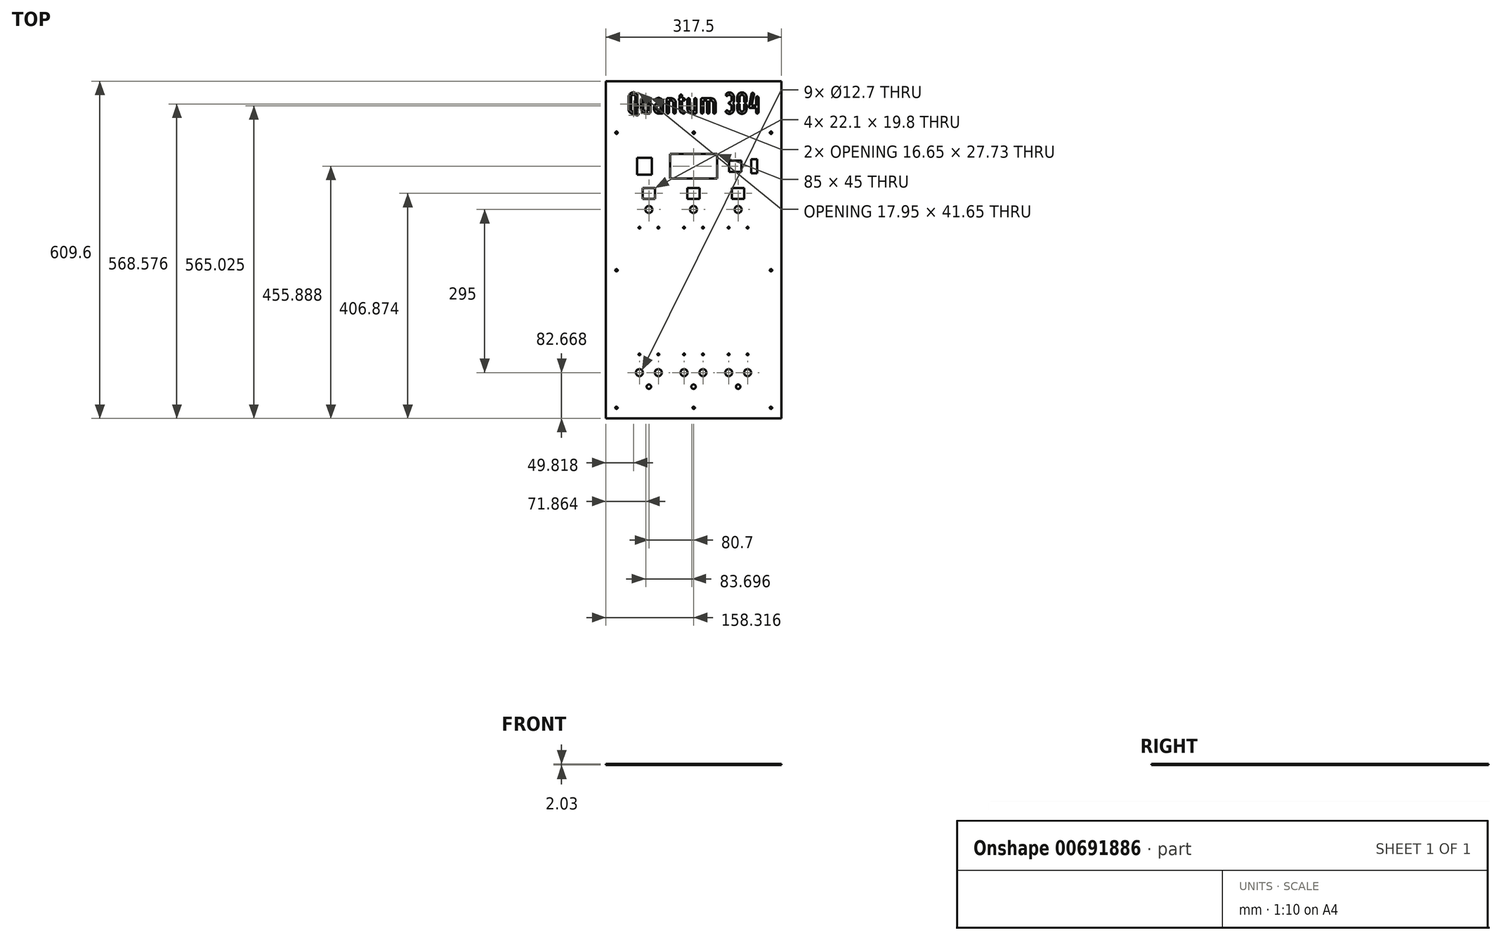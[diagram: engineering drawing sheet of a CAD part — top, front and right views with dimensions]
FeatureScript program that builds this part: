
annotation { "Feature Type Name" : "Feature", "Feature Type Description" : "" }
export const myFeature = defineFeature(function(context is Context, id is Id, definition is map)
    precondition{}
    {
        {
            var Q0;
            Q0=qCreatedBy(makeId("Top.planeOp"),FACE);
            var sketch = newSketch(context, id + "F0", { "sketchPlane" : qUnion([Q0])});
            skLineSegment(sketch, "E0.bottom", {"start": v(1.2, 127.96) * mm, "end": v(69.2, 127.96) * mm, "construction": true});
            skLineSegment(sketch, "E0.top", {"start": v(1.2, -116.24) * mm, "end": v(69.2, -116.24) * mm, "construction": true});
            skLineSegment(sketch, "E0.left", {"start": v(1.2, 127.96) * mm, "end": v(1.2, -116.24) * mm, "construction": true});
            skLineSegment(sketch, "E0.right", {"start": v(69.2, 127.96) * mm, "end": v(69.2, -116.24) * mm, "construction": true});
            skLineSegment(sketch, "E1.0", {"start": v(1.2, -104.24) * mm, "end": v(69.2, -104.24) * mm, "construction": true});
            skLineSegment(sketch, "E2.0", {"start": v(1.2, 115.96) * mm, "end": v(69.2, 115.96) * mm, "construction": true});
            skLineSegment(sketch, "E3", {"start": v(1.2, 5.86) * mm, "end": v(69.2, 5.86) * mm, "construction": true});
            skLineSegment(sketch, "E4.0", {"start": v(35.2, 127.96) * mm, "end": v(35.2, -116.24) * mm, "construction": true});
            skCircle(sketch, "E5", {"center": v(52.3, 120.46) * mm, "radius": 1.63 * mm});
            skCircle(sketch, "E6.MirrorC", {"center": v(18.1, 120.46) * mm, "radius": 1.63 * mm});
            skCircle(sketch, "E7.MirrorC", {"center": v(18.1, -108.74) * mm, "radius": 1.63 * mm});
            skCircle(sketch, "E8.MirrorC", {"center": v(52.3, -108.74) * mm, "radius": 1.63 * mm});
            skLineSegment(sketch, "E9.MirrorCS", {"start": v(81.9, 127.96) * mm, "end": v(81.9, -116.24) * mm, "construction": true});
            skLineSegment(sketch, "E10.MirrorCS", {"start": v(149.9, 127.96) * mm, "end": v(81.9, 127.96) * mm, "construction": true});
            skLineSegment(sketch, "E11.MirrorCS", {"start": v(149.9, 127.96) * mm, "end": v(149.9, -116.24) * mm, "construction": true});
            skLineSegment(sketch, "E12.MirrorCS", {"start": v(149.9, -116.24) * mm, "end": v(81.9, -116.24) * mm});
            skLineSegment(sketch, "E13.MirrorCS", {"start": v(149.9, -104.24) * mm, "end": v(81.9, -104.24) * mm, "construction": true});
            skLineSegment(sketch, "E14.MirrorCS", {"start": v(115.9, 127.96) * mm, "end": v(115.9, -116.24) * mm, "construction": true});
            skLineSegment(sketch, "E15.MirrorCS", {"start": v(149.9, 5.86) * mm, "end": v(81.9, 5.86) * mm, "construction": true});
            skLineSegment(sketch, "E16.MirrorCS", {"start": v(149.9, 115.96) * mm, "end": v(81.9, 115.96) * mm, "construction": true});
            skCircle(sketch, "E17.MirrorC", {"center": v(133, 120.46) * mm, "radius": 1.63 * mm});
            skCircle(sketch, "E18.MirrorC", {"center": v(98.8, 120.46) * mm, "radius": 1.63 * mm});
            skCircle(sketch, "E19.MirrorC", {"center": v(98.8, -108.74) * mm, "radius": 1.63 * mm});
            skCircle(sketch, "E20.MirrorC", {"center": v(133, -108.74) * mm, "radius": 1.63 * mm});
            skLineSegment(sketch, "E21.MirrorCS", {"start": v(162.6, 127.96) * mm, "end": v(162.6, -116.24) * mm, "construction": true});
            skLineSegment(sketch, "E22.MirrorCS", {"start": v(162.6, 127.96) * mm, "end": v(230.6, 127.96) * mm, "construction": true});
            skLineSegment(sketch, "E23.MirrorCS", {"start": v(230.6, 127.96) * mm, "end": v(230.6, -116.24) * mm, "construction": true});
            skLineSegment(sketch, "E24.MirrorCS", {"start": v(162.6, -116.24) * mm, "end": v(230.6, -116.24) * mm, "construction": true});
            skLineSegment(sketch, "E25.MirrorCS", {"start": v(162.6, -104.24) * mm, "end": v(230.6, -104.24) * mm, "construction": true});
            skLineSegment(sketch, "E26.MirrorCS", {"start": v(196.6, 127.96) * mm, "end": v(196.6, -116.24) * mm, "construction": true});
            skLineSegment(sketch, "E27.MirrorCS", {"start": v(162.6, 5.86) * mm, "end": v(230.6, 5.86) * mm, "construction": true});
            skLineSegment(sketch, "E28.MirrorCS", {"start": v(162.6, 115.96) * mm, "end": v(230.6, 115.96) * mm, "construction": true});
            skCircle(sketch, "E29.MirrorC", {"center": v(179.5, 120.46) * mm, "radius": 1.63 * mm});
            skCircle(sketch, "E30.MirrorC", {"center": v(213.7, 120.46) * mm, "radius": 1.63 * mm});
            skCircle(sketch, "E31.MirrorC", {"center": v(179.5, -108.74) * mm, "radius": 1.63 * mm});
            skCircle(sketch, "E32.MirrorC", {"center": v(213.7, -108.74) * mm, "radius": 1.63 * mm});
            skCircle(sketch, "E33", {"center": v(18.1, -141.64) * mm, "radius": 6.35 * mm});
            skCircle(sketch, "E34", {"center": v(52.3, -141.64) * mm, "radius": 6.35 * mm});
            skCircle(sketch, "E35.MirrorC", {"center": v(98.8, -141.64) * mm, "radius": 6.35 * mm});
            skCircle(sketch, "E36.MirrorC", {"center": v(133, -141.64) * mm, "radius": 6.35 * mm});
            skCircle(sketch, "E37.MirrorC", {"center": v(179.5, -141.64) * mm, "radius": 6.35 * mm});
            skCircle(sketch, "E38.MirrorC", {"center": v(213.7, -141.64) * mm, "radius": 6.35 * mm});
            skCircle(sketch, "E39", {"center": v(115.9, 153.36) * mm, "radius": 6.35 * mm});
            skCircle(sketch, "E40.MirrorC", {"center": v(196.6, 153.36) * mm, "radius": 6.35 * mm});
            skCircle(sketch, "E41.MirrorC", {"center": v(35.2, 153.36) * mm, "radius": 6.35 * mm});
            skCircle(sketch, "E42", {"center": v(115.9, 153.36) * mm, "radius": 8.26 * mm, "construction": true});
            skCircle(sketch, "E43.MirrorC", {"center": v(196.6, 153.36) * mm, "radius": 8.26 * mm, "construction": true});
            skCircle(sketch, "E44.MirrorC", {"center": v(35.2, 153.36) * mm, "radius": 8.26 * mm, "construction": true});
            skCircle(sketch, "E45", {"center": v(98.8, -141.64) * mm, "radius": 8.26 * mm, "construction": true});
            skCircle(sketch, "E46.MirrorC", {"center": v(133, -141.64) * mm, "radius": 8.26 * mm, "construction": true});
            skCircle(sketch, "E47.MirrorC", {"center": v(52.3, -141.64) * mm, "radius": 8.26 * mm, "construction": true});
            skCircle(sketch, "E48.MirrorC", {"center": v(18.1, -141.64) * mm, "radius": 8.26 * mm, "construction": true});
            skCircle(sketch, "E49.MirrorC", {"center": v(179.5, -141.64) * mm, "radius": 8.26 * mm, "construction": true});
            skCircle(sketch, "E50.MirrorC", {"center": v(213.7, -141.64) * mm, "radius": 8.26 * mm, "construction": true});
            skCircle(sketch, "E51", {"center": v(35.2, -167.04) * mm, "radius": 3.97 * mm});
            skCircle(sketch, "E52", {"center": v(35.2, -167.04) * mm, "radius": 12.5 * mm, "construction": true});
            skCircle(sketch, "E53.MirrorC", {"center": v(115.9, -167.04) * mm, "radius": 12.5 * mm, "construction": true});
            skCircle(sketch, "E54.MirrorC", {"center": v(115.9, -167.04) * mm, "radius": 3.97 * mm});
            skCircle(sketch, "E55.MirrorC", {"center": v(196.6, -167.04) * mm, "radius": 12.5 * mm, "construction": true});
            skCircle(sketch, "E56.MirrorC", {"center": v(196.6, -167.04) * mm, "radius": 3.97 * mm});
            skLineSegment(sketch, "E57", {"start": v(-42.41, -224.31) * mm, "end": v(275.09, -224.31) * mm});
            skLineSegment(sketch, "E58.0", {"start": v(-4.71, -186.21) * mm, "end": v(237.39, -186.21) * mm, "construction": true});
            skLineSegment(sketch, "E59.0", {"start": v(237.39, 311.23) * mm, "end": v(237.39, -224.31) * mm, "construction": true});
            skLineSegment(sketch, "E60.0", {"start": v(-4.71, 311.23) * mm, "end": v(-4.71, -224.31) * mm, "construction": true});
            skLineSegment(sketch, "E61.bottom", {"start": v(73.4, 254.08) * mm, "end": v(158.4, 254.08) * mm});
            skLineSegment(sketch, "E61.top", {"start": v(73.4, 209.08) * mm, "end": v(158.4, 209.08) * mm});
            skLineSegment(sketch, "E61.left", {"start": v(73.4, 254.08) * mm, "end": v(73.4, 209.08) * mm});
            skLineSegment(sketch, "E61.right", {"start": v(158.4, 254.08) * mm, "end": v(158.4, 209.08) * mm});
            skLineSegment(sketch, "E62.bottom", {"start": v(104.86, 192.46) * mm, "end": v(126.96, 192.46) * mm});
            skLineSegment(sketch, "E62.top", {"start": v(104.86, 172.66) * mm, "end": v(126.96, 172.66) * mm});
            skLineSegment(sketch, "E62.left", {"start": v(104.86, 192.46) * mm, "end": v(104.86, 172.66) * mm});
            skLineSegment(sketch, "E62.right", {"start": v(126.96, 192.46) * mm, "end": v(126.96, 172.66) * mm});
            skLineSegment(sketch, "E63.MirrorCS", {"start": v(185.56, 192.46) * mm, "end": v(185.56, 172.66) * mm});
            skLineSegment(sketch, "E64.MirrorCS", {"start": v(207.66, 192.46) * mm, "end": v(185.56, 192.46) * mm});
            skLineSegment(sketch, "E65.MirrorCS", {"start": v(207.66, 192.46) * mm, "end": v(207.66, 172.66) * mm});
            skLineSegment(sketch, "E66.MirrorCS", {"start": v(207.66, 172.66) * mm, "end": v(185.56, 172.66) * mm});
            skLineSegment(sketch, "E67.MirrorCS", {"start": v(46.26, 192.46) * mm, "end": v(46.26, 172.66) * mm});
            skLineSegment(sketch, "E68.MirrorCS", {"start": v(46.26, 192.46) * mm, "end": v(24.16, 192.46) * mm});
            skLineSegment(sketch, "E69.MirrorCS", {"start": v(24.16, 192.46) * mm, "end": v(24.16, 172.66) * mm});
            skLineSegment(sketch, "E70.MirrorCS", {"start": v(46.26, 172.66) * mm, "end": v(24.16, 172.66) * mm});
            skLineSegment(sketch, "E71.bottom", {"start": v(14.08, 246.75) * mm, "end": v(40.58, 246.75) * mm});
            skLineSegment(sketch, "E71.top", {"start": v(14.08, 216.4) * mm, "end": v(40.58, 216.4) * mm});
            skLineSegment(sketch, "E71.left", {"start": v(14.08, 246.75) * mm, "end": v(14.08, 216.4) * mm});
            skLineSegment(sketch, "E71.right", {"start": v(40.58, 246.75) * mm, "end": v(40.58, 216.4) * mm});
            skLineSegment(sketch, "E72.0", {"start": v(73.84, 231.58) * mm, "end": v(158.84, 231.58) * mm, "construction": true});
            skLineSegment(sketch, "E73", {"start": v(73.84, 231.58) * mm, "end": v(-4.71, 231.58) * mm, "construction": true});
            skLineSegment(sketch, "E74", {"start": v(158.84, 231.58) * mm, "end": v(237.39, 231.58) * mm, "construction": true});
            skLineSegment(sketch, "E75", {"start": v(237.39, 273.13) * mm, "end": v(-4.71, 273.13) * mm, "construction": true});
            skLineSegment(sketch, "E76.0", {"start": v(237.39, 311.23) * mm, "end": v(-4.71, 311.23) * mm, "construction": true});
            skLineSegment(sketch, "E77", {"start": v(-1.54, 357.62) * mm, "end": v(-1.43, 358.44) * mm});
            skLineSegment(sketch, "E78", {"start": v(-1.43, 358.44) * mm, "end": v(-1.23, 359.2) * mm});
            skLineSegment(sketch, "E79", {"start": v(-1.23, 359.2) * mm, "end": v(-0.97, 359.98) * mm});
            skLineSegment(sketch, "E80", {"start": v(-0.97, 359.98) * mm, "end": v(-0.6, 360.69) * mm});
            skLineSegment(sketch, "E81", {"start": v(-0.6, 360.69) * mm, "end": v(-0.2, 361.37) * mm});
            skLineSegment(sketch, "E82", {"start": v(-0.2, 361.37) * mm, "end": v(0.3, 362.02) * mm});
            skLineSegment(sketch, "E83", {"start": v(0.3, 362.02) * mm, "end": v(0.87, 362.65) * mm});
            skLineSegment(sketch, "E84", {"start": v(0.87, 362.65) * mm, "end": v(1.5, 363.22) * mm});
            skLineSegment(sketch, "E85", {"start": v(1.5, 363.22) * mm, "end": v(2.15, 363.73) * mm});
            skLineSegment(sketch, "E86", {"start": v(2.15, 363.73) * mm, "end": v(2.83, 364.12) * mm});
            skLineSegment(sketch, "E87", {"start": v(2.83, 364.12) * mm, "end": v(3.54, 364.5) * mm});
            skLineSegment(sketch, "E88", {"start": v(3.54, 364.5) * mm, "end": v(4.31, 364.75) * mm});
            skLineSegment(sketch, "E89", {"start": v(4.31, 364.75) * mm, "end": v(5.08, 364.95) * mm});
            skLineSegment(sketch, "E90", {"start": v(5.08, 364.95) * mm, "end": v(5.9, 365.06) * mm});
            skLineSegment(sketch, "E91", {"start": v(5.9, 365.06) * mm, "end": v(6.75, 365.1) * mm});
            skLineSegment(sketch, "E92", {"start": v(6.75, 365.1) * mm, "end": v(7.58, 365.06) * mm});
            skLineSegment(sketch, "E93", {"start": v(7.58, 365.06) * mm, "end": v(8.4, 364.95) * mm});
            skLineSegment(sketch, "E94", {"start": v(8.4, 364.95) * mm, "end": v(9.17, 364.75) * mm});
            skLineSegment(sketch, "E95", {"start": v(9.17, 364.75) * mm, "end": v(9.94, 364.5) * mm});
            skLineSegment(sketch, "E96", {"start": v(9.94, 364.5) * mm, "end": v(10.65, 364.12) * mm});
            skLineSegment(sketch, "E97", {"start": v(10.65, 364.12) * mm, "end": v(11.33, 363.73) * mm});
            skLineSegment(sketch, "E98", {"start": v(11.33, 363.73) * mm, "end": v(11.98, 363.22) * mm});
            skLineSegment(sketch, "E99", {"start": v(11.98, 363.22) * mm, "end": v(12.6, 362.65) * mm});
            skLineSegment(sketch, "E100", {"start": v(12.6, 362.65) * mm, "end": v(13.18, 362.02) * mm});
            skLineSegment(sketch, "E101", {"start": v(13.18, 362.02) * mm, "end": v(13.69, 361.37) * mm});
            skLineSegment(sketch, "E102", {"start": v(13.69, 361.37) * mm, "end": v(14.08, 360.69) * mm});
            skLineSegment(sketch, "E103", {"start": v(14.08, 360.69) * mm, "end": v(14.45, 359.98) * mm});
            skLineSegment(sketch, "E104", {"start": v(14.45, 359.98) * mm, "end": v(14.7, 359.2) * mm});
            skLineSegment(sketch, "E105", {"start": v(14.7, 359.2) * mm, "end": v(14.9, 358.44) * mm});
            skLineSegment(sketch, "E106", {"start": v(14.9, 358.44) * mm, "end": v(15.02, 357.62) * mm});
            skLineSegment(sketch, "E107", {"start": v(15.02, 357.62) * mm, "end": v(15.05, 356.8) * mm});
            skLineSegment(sketch, "E108", {"start": v(15.05, 356.8) * mm, "end": v(15.05, 334.63) * mm});
            skLineSegment(sketch, "E109", {"start": v(15.05, 334.63) * mm, "end": v(15.05, 334.38) * mm});
            skLineSegment(sketch, "E110", {"start": v(15.05, 334.38) * mm, "end": v(15.05, 334.12) * mm});
            skLineSegment(sketch, "E111", {"start": v(15.05, 334.12) * mm, "end": v(15.02, 333.87) * mm});
            skLineSegment(sketch, "E112", {"start": v(15.02, 333.87) * mm, "end": v(15, 333.61) * mm});
            skLineSegment(sketch, "E113", {"start": v(15, 333.61) * mm, "end": v(14.97, 333.38) * mm});
            skLineSegment(sketch, "E114", {"start": v(14.97, 333.38) * mm, "end": v(14.94, 333.13) * mm});
            skLineSegment(sketch, "E115", {"start": v(14.94, 333.13) * mm, "end": v(14.9, 332.9) * mm});
            skLineSegment(sketch, "E116", {"start": v(14.9, 332.9) * mm, "end": v(14.85, 332.65) * mm});
            skLineSegment(sketch, "E117", {"start": v(14.85, 332.65) * mm, "end": v(14.82, 332.5) * mm});
            skLineSegment(sketch, "E118", {"start": v(14.82, 332.5) * mm, "end": v(14.77, 332.33) * mm});
            skLineSegment(sketch, "E119", {"start": v(14.77, 332.33) * mm, "end": v(14.7, 332.2) * mm});
            skLineSegment(sketch, "E120", {"start": v(14.7, 332.2) * mm, "end": v(14.65, 332.05) * mm});
            skLineSegment(sketch, "E121", {"start": v(14.65, 332.05) * mm, "end": v(14.57, 331.94) * mm});
            skLineSegment(sketch, "E122", {"start": v(14.57, 331.94) * mm, "end": v(14.48, 331.8) * mm});
            skLineSegment(sketch, "E123", {"start": v(14.48, 331.8) * mm, "end": v(14.37, 331.68) * mm});
            skLineSegment(sketch, "E124", {"start": v(14.37, 331.68) * mm, "end": v(14.26, 331.54) * mm});
            skLineSegment(sketch, "E125", {"start": v(14.26, 331.54) * mm, "end": v(14.08, 331.4) * mm});
            skLineSegment(sketch, "E126", {"start": v(14.08, 331.4) * mm, "end": v(13.89, 331.25) * mm});
            skLineSegment(sketch, "E127", {"start": v(13.89, 331.25) * mm, "end": v(13.72, 331.14) * mm});
            skLineSegment(sketch, "E128", {"start": v(13.72, 331.14) * mm, "end": v(13.52, 331.06) * mm});
            skLineSegment(sketch, "E129", {"start": v(13.52, 331.06) * mm, "end": v(13.32, 330.97) * mm});
            skLineSegment(sketch, "E130", {"start": v(13.32, 330.97) * mm, "end": v(13.12, 330.91) * mm});
            skLineSegment(sketch, "E131", {"start": v(13.12, 330.91) * mm, "end": v(12.9, 330.88) * mm});
            skLineSegment(sketch, "E132", {"start": v(12.9, 330.88) * mm, "end": v(12.66, 330.88) * mm});
            skLineSegment(sketch, "E133", {"start": v(12.66, 330.88) * mm, "end": v(12.44, 330.88) * mm});
            skLineSegment(sketch, "E134", {"start": v(12.44, 330.88) * mm, "end": v(12.24, 330.91) * mm});
            skLineSegment(sketch, "E135", {"start": v(12.24, 330.91) * mm, "end": v(12.01, 330.97) * mm});
            skLineSegment(sketch, "E136", {"start": v(12.01, 330.97) * mm, "end": v(11.81, 331.06) * mm});
            skLineSegment(sketch, "E137", {"start": v(11.81, 331.06) * mm, "end": v(11.64, 331.14) * mm});
            skLineSegment(sketch, "E138", {"start": v(11.64, 331.14) * mm, "end": v(11.44, 331.25) * mm});
            skLineSegment(sketch, "E139", {"start": v(11.44, 331.25) * mm, "end": v(11.27, 331.37) * mm});
            skLineSegment(sketch, "E140", {"start": v(11.27, 331.37) * mm, "end": v(11.1, 331.54) * mm});
            skLineSegment(sketch, "E141", {"start": v(11.1, 331.54) * mm, "end": v(10.96, 331.7) * mm});
            skLineSegment(sketch, "E142", {"start": v(10.96, 331.7) * mm, "end": v(10.82, 331.88) * mm});
            skLineSegment(sketch, "E143", {"start": v(10.82, 331.88) * mm, "end": v(10.7, 332.05) * mm});
            skLineSegment(sketch, "E144", {"start": v(10.7, 332.05) * mm, "end": v(10.62, 332.25) * mm});
            skLineSegment(sketch, "E145", {"start": v(10.62, 332.25) * mm, "end": v(10.53, 332.45) * mm});
            skLineSegment(sketch, "E146", {"start": v(10.53, 332.45) * mm, "end": v(10.5, 332.65) * mm});
            skLineSegment(sketch, "E147", {"start": v(10.5, 332.65) * mm, "end": v(10.48, 332.87) * mm});
            skLineSegment(sketch, "E148", {"start": v(10.48, 332.87) * mm, "end": v(10.45, 333.1) * mm});
            skLineSegment(sketch, "E149", {"start": v(10.45, 333.1) * mm, "end": v(10.45, 333.16) * mm});
            skLineSegment(sketch, "E150", {"start": v(10.45, 333.16) * mm, "end": v(10.45, 333.21) * mm});
            skLineSegment(sketch, "E151", {"start": v(10.45, 333.21) * mm, "end": v(10.45, 333.27) * mm});
            skLineSegment(sketch, "E152", {"start": v(10.45, 333.27) * mm, "end": v(10.45, 333.33) * mm});
            skLineSegment(sketch, "E153", {"start": v(10.45, 333.33) * mm, "end": v(10.48, 333.38) * mm});
            skLineSegment(sketch, "E154", {"start": v(10.48, 333.38) * mm, "end": v(10.48, 333.47) * mm});
            skLineSegment(sketch, "E155", {"start": v(10.48, 333.47) * mm, "end": v(10.48, 333.53) * mm});
            skLineSegment(sketch, "E156", {"start": v(10.48, 333.53) * mm, "end": v(10.48, 333.58) * mm});
            skLineSegment(sketch, "E157", {"start": v(10.48, 333.58) * mm, "end": v(10.5, 333.73) * mm});
            skLineSegment(sketch, "E158", {"start": v(10.5, 333.73) * mm, "end": v(10.53, 333.84) * mm});
            skLineSegment(sketch, "E159", {"start": v(10.53, 333.84) * mm, "end": v(10.56, 333.98) * mm});
            skLineSegment(sketch, "E160", {"start": v(10.56, 333.98) * mm, "end": v(10.6, 334.1) * mm});
            skLineSegment(sketch, "E161", {"start": v(10.6, 334.1) * mm, "end": v(10.6, 334.24) * mm});
            skLineSegment(sketch, "E162", {"start": v(10.6, 334.24) * mm, "end": v(10.62, 334.35) * mm});
            skLineSegment(sketch, "E163", {"start": v(10.62, 334.35) * mm, "end": v(10.62, 334.5) * mm});
            skLineSegment(sketch, "E164", {"start": v(10.62, 334.5) * mm, "end": v(10.62, 334.63) * mm});
            skLineSegment(sketch, "E165", {"start": v(10.62, 334.63) * mm, "end": v(10.62, 356.8) * mm});
            skLineSegment(sketch, "E166", {"start": v(10.62, 356.8) * mm, "end": v(10.6, 357.16) * mm});
            skLineSegment(sketch, "E167", {"start": v(10.6, 357.16) * mm, "end": v(10.56, 357.56) * mm});
            skLineSegment(sketch, "E168", {"start": v(10.56, 357.56) * mm, "end": v(10.45, 357.93) * mm});
            skLineSegment(sketch, "E169", {"start": v(10.45, 357.93) * mm, "end": v(10.33, 358.27) * mm});
            skLineSegment(sketch, "E170", {"start": v(10.33, 358.27) * mm, "end": v(10.16, 358.61) * mm});
            skLineSegment(sketch, "E171", {"start": v(10.16, 358.61) * mm, "end": v(10, 358.93) * mm});
            skLineSegment(sketch, "E172", {"start": v(10, 358.93) * mm, "end": v(9.74, 359.24) * mm});
            skLineSegment(sketch, "E173", {"start": v(9.74, 359.24) * mm, "end": v(9.48, 359.52) * mm});
            skLineSegment(sketch, "E174", {"start": v(9.48, 359.52) * mm, "end": v(9.2, 359.78) * mm});
            skLineSegment(sketch, "E175", {"start": v(9.2, 359.78) * mm, "end": v(8.89, 360.03) * mm});
            skLineSegment(sketch, "E176", {"start": v(8.89, 360.03) * mm, "end": v(8.57, 360.2) * mm});
            skLineSegment(sketch, "E177", {"start": v(8.57, 360.2) * mm, "end": v(8.23, 360.37) * mm});
            skLineSegment(sketch, "E178", {"start": v(8.23, 360.37) * mm, "end": v(7.9, 360.49) * mm});
            skLineSegment(sketch, "E179", {"start": v(7.9, 360.49) * mm, "end": v(7.52, 360.6) * mm});
            skLineSegment(sketch, "E180", {"start": v(7.52, 360.6) * mm, "end": v(7.12, 360.63) * mm});
            skLineSegment(sketch, "E181", {"start": v(7.12, 360.63) * mm, "end": v(6.75, 360.66) * mm});
            skLineSegment(sketch, "E182", {"start": v(6.75, 360.66) * mm, "end": v(6.36, 360.63) * mm});
            skLineSegment(sketch, "E183", {"start": v(6.36, 360.63) * mm, "end": v(5.96, 360.6) * mm});
            skLineSegment(sketch, "E184", {"start": v(5.96, 360.6) * mm, "end": v(5.6, 360.49) * mm});
            skLineSegment(sketch, "E185", {"start": v(5.6, 360.49) * mm, "end": v(5.25, 360.37) * mm});
            skLineSegment(sketch, "E186", {"start": v(5.25, 360.37) * mm, "end": v(4.9, 360.2) * mm});
            skLineSegment(sketch, "E187", {"start": v(4.9, 360.2) * mm, "end": v(4.6, 360.03) * mm});
            skLineSegment(sketch, "E188", {"start": v(4.6, 360.03) * mm, "end": v(4.28, 359.78) * mm});
            skLineSegment(sketch, "E189", {"start": v(4.28, 359.78) * mm, "end": v(4, 359.52) * mm});
            skLineSegment(sketch, "E190", {"start": v(4, 359.52) * mm, "end": v(3.74, 359.24) * mm});
            skLineSegment(sketch, "E191", {"start": v(3.74, 359.24) * mm, "end": v(3.49, 358.93) * mm});
            skLineSegment(sketch, "E192", {"start": v(3.49, 358.93) * mm, "end": v(3.32, 358.61) * mm});
            skLineSegment(sketch, "E193", {"start": v(3.32, 358.61) * mm, "end": v(3.15, 358.27) * mm});
            skLineSegment(sketch, "E194", {"start": v(3.15, 358.27) * mm, "end": v(3.03, 357.93) * mm});
            skLineSegment(sketch, "E195", {"start": v(3.03, 357.93) * mm, "end": v(2.92, 357.56) * mm});
            skLineSegment(sketch, "E196", {"start": v(2.92, 357.56) * mm, "end": v(2.9, 357.16) * mm});
            skLineSegment(sketch, "E197", {"start": v(2.9, 357.16) * mm, "end": v(2.86, 356.8) * mm});
            skLineSegment(sketch, "E198", {"start": v(2.86, 356.8) * mm, "end": v(2.86, 334.63) * mm});
            skLineSegment(sketch, "E199", {"start": v(2.86, 334.63) * mm, "end": v(2.9, 334.24) * mm});
            skLineSegment(sketch, "E200", {"start": v(2.9, 334.24) * mm, "end": v(2.92, 333.87) * mm});
            skLineSegment(sketch, "E201", {"start": v(2.92, 333.87) * mm, "end": v(3, 333.53) * mm});
            skLineSegment(sketch, "E202", {"start": v(3, 333.53) * mm, "end": v(3.12, 333.19) * mm});
            skLineSegment(sketch, "E203", {"start": v(3.12, 333.19) * mm, "end": v(3.29, 332.87) * mm});
            skLineSegment(sketch, "E204", {"start": v(3.29, 332.87) * mm, "end": v(3.46, 332.59) * mm});
            skLineSegment(sketch, "E205", {"start": v(3.46, 332.59) * mm, "end": v(3.69, 332.3) * mm});
            skLineSegment(sketch, "E206", {"start": v(3.69, 332.3) * mm, "end": v(3.94, 332.05) * mm});
            skLineSegment(sketch, "E207", {"start": v(3.94, 332.05) * mm, "end": v(4.2, 331.82) * mm});
            skLineSegment(sketch, "E208", {"start": v(4.2, 331.82) * mm, "end": v(4.48, 331.6) * mm});
            skLineSegment(sketch, "E209", {"start": v(4.48, 331.6) * mm, "end": v(4.77, 331.4) * mm});
            skLineSegment(sketch, "E210", {"start": v(4.77, 331.4) * mm, "end": v(5.08, 331.23) * mm});
            skLineSegment(sketch, "E211", {"start": v(5.08, 331.23) * mm, "end": v(5.36, 331.08) * mm});
            skLineSegment(sketch, "E212", {"start": v(5.36, 331.08) * mm, "end": v(5.7, 330.94) * mm});
            skLineSegment(sketch, "E213", {"start": v(5.7, 330.94) * mm, "end": v(6.02, 330.83) * mm});
            skLineSegment(sketch, "E214", {"start": v(6.02, 330.83) * mm, "end": v(6.36, 330.71) * mm});
            skLineSegment(sketch, "E215", {"start": v(6.36, 330.71) * mm, "end": v(14.85, 327.76) * mm});
            skLineSegment(sketch, "E216", {"start": v(14.85, 327.76) * mm, "end": v(15.08, 327.67) * mm});
            skLineSegment(sketch, "E217", {"start": v(15.08, 327.67) * mm, "end": v(15.28, 327.56) * mm});
            skLineSegment(sketch, "E218", {"start": v(15.28, 327.56) * mm, "end": v(15.45, 327.45) * mm});
            skLineSegment(sketch, "E219", {"start": v(15.45, 327.45) * mm, "end": v(15.62, 327.3) * mm});
            skLineSegment(sketch, "E220", {"start": v(15.62, 327.3) * mm, "end": v(15.79, 327.16) * mm});
            skLineSegment(sketch, "E221", {"start": v(15.79, 327.16) * mm, "end": v(15.93, 327) * mm});
            skLineSegment(sketch, "E222", {"start": v(15.93, 327) * mm, "end": v(16.04, 326.82) * mm});
            skLineSegment(sketch, "E223", {"start": v(16.04, 326.82) * mm, "end": v(16.16, 326.62) * mm});
            skLineSegment(sketch, "E224", {"start": v(16.16, 326.62) * mm, "end": v(16.22, 326.48) * mm});
            skLineSegment(sketch, "E225", {"start": v(16.22, 326.48) * mm, "end": v(16.24, 326.37) * mm});
            skLineSegment(sketch, "E226", {"start": v(16.24, 326.37) * mm, "end": v(16.3, 326.25) * mm});
            skLineSegment(sketch, "E227", {"start": v(16.3, 326.25) * mm, "end": v(16.33, 326.11) * mm});
            skLineSegment(sketch, "E228", {"start": v(16.33, 326.11) * mm, "end": v(16.36, 326) * mm});
            skLineSegment(sketch, "E229", {"start": v(16.36, 326) * mm, "end": v(16.36, 325.88) * mm});
            skLineSegment(sketch, "E230", {"start": v(16.36, 325.88) * mm, "end": v(16.39, 325.77) * mm});
            skLineSegment(sketch, "E231", {"start": v(16.39, 325.77) * mm, "end": v(16.39, 325.66) * mm});
            skLineSegment(sketch, "E232", {"start": v(16.39, 325.66) * mm, "end": v(16.39, 325.57) * mm});
            skLineSegment(sketch, "E233", {"start": v(16.39, 325.57) * mm, "end": v(16.39, 325.49) * mm});
            skLineSegment(sketch, "E234", {"start": v(16.39, 325.49) * mm, "end": v(16.36, 325.4) * mm});
            skLineSegment(sketch, "E235", {"start": v(16.36, 325.4) * mm, "end": v(16.36, 325.32) * mm});
            skLineSegment(sketch, "E236", {"start": v(16.36, 325.32) * mm, "end": v(16.33, 325.23) * mm});
            skLineSegment(sketch, "E237", {"start": v(16.33, 325.23) * mm, "end": v(16.33, 325.15) * mm});
            skLineSegment(sketch, "E238", {"start": v(16.33, 325.15) * mm, "end": v(16.3, 325.03) * mm});
            skLineSegment(sketch, "E239", {"start": v(16.3, 325.03) * mm, "end": v(16.27, 324.95) * mm});
            skLineSegment(sketch, "E240", {"start": v(16.27, 324.95) * mm, "end": v(16.19, 324.75) * mm});
            skLineSegment(sketch, "E241", {"start": v(16.19, 324.75) * mm, "end": v(16.07, 324.55) * mm});
            skLineSegment(sketch, "E242", {"start": v(16.07, 324.55) * mm, "end": v(15.96, 324.35) * mm});
            skLineSegment(sketch, "E243", {"start": v(15.96, 324.35) * mm, "end": v(15.85, 324.18) * mm});
            skLineSegment(sketch, "E244", {"start": v(15.85, 324.18) * mm, "end": v(15.68, 324.04) * mm});
            skLineSegment(sketch, "E245", {"start": v(15.68, 324.04) * mm, "end": v(15.5, 323.9) * mm});
            skLineSegment(sketch, "E246", {"start": v(15.5, 323.9) * mm, "end": v(15.33, 323.75) * mm});
            skLineSegment(sketch, "E247", {"start": v(15.33, 323.75) * mm, "end": v(15.14, 323.64) * mm});
            skLineSegment(sketch, "E248", {"start": v(15.14, 323.64) * mm, "end": v(15.02, 323.61) * mm});
            skLineSegment(sketch, "E249", {"start": v(15.02, 323.61) * mm, "end": v(14.88, 323.55) * mm});
            skLineSegment(sketch, "E250", {"start": v(14.88, 323.55) * mm, "end": v(14.77, 323.53) * mm});
            skLineSegment(sketch, "E251", {"start": v(14.77, 323.53) * mm, "end": v(14.65, 323.5) * mm});
            skLineSegment(sketch, "E252", {"start": v(14.65, 323.5) * mm, "end": v(14.51, 323.47) * mm});
            skLineSegment(sketch, "E253", {"start": v(14.51, 323.47) * mm, "end": v(14.4, 323.44) * mm});
            skLineSegment(sketch, "E254", {"start": v(14.4, 323.44) * mm, "end": v(14.28, 323.44) * mm});
            skLineSegment(sketch, "E255", {"start": v(14.28, 323.44) * mm, "end": v(14.17, 323.44) * mm});
            skLineSegment(sketch, "E256", {"start": v(14.17, 323.44) * mm, "end": v(14.08, 323.44) * mm});
            skLineSegment(sketch, "E257", {"start": v(14.08, 323.44) * mm, "end": v(13.97, 323.44) * mm});
            skLineSegment(sketch, "E258", {"start": v(13.97, 323.44) * mm, "end": v(13.89, 323.44) * mm});
            skLineSegment(sketch, "E259", {"start": v(13.89, 323.44) * mm, "end": v(13.8, 323.47) * mm});
            skLineSegment(sketch, "E260", {"start": v(13.8, 323.47) * mm, "end": v(13.72, 323.47) * mm});
            skLineSegment(sketch, "E261", {"start": v(13.72, 323.47) * mm, "end": v(13.63, 323.5) * mm});
            skLineSegment(sketch, "E262", {"start": v(13.63, 323.5) * mm, "end": v(13.54, 323.53) * mm});
            skLineSegment(sketch, "E263", {"start": v(13.54, 323.53) * mm, "end": v(13.43, 323.55) * mm});
            skLineSegment(sketch, "E264", {"start": v(13.43, 323.55) * mm, "end": v(4.54, 326.6) * mm});
            skLineSegment(sketch, "E265", {"start": v(4.54, 326.6) * mm, "end": v(3.97, 326.8) * mm});
            skLineSegment(sketch, "E266", {"start": v(3.97, 326.8) * mm, "end": v(3.46, 327.02) * mm});
            skLineSegment(sketch, "E267", {"start": v(3.46, 327.02) * mm, "end": v(2.95, 327.28) * mm});
            skLineSegment(sketch, "E268", {"start": v(2.95, 327.28) * mm, "end": v(2.5, 327.53) * mm});
            skLineSegment(sketch, "E269", {"start": v(2.5, 327.53) * mm, "end": v(2.04, 327.82) * mm});
            skLineSegment(sketch, "E270", {"start": v(2.04, 327.82) * mm, "end": v(1.61, 328.1) * mm});
            skLineSegment(sketch, "E271", {"start": v(1.61, 328.1) * mm, "end": v(1.24, 328.41) * mm});
            skLineSegment(sketch, "E272", {"start": v(1.24, 328.41) * mm, "end": v(0.87, 328.75) * mm});
            skLineSegment(sketch, "E273", {"start": v(0.87, 328.75) * mm, "end": v(0.3, 329.38) * mm});
            skLineSegment(sketch, "E274", {"start": v(0.3, 329.38) * mm, "end": v(-0.2, 330.03) * mm});
            skLineSegment(sketch, "E275", {"start": v(-0.2, 330.03) * mm, "end": v(-0.6, 330.71) * mm});
            skLineSegment(sketch, "E276", {"start": v(-0.6, 330.71) * mm, "end": v(-0.97, 331.42) * mm});
            skLineSegment(sketch, "E277", {"start": v(-0.97, 331.42) * mm, "end": v(-1.23, 332.2) * mm});
            skLineSegment(sketch, "E278", {"start": v(-1.23, 332.2) * mm, "end": v(-1.43, 332.96) * mm});
            skLineSegment(sketch, "E279", {"start": v(-1.43, 332.96) * mm, "end": v(-1.54, 333.78) * mm});
            skLineSegment(sketch, "E280", {"start": v(-1.54, 333.78) * mm, "end": v(-1.57, 334.63) * mm});
            skLineSegment(sketch, "E281", {"start": v(-1.57, 334.63) * mm, "end": v(-1.57, 356.8) * mm});
            skLineSegment(sketch, "E282", {"start": v(-1.57, 356.8) * mm, "end": v(-1.54, 357.62) * mm});
            skLineSegment(sketch, "E283", {"start": v(21.19, 334.32) * mm, "end": v(21.13, 335.17) * mm});
            skLineSegment(sketch, "E284", {"start": v(21.13, 335.17) * mm, "end": v(21.13, 352.36) * mm});
            skLineSegment(sketch, "E285", {"start": v(21.13, 352.36) * mm, "end": v(21.16, 352.56) * mm});
            skLineSegment(sketch, "E286", {"start": v(21.16, 352.56) * mm, "end": v(21.19, 352.79) * mm});
            skLineSegment(sketch, "E287", {"start": v(21.19, 352.79) * mm, "end": v(21.24, 352.99) * mm});
            skLineSegment(sketch, "E288", {"start": v(21.24, 352.99) * mm, "end": v(21.3, 353.19) * mm});
            skLineSegment(sketch, "E289", {"start": v(21.3, 353.19) * mm, "end": v(21.39, 353.39) * mm});
            skLineSegment(sketch, "E290", {"start": v(21.39, 353.39) * mm, "end": v(21.5, 353.58) * mm});
            skLineSegment(sketch, "E291", {"start": v(21.5, 353.58) * mm, "end": v(21.64, 353.75) * mm});
            skLineSegment(sketch, "E292", {"start": v(21.64, 353.75) * mm, "end": v(21.78, 353.93) * mm});
            skLineSegment(sketch, "E293", {"start": v(21.78, 353.93) * mm, "end": v(21.95, 354.07) * mm});
            skLineSegment(sketch, "E294", {"start": v(21.95, 354.07) * mm, "end": v(22.12, 354.2) * mm});
            skLineSegment(sketch, "E295", {"start": v(22.12, 354.2) * mm, "end": v(22.32, 354.32) * mm});
            skLineSegment(sketch, "E296", {"start": v(22.32, 354.32) * mm, "end": v(22.52, 354.4) * mm});
            skLineSegment(sketch, "E297", {"start": v(22.52, 354.4) * mm, "end": v(22.72, 354.46) * mm});
            skLineSegment(sketch, "E298", {"start": v(22.72, 354.46) * mm, "end": v(22.92, 354.52) * mm});
            skLineSegment(sketch, "E299", {"start": v(22.92, 354.52) * mm, "end": v(23.15, 354.55) * mm});
            skLineSegment(sketch, "E300", {"start": v(23.15, 354.55) * mm, "end": v(23.35, 354.58) * mm});
            skLineSegment(sketch, "E301", {"start": v(23.35, 354.58) * mm, "end": v(23.57, 354.55) * mm});
            skLineSegment(sketch, "E302", {"start": v(23.57, 354.55) * mm, "end": v(23.8, 354.52) * mm});
            skLineSegment(sketch, "E303", {"start": v(23.8, 354.52) * mm, "end": v(24, 354.46) * mm});
            skLineSegment(sketch, "E304", {"start": v(24, 354.46) * mm, "end": v(24.2, 354.4) * mm});
            skLineSegment(sketch, "E305", {"start": v(24.2, 354.4) * mm, "end": v(24.4, 354.32) * mm});
            skLineSegment(sketch, "E306", {"start": v(24.4, 354.32) * mm, "end": v(24.6, 354.2) * mm});
            skLineSegment(sketch, "E307", {"start": v(24.6, 354.2) * mm, "end": v(24.77, 354.07) * mm});
            skLineSegment(sketch, "E308", {"start": v(24.77, 354.07) * mm, "end": v(24.94, 353.93) * mm});
            skLineSegment(sketch, "E309", {"start": v(24.94, 353.93) * mm, "end": v(25.08, 353.75) * mm});
            skLineSegment(sketch, "E310", {"start": v(25.08, 353.75) * mm, "end": v(25.22, 353.58) * mm});
            skLineSegment(sketch, "E311", {"start": v(25.22, 353.58) * mm, "end": v(25.33, 353.39) * mm});
            skLineSegment(sketch, "E312", {"start": v(25.33, 353.39) * mm, "end": v(25.42, 353.19) * mm});
            skLineSegment(sketch, "E313", {"start": v(25.42, 353.19) * mm, "end": v(25.48, 352.99) * mm});
            skLineSegment(sketch, "E314", {"start": v(25.48, 352.99) * mm, "end": v(25.53, 352.79) * mm});
            skLineSegment(sketch, "E315", {"start": v(25.53, 352.79) * mm, "end": v(25.56, 352.56) * mm});
            skLineSegment(sketch, "E316", {"start": v(25.56, 352.56) * mm, "end": v(25.56, 352.36) * mm});
            skLineSegment(sketch, "E317", {"start": v(25.56, 352.36) * mm, "end": v(25.56, 335.17) * mm});
            skLineSegment(sketch, "E318", {"start": v(25.56, 335.17) * mm, "end": v(25.6, 334.78) * mm});
            skLineSegment(sketch, "E319", {"start": v(25.6, 334.78) * mm, "end": v(25.65, 334.4) * mm});
            skLineSegment(sketch, "E320", {"start": v(25.65, 334.4) * mm, "end": v(25.73, 334.04) * mm});
            skLineSegment(sketch, "E321", {"start": v(25.73, 334.04) * mm, "end": v(25.85, 333.7) * mm});
            skLineSegment(sketch, "E322", {"start": v(25.85, 333.7) * mm, "end": v(26.02, 333.36) * mm});
            skLineSegment(sketch, "E323", {"start": v(26.02, 333.36) * mm, "end": v(26.22, 333.04) * mm});
            skLineSegment(sketch, "E324", {"start": v(26.22, 333.04) * mm, "end": v(26.44, 332.73) * mm});
            skLineSegment(sketch, "E325", {"start": v(26.44, 332.73) * mm, "end": v(26.7, 332.42) * mm});
            skLineSegment(sketch, "E326", {"start": v(26.7, 332.42) * mm, "end": v(27.01, 332.16) * mm});
            skLineSegment(sketch, "E327", {"start": v(27.01, 332.16) * mm, "end": v(27.32, 331.94) * mm});
            skLineSegment(sketch, "E328", {"start": v(27.32, 331.94) * mm, "end": v(27.64, 331.74) * mm});
            skLineSegment(sketch, "E329", {"start": v(27.64, 331.74) * mm, "end": v(27.98, 331.57) * mm});
            skLineSegment(sketch, "E330", {"start": v(27.98, 331.57) * mm, "end": v(28.32, 331.45) * mm});
            skLineSegment(sketch, "E331", {"start": v(28.32, 331.45) * mm, "end": v(28.69, 331.37) * mm});
            skLineSegment(sketch, "E332", {"start": v(28.69, 331.37) * mm, "end": v(29.06, 331.31) * mm});
            skLineSegment(sketch, "E333", {"start": v(29.06, 331.31) * mm, "end": v(29.45, 331.28) * mm});
            skLineSegment(sketch, "E334", {"start": v(29.45, 331.28) * mm, "end": v(33.35, 331.28) * mm});
            skLineSegment(sketch, "E335", {"start": v(33.35, 331.28) * mm, "end": v(33.35, 352.36) * mm});
            skLineSegment(sketch, "E336", {"start": v(33.35, 352.36) * mm, "end": v(33.35, 352.56) * mm});
            skLineSegment(sketch, "E337", {"start": v(33.35, 352.56) * mm, "end": v(33.37, 352.79) * mm});
            skLineSegment(sketch, "E338", {"start": v(33.37, 352.79) * mm, "end": v(33.43, 352.99) * mm});
            skLineSegment(sketch, "E339", {"start": v(33.43, 352.99) * mm, "end": v(33.49, 353.19) * mm});
            skLineSegment(sketch, "E340", {"start": v(33.49, 353.19) * mm, "end": v(33.57, 353.39) * mm});
            skLineSegment(sketch, "E341", {"start": v(33.57, 353.39) * mm, "end": v(33.69, 353.58) * mm});
            skLineSegment(sketch, "E342", {"start": v(33.69, 353.58) * mm, "end": v(33.83, 353.75) * mm});
            skLineSegment(sketch, "E343", {"start": v(33.83, 353.75) * mm, "end": v(33.97, 353.93) * mm});
            skLineSegment(sketch, "E344", {"start": v(33.97, 353.93) * mm, "end": v(34.14, 354.07) * mm});
            skLineSegment(sketch, "E345", {"start": v(34.14, 354.07) * mm, "end": v(34.31, 354.2) * mm});
            skLineSegment(sketch, "E346", {"start": v(34.31, 354.2) * mm, "end": v(34.51, 354.32) * mm});
            skLineSegment(sketch, "E347", {"start": v(34.51, 354.32) * mm, "end": v(34.71, 354.4) * mm});
            skLineSegment(sketch, "E348", {"start": v(34.71, 354.4) * mm, "end": v(34.9, 354.46) * mm});
            skLineSegment(sketch, "E349", {"start": v(34.9, 354.46) * mm, "end": v(35.1, 354.52) * mm});
            skLineSegment(sketch, "E350", {"start": v(35.1, 354.52) * mm, "end": v(35.34, 354.55) * mm});
            skLineSegment(sketch, "E351", {"start": v(35.34, 354.55) * mm, "end": v(35.56, 354.58) * mm});
            skLineSegment(sketch, "E352", {"start": v(35.56, 354.58) * mm, "end": v(35.76, 354.55) * mm});
            skLineSegment(sketch, "E353", {"start": v(35.76, 354.55) * mm, "end": v(35.99, 354.52) * mm});
            skLineSegment(sketch, "E354", {"start": v(35.99, 354.52) * mm, "end": v(36.19, 354.46) * mm});
            skLineSegment(sketch, "E355", {"start": v(36.19, 354.46) * mm, "end": v(36.39, 354.4) * mm});
            skLineSegment(sketch, "E356", {"start": v(36.39, 354.4) * mm, "end": v(36.59, 354.32) * mm});
            skLineSegment(sketch, "E357", {"start": v(36.59, 354.32) * mm, "end": v(36.78, 354.2) * mm});
            skLineSegment(sketch, "E358", {"start": v(36.78, 354.2) * mm, "end": v(36.95, 354.07) * mm});
            skLineSegment(sketch, "E359", {"start": v(36.95, 354.07) * mm, "end": v(37.13, 353.93) * mm});
            skLineSegment(sketch, "E360", {"start": v(37.13, 353.93) * mm, "end": v(37.27, 353.75) * mm});
            skLineSegment(sketch, "E361", {"start": v(37.27, 353.75) * mm, "end": v(37.4, 353.58) * mm});
            skLineSegment(sketch, "E362", {"start": v(37.4, 353.58) * mm, "end": v(37.52, 353.39) * mm});
            skLineSegment(sketch, "E363", {"start": v(37.52, 353.39) * mm, "end": v(37.6, 353.19) * mm});
            skLineSegment(sketch, "E364", {"start": v(37.6, 353.19) * mm, "end": v(37.66, 352.99) * mm});
            skLineSegment(sketch, "E365", {"start": v(37.66, 352.99) * mm, "end": v(37.72, 352.79) * mm});
            skLineSegment(sketch, "E366", {"start": v(37.72, 352.79) * mm, "end": v(37.75, 352.56) * mm});
            skLineSegment(sketch, "E367", {"start": v(37.75, 352.56) * mm, "end": v(37.78, 352.36) * mm});
            skLineSegment(sketch, "E368", {"start": v(37.78, 352.36) * mm, "end": v(37.78, 329.07) * mm});
            skLineSegment(sketch, "E369", {"start": v(37.78, 329.07) * mm, "end": v(37.75, 328.87) * mm});
            skLineSegment(sketch, "E370", {"start": v(37.75, 328.87) * mm, "end": v(37.72, 328.64) * mm});
            skLineSegment(sketch, "E371", {"start": v(37.72, 328.64) * mm, "end": v(37.66, 328.44) * mm});
            skLineSegment(sketch, "E372", {"start": v(37.66, 328.44) * mm, "end": v(37.6, 328.24) * mm});
            skLineSegment(sketch, "E373", {"start": v(37.6, 328.24) * mm, "end": v(37.52, 328.04) * mm});
            skLineSegment(sketch, "E374", {"start": v(37.52, 328.04) * mm, "end": v(37.4, 327.84) * mm});
            skLineSegment(sketch, "E375", {"start": v(37.4, 327.84) * mm, "end": v(37.27, 327.67) * mm});
            skLineSegment(sketch, "E376", {"start": v(37.27, 327.67) * mm, "end": v(37.13, 327.5) * mm});
            skLineSegment(sketch, "E377", {"start": v(37.13, 327.5) * mm, "end": v(36.95, 327.36) * mm});
            skLineSegment(sketch, "E378", {"start": v(36.95, 327.36) * mm, "end": v(36.78, 327.22) * mm});
            skLineSegment(sketch, "E379", {"start": v(36.78, 327.22) * mm, "end": v(36.59, 327.1) * mm});
            skLineSegment(sketch, "E380", {"start": v(36.59, 327.1) * mm, "end": v(36.39, 327.02) * mm});
            skLineSegment(sketch, "E381", {"start": v(36.39, 327.02) * mm, "end": v(36.19, 326.96) * mm});
            skLineSegment(sketch, "E382", {"start": v(36.19, 326.96) * mm, "end": v(35.99, 326.9) * mm});
            skLineSegment(sketch, "E383", {"start": v(35.99, 326.9) * mm, "end": v(35.76, 326.88) * mm});
            skLineSegment(sketch, "E384", {"start": v(35.76, 326.88) * mm, "end": v(35.56, 326.85) * mm});
            skLineSegment(sketch, "E385", {"start": v(35.56, 326.85) * mm, "end": v(29.45, 326.85) * mm});
            skLineSegment(sketch, "E386", {"start": v(29.45, 326.85) * mm, "end": v(28.6, 326.9) * mm});
            skLineSegment(sketch, "E387", {"start": v(28.6, 326.9) * mm, "end": v(27.8, 327.02) * mm});
            skLineSegment(sketch, "E388", {"start": v(27.8, 327.02) * mm, "end": v(27.01, 327.22) * mm});
            skLineSegment(sketch, "E389", {"start": v(27.01, 327.22) * mm, "end": v(26.27, 327.48) * mm});
            skLineSegment(sketch, "E390", {"start": v(26.27, 327.48) * mm, "end": v(25.56, 327.82) * mm});
            skLineSegment(sketch, "E391", {"start": v(25.56, 327.82) * mm, "end": v(24.85, 328.24) * mm});
            skLineSegment(sketch, "E392", {"start": v(24.85, 328.24) * mm, "end": v(24.2, 328.73) * mm});
            skLineSegment(sketch, "E393", {"start": v(24.2, 328.73) * mm, "end": v(23.57, 329.3) * mm});
            skLineSegment(sketch, "E394", {"start": v(23.57, 329.3) * mm, "end": v(23, 329.92) * mm});
            skLineSegment(sketch, "E395", {"start": v(23, 329.92) * mm, "end": v(22.52, 330.57) * mm});
            skLineSegment(sketch, "E396", {"start": v(22.52, 330.57) * mm, "end": v(22.1, 331.28) * mm});
            skLineSegment(sketch, "E397", {"start": v(22.1, 331.28) * mm, "end": v(21.76, 332) * mm});
            skLineSegment(sketch, "E398", {"start": v(21.76, 332) * mm, "end": v(21.5, 332.73) * mm});
            skLineSegment(sketch, "E399", {"start": v(21.5, 332.73) * mm, "end": v(21.3, 333.53) * mm});
            skLineSegment(sketch, "E400", {"start": v(21.3, 333.53) * mm, "end": v(21.19, 334.32) * mm});
            skLineSegment(sketch, "E401", {"start": v(44.45, 338.27) * mm, "end": v(44.57, 339.07) * mm});
            skLineSegment(sketch, "E402", {"start": v(44.57, 339.07) * mm, "end": v(44.77, 339.86) * mm});
            skLineSegment(sketch, "E403", {"start": v(44.77, 339.86) * mm, "end": v(45.02, 340.6) * mm});
            skLineSegment(sketch, "E404", {"start": v(45.02, 340.6) * mm, "end": v(45.4, 341.31) * mm});
            skLineSegment(sketch, "E405", {"start": v(45.4, 341.31) * mm, "end": v(45.8, 342.02) * mm});
            skLineSegment(sketch, "E406", {"start": v(45.8, 342.02) * mm, "end": v(46.3, 342.67) * mm});
            skLineSegment(sketch, "E407", {"start": v(46.3, 342.67) * mm, "end": v(46.87, 343.3) * mm});
            skLineSegment(sketch, "E408", {"start": v(46.87, 343.3) * mm, "end": v(47.4, 343.81) * mm});
            skLineSegment(sketch, "E409", {"start": v(47.4, 343.81) * mm, "end": v(48, 344.24) * mm});
            skLineSegment(sketch, "E410", {"start": v(48, 344.24) * mm, "end": v(48.6, 344.64) * mm});
            skLineSegment(sketch, "E411", {"start": v(48.6, 344.64) * mm, "end": v(49.23, 344.98) * mm});
            skLineSegment(sketch, "E412", {"start": v(49.23, 344.98) * mm, "end": v(49.88, 345.23) * mm});
            skLineSegment(sketch, "E413", {"start": v(49.88, 345.23) * mm, "end": v(50.56, 345.46) * mm});
            skLineSegment(sketch, "E414", {"start": v(50.56, 345.46) * mm, "end": v(51.27, 345.6) * mm});
            skLineSegment(sketch, "E415", {"start": v(51.27, 345.6) * mm, "end": v(51.98, 345.71) * mm});
            skLineSegment(sketch, "E416", {"start": v(51.98, 345.71) * mm, "end": v(52.27, 345.69) * mm});
            skLineSegment(sketch, "E417", {"start": v(52.27, 345.69) * mm, "end": v(52.52, 345.66) * mm});
            skLineSegment(sketch, "E418", {"start": v(52.52, 345.66) * mm, "end": v(52.75, 345.6) * mm});
            skLineSegment(sketch, "E419", {"start": v(52.75, 345.6) * mm, "end": v(52.98, 345.54) * mm});
            skLineSegment(sketch, "E420", {"start": v(52.98, 345.54) * mm, "end": v(53.2, 345.43) * mm});
            skLineSegment(sketch, "E421", {"start": v(53.2, 345.43) * mm, "end": v(53.4, 345.32) * mm});
            skLineSegment(sketch, "E422", {"start": v(53.4, 345.32) * mm, "end": v(53.57, 345.2) * mm});
            skLineSegment(sketch, "E423", {"start": v(53.57, 345.2) * mm, "end": v(53.74, 345.03) * mm});
            skLineSegment(sketch, "E424", {"start": v(53.74, 345.03) * mm, "end": v(53.89, 344.86) * mm});
            skLineSegment(sketch, "E425", {"start": v(53.89, 344.86) * mm, "end": v(54.03, 344.7) * mm});
            skLineSegment(sketch, "E426", {"start": v(54.03, 344.7) * mm, "end": v(54.14, 344.5) * mm});
            skLineSegment(sketch, "E427", {"start": v(54.14, 344.5) * mm, "end": v(54.23, 344.32) * mm});
            skLineSegment(sketch, "E428", {"start": v(54.23, 344.32) * mm, "end": v(54.31, 344.12) * mm});
            skLineSegment(sketch, "E429", {"start": v(54.31, 344.12) * mm, "end": v(54.37, 343.92) * mm});
            skLineSegment(sketch, "E430", {"start": v(54.37, 343.92) * mm, "end": v(54.4, 343.7) * mm});
            skLineSegment(sketch, "E431", {"start": v(54.4, 343.7) * mm, "end": v(54.4, 343.5) * mm});
            skLineSegment(sketch, "E432", {"start": v(54.4, 343.5) * mm, "end": v(54.4, 343.27) * mm});
            skLineSegment(sketch, "E433", {"start": v(54.4, 343.27) * mm, "end": v(54.37, 343.04) * mm});
            skLineSegment(sketch, "E434", {"start": v(54.37, 343.04) * mm, "end": v(54.31, 342.85) * mm});
            skLineSegment(sketch, "E435", {"start": v(54.31, 342.85) * mm, "end": v(54.23, 342.65) * mm});
            skLineSegment(sketch, "E436", {"start": v(54.23, 342.65) * mm, "end": v(54.14, 342.45) * mm});
            skLineSegment(sketch, "E437", {"start": v(54.14, 342.45) * mm, "end": v(54.03, 342.28) * mm});
            skLineSegment(sketch, "E438", {"start": v(54.03, 342.28) * mm, "end": v(53.92, 342.1) * mm});
            skLineSegment(sketch, "E439", {"start": v(53.92, 342.1) * mm, "end": v(53.77, 341.94) * mm});
            skLineSegment(sketch, "E440", {"start": v(53.77, 341.94) * mm, "end": v(53.6, 341.8) * mm});
            skLineSegment(sketch, "E441", {"start": v(53.6, 341.8) * mm, "end": v(53.46, 341.68) * mm});
            skLineSegment(sketch, "E442", {"start": v(53.46, 341.68) * mm, "end": v(53.3, 341.57) * mm});
            skLineSegment(sketch, "E443", {"start": v(53.3, 341.57) * mm, "end": v(53.12, 341.48) * mm});
            skLineSegment(sketch, "E444", {"start": v(53.12, 341.48) * mm, "end": v(52.95, 341.4) * mm});
            skLineSegment(sketch, "E445", {"start": v(52.95, 341.4) * mm, "end": v(52.78, 341.34) * mm});
            skLineSegment(sketch, "E446", {"start": v(52.78, 341.34) * mm, "end": v(52.6, 341.31) * mm});
            skLineSegment(sketch, "E447", {"start": v(52.6, 341.31) * mm, "end": v(52.4, 341.28) * mm});
            skLineSegment(sketch, "E448", {"start": v(52.4, 341.28) * mm, "end": v(52.07, 341.23) * mm});
            skLineSegment(sketch, "E449", {"start": v(52.07, 341.23) * mm, "end": v(51.73, 341.17) * mm});
            skLineSegment(sketch, "E450", {"start": v(51.73, 341.17) * mm, "end": v(51.42, 341.08) * mm});
            skLineSegment(sketch, "E451", {"start": v(51.42, 341.08) * mm, "end": v(51.1, 340.94) * mm});
            skLineSegment(sketch, "E452", {"start": v(51.1, 340.94) * mm, "end": v(50.82, 340.8) * mm});
            skLineSegment(sketch, "E453", {"start": v(50.82, 340.8) * mm, "end": v(50.53, 340.6) * mm});
            skLineSegment(sketch, "E454", {"start": v(50.53, 340.6) * mm, "end": v(50.25, 340.4) * mm});
            skLineSegment(sketch, "E455", {"start": v(50.25, 340.4) * mm, "end": v(50, 340.15) * mm});
            skLineSegment(sketch, "E456", {"start": v(50, 340.15) * mm, "end": v(49.74, 339.86) * mm});
            skLineSegment(sketch, "E457", {"start": v(49.74, 339.86) * mm, "end": v(49.48, 339.55) * mm});
            skLineSegment(sketch, "E458", {"start": v(49.48, 339.55) * mm, "end": v(49.31, 339.24) * mm});
            skLineSegment(sketch, "E459", {"start": v(49.31, 339.24) * mm, "end": v(49.14, 338.9) * mm});
            skLineSegment(sketch, "E460", {"start": v(49.14, 338.9) * mm, "end": v(49.03, 338.56) * mm});
            skLineSegment(sketch, "E461", {"start": v(49.03, 338.56) * mm, "end": v(48.92, 338.19) * mm});
            skLineSegment(sketch, "E462", {"start": v(48.92, 338.19) * mm, "end": v(48.89, 337.82) * mm});
            skLineSegment(sketch, "E463", {"start": v(48.89, 337.82) * mm, "end": v(48.86, 337.42) * mm});
            skLineSegment(sketch, "E464", {"start": v(48.86, 337.42) * mm, "end": v(48.86, 335.17) * mm});
            skLineSegment(sketch, "E465", {"start": v(48.86, 335.17) * mm, "end": v(48.89, 334.78) * mm});
            skLineSegment(sketch, "E466", {"start": v(48.89, 334.78) * mm, "end": v(48.92, 334.4) * mm});
            skLineSegment(sketch, "E467", {"start": v(48.92, 334.4) * mm, "end": v(49.03, 334.04) * mm});
            skLineSegment(sketch, "E468", {"start": v(49.03, 334.04) * mm, "end": v(49.14, 333.7) * mm});
            skLineSegment(sketch, "E469", {"start": v(49.14, 333.7) * mm, "end": v(49.31, 333.36) * mm});
            skLineSegment(sketch, "E470", {"start": v(49.31, 333.36) * mm, "end": v(49.48, 333.04) * mm});
            skLineSegment(sketch, "E471", {"start": v(49.48, 333.04) * mm, "end": v(49.74, 332.73) * mm});
            skLineSegment(sketch, "E472", {"start": v(49.74, 332.73) * mm, "end": v(50, 332.42) * mm});
            skLineSegment(sketch, "E473", {"start": v(50, 332.42) * mm, "end": v(50.28, 332.16) * mm});
            skLineSegment(sketch, "E474", {"start": v(50.28, 332.16) * mm, "end": v(50.6, 331.94) * mm});
            skLineSegment(sketch, "E475", {"start": v(50.6, 331.94) * mm, "end": v(50.9, 331.74) * mm});
            skLineSegment(sketch, "E476", {"start": v(50.9, 331.74) * mm, "end": v(51.24, 331.57) * mm});
            skLineSegment(sketch, "E477", {"start": v(51.24, 331.57) * mm, "end": v(51.59, 331.45) * mm});
            skLineSegment(sketch, "E478", {"start": v(51.59, 331.45) * mm, "end": v(51.96, 331.37) * mm});
            skLineSegment(sketch, "E479", {"start": v(51.96, 331.37) * mm, "end": v(52.35, 331.31) * mm});
            skLineSegment(sketch, "E480", {"start": v(52.35, 331.31) * mm, "end": v(52.75, 331.28) * mm});
            skLineSegment(sketch, "E481", {"start": v(52.75, 331.28) * mm, "end": v(56.61, 331.28) * mm});
            skLineSegment(sketch, "E482", {"start": v(56.61, 331.28) * mm, "end": v(56.61, 346.8) * mm});
            skLineSegment(sketch, "E483", {"start": v(56.61, 346.8) * mm, "end": v(56.59, 347.16) * mm});
            skLineSegment(sketch, "E484", {"start": v(56.59, 347.16) * mm, "end": v(56.53, 347.56) * mm});
            skLineSegment(sketch, "E485", {"start": v(56.53, 347.56) * mm, "end": v(56.44, 347.93) * mm});
            skLineSegment(sketch, "E486", {"start": v(56.44, 347.93) * mm, "end": v(56.3, 348.27) * mm});
            skLineSegment(sketch, "E487", {"start": v(56.3, 348.27) * mm, "end": v(56.16, 348.61) * mm});
            skLineSegment(sketch, "E488", {"start": v(56.16, 348.61) * mm, "end": v(55.96, 348.93) * mm});
            skLineSegment(sketch, "E489", {"start": v(55.96, 348.93) * mm, "end": v(55.73, 349.24) * mm});
            skLineSegment(sketch, "E490", {"start": v(55.73, 349.24) * mm, "end": v(55.48, 349.52) * mm});
            skLineSegment(sketch, "E491", {"start": v(55.48, 349.52) * mm, "end": v(55.17, 349.78) * mm});
            skLineSegment(sketch, "E492", {"start": v(55.17, 349.78) * mm, "end": v(54.88, 350.03) * mm});
            skLineSegment(sketch, "E493", {"start": v(54.88, 350.03) * mm, "end": v(54.54, 350.2) * mm});
            skLineSegment(sketch, "E494", {"start": v(54.54, 350.2) * mm, "end": v(54.23, 350.37) * mm});
            skLineSegment(sketch, "E495", {"start": v(54.23, 350.37) * mm, "end": v(53.86, 350.49) * mm});
            skLineSegment(sketch, "E496", {"start": v(53.86, 350.49) * mm, "end": v(53.49, 350.6) * mm});
            skLineSegment(sketch, "E497", {"start": v(53.49, 350.6) * mm, "end": v(53.12, 350.63) * mm});
            skLineSegment(sketch, "E498", {"start": v(53.12, 350.63) * mm, "end": v(52.72, 350.66) * mm});
            skLineSegment(sketch, "E499", {"start": v(52.72, 350.66) * mm, "end": v(52.32, 350.63) * mm});
            skLineSegment(sketch, "E500", {"start": v(52.32, 350.63) * mm, "end": v(51.93, 350.57) * mm});
            skLineSegment(sketch, "E501", {"start": v(51.93, 350.57) * mm, "end": v(51.56, 350.49) * mm});
            skLineSegment(sketch, "E502", {"start": v(51.56, 350.49) * mm, "end": v(51.22, 350.37) * mm});
            skLineSegment(sketch, "E503", {"start": v(51.22, 350.37) * mm, "end": v(50.88, 350.2) * mm});
            skLineSegment(sketch, "E504", {"start": v(50.88, 350.2) * mm, "end": v(50.53, 350) * mm});
            skLineSegment(sketch, "E505", {"start": v(50.53, 350) * mm, "end": v(50.22, 349.78) * mm});
            skLineSegment(sketch, "E506", {"start": v(50.22, 349.78) * mm, "end": v(49.9, 349.5) * mm});
            skLineSegment(sketch, "E507", {"start": v(49.77, 349.35) * mm, "end": v(49.6, 349.2) * mm});
            skLineSegment(sketch, "E508", {"start": v(49.6, 349.2) * mm, "end": v(49.4, 349.1) * mm});
            skLineSegment(sketch, "E509", {"start": v(49.4, 349.1) * mm, "end": v(49.23, 349.01) * mm});
            skLineSegment(sketch, "E510", {"start": v(49.23, 349.01) * mm, "end": v(49.03, 348.93) * mm});
            skLineSegment(sketch, "E511", {"start": v(49.03, 348.93) * mm, "end": v(48.8, 348.87) * mm});
            skLineSegment(sketch, "E512", {"start": v(48.8, 348.87) * mm, "end": v(48.6, 348.84) * mm});
            skLineSegment(sketch, "E513", {"start": v(48.6, 348.84) * mm, "end": v(48.35, 348.84) * mm});
            skLineSegment(sketch, "E514", {"start": v(48.35, 348.84) * mm, "end": v(48.15, 348.84) * mm});
            skLineSegment(sketch, "E515", {"start": v(48.15, 348.84) * mm, "end": v(47.92, 348.87) * mm});
            skLineSegment(sketch, "E516", {"start": v(47.92, 348.87) * mm, "end": v(47.72, 348.93) * mm});
            skLineSegment(sketch, "E517", {"start": v(47.72, 348.93) * mm, "end": v(47.52, 348.98) * mm});
            skLineSegment(sketch, "E518", {"start": v(47.52, 348.98) * mm, "end": v(47.32, 349.1) * mm});
            skLineSegment(sketch, "E519", {"start": v(47.32, 349.1) * mm, "end": v(47.13, 349.2) * mm});
            skLineSegment(sketch, "E520", {"start": v(47.13, 349.2) * mm, "end": v(46.95, 349.32) * mm});
            skLineSegment(sketch, "E521", {"start": v(46.95, 349.32) * mm, "end": v(46.78, 349.5) * mm});
            skLineSegment(sketch, "E522", {"start": v(46.78, 349.5) * mm, "end": v(46.64, 349.64) * mm});
            skLineSegment(sketch, "E523", {"start": v(46.64, 349.64) * mm, "end": v(46.5, 349.83) * mm});
            skLineSegment(sketch, "E524", {"start": v(46.5, 349.83) * mm, "end": v(46.39, 350) * mm});
            skLineSegment(sketch, "E525", {"start": v(46.39, 350) * mm, "end": v(46.3, 350.2) * mm});
            skLineSegment(sketch, "E526", {"start": v(46.3, 350.2) * mm, "end": v(46.24, 350.4) * mm});
            skLineSegment(sketch, "E527", {"start": v(46.24, 350.4) * mm, "end": v(46.19, 350.6) * mm});
            skLineSegment(sketch, "E528", {"start": v(46.19, 350.6) * mm, "end": v(46.16, 350.83) * mm});
            skLineSegment(sketch, "E529", {"start": v(46.16, 350.83) * mm, "end": v(46.13, 351.06) * mm});
            skLineSegment(sketch, "E530", {"start": v(46.13, 351.06) * mm, "end": v(46.16, 351.25) * mm});
            skLineSegment(sketch, "E531", {"start": v(46.16, 351.25) * mm, "end": v(46.19, 351.48) * mm});
            skLineSegment(sketch, "E532", {"start": v(46.19, 351.48) * mm, "end": v(46.24, 351.68) * mm});
            skLineSegment(sketch, "E533", {"start": v(46.24, 351.68) * mm, "end": v(46.3, 351.88) * mm});
            skLineSegment(sketch, "E534", {"start": v(46.3, 351.88) * mm, "end": v(46.39, 352.08) * mm});
            skLineSegment(sketch, "E535", {"start": v(46.39, 352.08) * mm, "end": v(46.5, 352.25) * mm});
            skLineSegment(sketch, "E536", {"start": v(46.5, 352.25) * mm, "end": v(46.64, 352.42) * mm});
            skLineSegment(sketch, "E537", {"start": v(46.64, 352.42) * mm, "end": v(46.78, 352.59) * mm});
            skLineSegment(sketch, "E538", {"start": v(46.78, 352.59) * mm, "end": v(47.4, 353.19) * mm});
            skLineSegment(sketch, "E539", {"start": v(47.4, 353.19) * mm, "end": v(48.1, 353.7) * mm});
            skLineSegment(sketch, "E540", {"start": v(48.1, 353.7) * mm, "end": v(48.77, 354.12) * mm});
            skLineSegment(sketch, "E541", {"start": v(48.77, 354.12) * mm, "end": v(49.51, 354.5) * mm});
            skLineSegment(sketch, "E542", {"start": v(49.51, 354.5) * mm, "end": v(50.28, 354.78) * mm});
            skLineSegment(sketch, "E543", {"start": v(50.28, 354.78) * mm, "end": v(51.05, 354.95) * mm});
            skLineSegment(sketch, "E544", {"start": v(51.05, 354.95) * mm, "end": v(51.87, 355.09) * mm});
            skLineSegment(sketch, "E545", {"start": v(51.87, 355.09) * mm, "end": v(52.72, 355.12) * mm});
            skLineSegment(sketch, "E546", {"start": v(52.72, 355.12) * mm, "end": v(53.55, 355.09) * mm});
            skLineSegment(sketch, "E547", {"start": v(53.55, 355.09) * mm, "end": v(54.37, 354.98) * mm});
            skLineSegment(sketch, "E548", {"start": v(54.37, 354.98) * mm, "end": v(55.14, 354.78) * mm});
            skLineSegment(sketch, "E549", {"start": v(55.14, 354.78) * mm, "end": v(55.9, 354.52) * mm});
            skLineSegment(sketch, "E550", {"start": v(55.9, 354.52) * mm, "end": v(56.61, 354.15) * mm});
            skLineSegment(sketch, "E551", {"start": v(56.61, 354.15) * mm, "end": v(57.3, 353.75) * mm});
            skLineSegment(sketch, "E552", {"start": v(57.3, 353.75) * mm, "end": v(57.95, 353.24) * mm});
            skLineSegment(sketch, "E553", {"start": v(57.95, 353.24) * mm, "end": v(58.57, 352.68) * mm});
            skLineSegment(sketch, "E554", {"start": v(58.57, 352.68) * mm, "end": v(59.14, 352.05) * mm});
            skLineSegment(sketch, "E555", {"start": v(59.14, 352.05) * mm, "end": v(59.65, 351.4) * mm});
            skLineSegment(sketch, "E556", {"start": v(59.65, 351.4) * mm, "end": v(60.08, 350.71) * mm});
            skLineSegment(sketch, "E557", {"start": v(60.08, 350.71) * mm, "end": v(60.42, 349.98) * mm});
            skLineSegment(sketch, "E558", {"start": v(60.42, 349.98) * mm, "end": v(60.68, 349.24) * mm});
            skLineSegment(sketch, "E559", {"start": v(60.68, 349.24) * mm, "end": v(60.88, 348.44) * mm});
            skLineSegment(sketch, "E560", {"start": v(60.88, 348.44) * mm, "end": v(60.99, 347.62) * mm});
            skLineSegment(sketch, "E561", {"start": v(60.99, 347.62) * mm, "end": v(61.05, 346.8) * mm});
            skLineSegment(sketch, "E562", {"start": v(61.05, 346.8) * mm, "end": v(61.05, 329.07) * mm});
            skLineSegment(sketch, "E563", {"start": v(61.05, 329.07) * mm, "end": v(61.05, 328.87) * mm});
            skLineSegment(sketch, "E564", {"start": v(61.05, 328.87) * mm, "end": v(61.02, 328.64) * mm});
            skLineSegment(sketch, "E565", {"start": v(61.02, 328.64) * mm, "end": v(60.96, 328.44) * mm});
            skLineSegment(sketch, "E566", {"start": v(60.96, 328.44) * mm, "end": v(60.88, 328.24) * mm});
            skLineSegment(sketch, "E567", {"start": v(60.88, 328.24) * mm, "end": v(60.8, 328.04) * mm});
            skLineSegment(sketch, "E568", {"start": v(60.8, 328.04) * mm, "end": v(60.68, 327.84) * mm});
            skLineSegment(sketch, "E569", {"start": v(60.68, 327.84) * mm, "end": v(60.53, 327.67) * mm});
            skLineSegment(sketch, "E570", {"start": v(60.53, 327.67) * mm, "end": v(60.4, 327.5) * mm});
            skLineSegment(sketch, "E571", {"start": v(60.4, 327.5) * mm, "end": v(60.22, 327.36) * mm});
            skLineSegment(sketch, "E572", {"start": v(60.22, 327.36) * mm, "end": v(60.05, 327.22) * mm});
            skLineSegment(sketch, "E573", {"start": v(60.05, 327.22) * mm, "end": v(59.88, 327.1) * mm});
            skLineSegment(sketch, "E574", {"start": v(59.88, 327.1) * mm, "end": v(59.68, 327.02) * mm});
            skLineSegment(sketch, "E575", {"start": v(59.68, 327.02) * mm, "end": v(59.48, 326.96) * mm});
            skLineSegment(sketch, "E576", {"start": v(59.48, 326.96) * mm, "end": v(59.28, 326.9) * mm});
            skLineSegment(sketch, "E577", {"start": v(59.28, 326.9) * mm, "end": v(59.06, 326.88) * mm});
            skLineSegment(sketch, "E578", {"start": v(59.06, 326.88) * mm, "end": v(58.83, 326.85) * mm});
            skLineSegment(sketch, "E579", {"start": v(58.83, 326.85) * mm, "end": v(52.75, 326.85) * mm});
            skLineSegment(sketch, "E580", {"start": v(52.75, 326.85) * mm, "end": v(51.9, 326.9) * mm});
            skLineSegment(sketch, "E581", {"start": v(51.9, 326.9) * mm, "end": v(51.07, 327.02) * mm});
            skLineSegment(sketch, "E582", {"start": v(51.07, 327.02) * mm, "end": v(50.3, 327.22) * mm});
            skLineSegment(sketch, "E583", {"start": v(50.3, 327.22) * mm, "end": v(49.54, 327.48) * mm});
            skLineSegment(sketch, "E584", {"start": v(49.54, 327.48) * mm, "end": v(48.83, 327.82) * mm});
            skLineSegment(sketch, "E585", {"start": v(48.83, 327.82) * mm, "end": v(48.15, 328.24) * mm});
            skLineSegment(sketch, "E586", {"start": v(48.15, 328.24) * mm, "end": v(47.5, 328.73) * mm});
            skLineSegment(sketch, "E587", {"start": v(47.5, 328.73) * mm, "end": v(46.87, 329.3) * mm});
            skLineSegment(sketch, "E588", {"start": v(46.87, 329.3) * mm, "end": v(46.3, 329.92) * mm});
            skLineSegment(sketch, "E589", {"start": v(46.3, 329.92) * mm, "end": v(45.8, 330.57) * mm});
            skLineSegment(sketch, "E590", {"start": v(45.8, 330.57) * mm, "end": v(45.4, 331.28) * mm});
            skLineSegment(sketch, "E591", {"start": v(45.4, 331.28) * mm, "end": v(45.02, 332) * mm});
            skLineSegment(sketch, "E592", {"start": v(45.02, 332) * mm, "end": v(44.77, 332.73) * mm});
            skLineSegment(sketch, "E593", {"start": v(44.77, 332.73) * mm, "end": v(44.57, 333.53) * mm});
            skLineSegment(sketch, "E594", {"start": v(44.57, 333.53) * mm, "end": v(44.45, 334.32) * mm});
            skLineSegment(sketch, "E595", {"start": v(44.45, 334.32) * mm, "end": v(44.43, 335.17) * mm});
            skLineSegment(sketch, "E596", {"start": v(44.43, 335.17) * mm, "end": v(44.43, 337.42) * mm});
            skLineSegment(sketch, "E597", {"start": v(44.43, 337.42) * mm, "end": v(44.45, 338.27) * mm});
            skLineSegment(sketch, "E598", {"start": v(67.18, 328.64) * mm, "end": v(67.15, 328.87) * mm});
            skLineSegment(sketch, "E599", {"start": v(67.15, 328.87) * mm, "end": v(67.15, 329.07) * mm});
            skLineSegment(sketch, "E600", {"start": v(67.15, 329.07) * mm, "end": v(67.15, 352.36) * mm});
            skLineSegment(sketch, "E601", {"start": v(67.15, 352.36) * mm, "end": v(67.15, 352.56) * mm});
            skLineSegment(sketch, "E602", {"start": v(67.15, 352.56) * mm, "end": v(67.18, 352.79) * mm});
            skLineSegment(sketch, "E603", {"start": v(67.18, 352.79) * mm, "end": v(67.24, 352.99) * mm});
            skLineSegment(sketch, "E604", {"start": v(67.24, 352.99) * mm, "end": v(67.32, 353.19) * mm});
            skLineSegment(sketch, "E605", {"start": v(67.32, 353.19) * mm, "end": v(67.41, 353.39) * mm});
            skLineSegment(sketch, "E606", {"start": v(67.41, 353.39) * mm, "end": v(67.52, 353.58) * mm});
            skLineSegment(sketch, "E607", {"start": v(67.52, 353.58) * mm, "end": v(67.67, 353.75) * mm});
            skLineSegment(sketch, "E608", {"start": v(67.67, 353.75) * mm, "end": v(67.8, 353.93) * mm});
            skLineSegment(sketch, "E609", {"start": v(67.8, 353.93) * mm, "end": v(67.98, 354.07) * mm});
            skLineSegment(sketch, "E610", {"start": v(67.98, 354.07) * mm, "end": v(68.15, 354.2) * mm});
            skLineSegment(sketch, "E611", {"start": v(68.15, 354.2) * mm, "end": v(68.32, 354.32) * mm});
            skLineSegment(sketch, "E612", {"start": v(68.32, 354.32) * mm, "end": v(68.52, 354.4) * mm});
            skLineSegment(sketch, "E613", {"start": v(68.52, 354.4) * mm, "end": v(68.72, 354.46) * mm});
            skLineSegment(sketch, "E614", {"start": v(68.72, 354.46) * mm, "end": v(68.92, 354.52) * mm});
            skLineSegment(sketch, "E615", {"start": v(68.92, 354.52) * mm, "end": v(69.14, 354.55) * mm});
            skLineSegment(sketch, "E616", {"start": v(69.14, 354.55) * mm, "end": v(69.37, 354.58) * mm});
            skLineSegment(sketch, "E617", {"start": v(69.37, 354.58) * mm, "end": v(75.45, 354.58) * mm});
            skLineSegment(sketch, "E618", {"start": v(75.45, 354.58) * mm, "end": v(76.3, 354.52) * mm});
            skLineSegment(sketch, "E619", {"start": v(76.3, 354.52) * mm, "end": v(77.13, 354.4) * mm});
            skLineSegment(sketch, "E620", {"start": v(77.13, 354.4) * mm, "end": v(77.9, 354.2) * mm});
            skLineSegment(sketch, "E621", {"start": v(77.9, 354.2) * mm, "end": v(78.66, 353.95) * mm});
            skLineSegment(sketch, "E622", {"start": v(78.66, 353.95) * mm, "end": v(79.37, 353.61) * mm});
            skLineSegment(sketch, "E623", {"start": v(79.37, 353.61) * mm, "end": v(80.05, 353.19) * mm});
            skLineSegment(sketch, "E624", {"start": v(80.05, 353.19) * mm, "end": v(80.7, 352.7) * mm});
            skLineSegment(sketch, "E625", {"start": v(80.7, 352.7) * mm, "end": v(81.33, 352.14) * mm});
            skLineSegment(sketch, "E626", {"start": v(81.33, 352.14) * mm, "end": v(81.9, 351.51) * mm});
            skLineSegment(sketch, "E627", {"start": v(81.9, 351.51) * mm, "end": v(82.41, 350.86) * mm});
            skLineSegment(sketch, "E628", {"start": v(82.41, 350.86) * mm, "end": v(82.8, 350.15) * mm});
            skLineSegment(sketch, "E629", {"start": v(82.8, 350.15) * mm, "end": v(83.18, 349.44) * mm});
            skLineSegment(sketch, "E630", {"start": v(83.18, 349.44) * mm, "end": v(83.43, 348.7) * mm});
            skLineSegment(sketch, "E631", {"start": v(83.43, 348.7) * mm, "end": v(83.63, 347.9) * mm});
            skLineSegment(sketch, "E632", {"start": v(83.63, 347.9) * mm, "end": v(83.75, 347.1) * mm});
            skLineSegment(sketch, "E633", {"start": v(83.75, 347.1) * mm, "end": v(83.77, 346.25) * mm});
            skLineSegment(sketch, "E634", {"start": v(83.77, 346.25) * mm, "end": v(83.77, 329.07) * mm});
            skLineSegment(sketch, "E635", {"start": v(83.77, 329.07) * mm, "end": v(83.77, 328.87) * mm});
            skLineSegment(sketch, "E636", {"start": v(83.77, 328.87) * mm, "end": v(83.75, 328.64) * mm});
            skLineSegment(sketch, "E637", {"start": v(83.75, 328.64) * mm, "end": v(83.69, 328.44) * mm});
            skLineSegment(sketch, "E638", {"start": v(83.69, 328.44) * mm, "end": v(83.6, 328.24) * mm});
            skLineSegment(sketch, "E639", {"start": v(83.6, 328.24) * mm, "end": v(83.52, 328.04) * mm});
            skLineSegment(sketch, "E640", {"start": v(83.52, 328.04) * mm, "end": v(83.4, 327.84) * mm});
            skLineSegment(sketch, "E641", {"start": v(83.4, 327.84) * mm, "end": v(83.26, 327.67) * mm});
            skLineSegment(sketch, "E642", {"start": v(83.26, 327.67) * mm, "end": v(83.12, 327.5) * mm});
            skLineSegment(sketch, "E643", {"start": v(83.12, 327.5) * mm, "end": v(82.95, 327.36) * mm});
            skLineSegment(sketch, "E644", {"start": v(82.95, 327.36) * mm, "end": v(82.78, 327.22) * mm});
            skLineSegment(sketch, "E645", {"start": v(82.78, 327.22) * mm, "end": v(82.6, 327.1) * mm});
            skLineSegment(sketch, "E646", {"start": v(82.6, 327.1) * mm, "end": v(82.41, 327.02) * mm});
            skLineSegment(sketch, "E647", {"start": v(82.41, 327.02) * mm, "end": v(82.21, 326.96) * mm});
            skLineSegment(sketch, "E648", {"start": v(82.21, 326.96) * mm, "end": v(82.01, 326.9) * mm});
            skLineSegment(sketch, "E649", {"start": v(82.01, 326.9) * mm, "end": v(81.79, 326.88) * mm});
            skLineSegment(sketch, "E650", {"start": v(81.79, 326.88) * mm, "end": v(81.56, 326.85) * mm});
            skLineSegment(sketch, "E651", {"start": v(81.56, 326.85) * mm, "end": v(81.33, 326.88) * mm});
            skLineSegment(sketch, "E652", {"start": v(81.33, 326.88) * mm, "end": v(81.1, 326.9) * mm});
            skLineSegment(sketch, "E653", {"start": v(81.1, 326.9) * mm, "end": v(80.9, 326.96) * mm});
            skLineSegment(sketch, "E654", {"start": v(80.9, 326.96) * mm, "end": v(80.7, 327.02) * mm});
            skLineSegment(sketch, "E655", {"start": v(80.7, 327.02) * mm, "end": v(80.5, 327.1) * mm});
            skLineSegment(sketch, "E656", {"start": v(80.5, 327.1) * mm, "end": v(80.34, 327.22) * mm});
            skLineSegment(sketch, "E657", {"start": v(80.34, 327.22) * mm, "end": v(80.17, 327.36) * mm});
            skLineSegment(sketch, "E658", {"start": v(80.17, 327.36) * mm, "end": v(80, 327.5) * mm});
            skLineSegment(sketch, "E659", {"start": v(80, 327.5) * mm, "end": v(79.85, 327.67) * mm});
            skLineSegment(sketch, "E660", {"start": v(79.85, 327.67) * mm, "end": v(79.71, 327.84) * mm});
            skLineSegment(sketch, "E661", {"start": v(79.71, 327.84) * mm, "end": v(79.6, 328.04) * mm});
            skLineSegment(sketch, "E662", {"start": v(79.6, 328.04) * mm, "end": v(79.51, 328.24) * mm});
            skLineSegment(sketch, "E663", {"start": v(79.51, 328.24) * mm, "end": v(79.43, 328.44) * mm});
            skLineSegment(sketch, "E664", {"start": v(79.43, 328.44) * mm, "end": v(79.37, 328.64) * mm});
            skLineSegment(sketch, "E665", {"start": v(79.37, 328.64) * mm, "end": v(79.34, 328.87) * mm});
            skLineSegment(sketch, "E666", {"start": v(79.34, 328.87) * mm, "end": v(79.34, 329.07) * mm});
            skLineSegment(sketch, "E667", {"start": v(79.34, 329.07) * mm, "end": v(79.34, 346.25) * mm});
            skLineSegment(sketch, "E668", {"start": v(79.34, 346.25) * mm, "end": v(79.31, 346.65) * mm});
            skLineSegment(sketch, "E669", {"start": v(79.31, 346.65) * mm, "end": v(79.29, 347.02) * mm});
            skLineSegment(sketch, "E670", {"start": v(79.29, 347.02) * mm, "end": v(79.17, 347.4) * mm});
            skLineSegment(sketch, "E671", {"start": v(79.17, 347.4) * mm, "end": v(79.06, 347.73) * mm});
            skLineSegment(sketch, "E672", {"start": v(79.06, 347.73) * mm, "end": v(78.89, 348.07) * mm});
            skLineSegment(sketch, "E673", {"start": v(78.89, 348.07) * mm, "end": v(78.72, 348.39) * mm});
            skLineSegment(sketch, "E674", {"start": v(78.72, 348.39) * mm, "end": v(78.46, 348.7) * mm});
            skLineSegment(sketch, "E675", {"start": v(78.46, 348.7) * mm, "end": v(78.2, 349.01) * mm});
            skLineSegment(sketch, "E676", {"start": v(78.2, 349.01) * mm, "end": v(77.92, 349.27) * mm});
            skLineSegment(sketch, "E677", {"start": v(77.92, 349.27) * mm, "end": v(77.6, 349.5) * mm});
            skLineSegment(sketch, "E678", {"start": v(77.6, 349.5) * mm, "end": v(77.3, 349.7) * mm});
            skLineSegment(sketch, "E679", {"start": v(77.3, 349.7) * mm, "end": v(76.96, 349.86) * mm});
            skLineSegment(sketch, "E680", {"start": v(76.96, 349.86) * mm, "end": v(76.61, 349.98) * mm});
            skLineSegment(sketch, "E681", {"start": v(76.61, 349.98) * mm, "end": v(76.25, 350.06) * mm});
            skLineSegment(sketch, "E682", {"start": v(76.25, 350.06) * mm, "end": v(75.85, 350.12) * mm});
            skLineSegment(sketch, "E683", {"start": v(75.85, 350.12) * mm, "end": v(75.45, 350.15) * mm});
            skLineSegment(sketch, "E684", {"start": v(75.45, 350.15) * mm, "end": v(71.59, 350.15) * mm});
            skLineSegment(sketch, "E685", {"start": v(71.59, 350.15) * mm, "end": v(71.59, 329.07) * mm});
            skLineSegment(sketch, "E686", {"start": v(71.59, 329.07) * mm, "end": v(71.59, 328.87) * mm});
            skLineSegment(sketch, "E687", {"start": v(71.59, 328.87) * mm, "end": v(71.56, 328.64) * mm});
            skLineSegment(sketch, "E688", {"start": v(71.56, 328.64) * mm, "end": v(71.5, 328.44) * mm});
            skLineSegment(sketch, "E689", {"start": v(71.5, 328.44) * mm, "end": v(71.42, 328.24) * mm});
            skLineSegment(sketch, "E690", {"start": v(71.42, 328.24) * mm, "end": v(71.33, 328.04) * mm});
            skLineSegment(sketch, "E691", {"start": v(71.33, 328.04) * mm, "end": v(71.22, 327.84) * mm});
            skLineSegment(sketch, "E692", {"start": v(71.22, 327.84) * mm, "end": v(71.07, 327.67) * mm});
            skLineSegment(sketch, "E693", {"start": v(71.07, 327.67) * mm, "end": v(70.93, 327.5) * mm});
            skLineSegment(sketch, "E694", {"start": v(70.93, 327.5) * mm, "end": v(70.76, 327.36) * mm});
            skLineSegment(sketch, "E695", {"start": v(70.76, 327.36) * mm, "end": v(70.6, 327.22) * mm});
            skLineSegment(sketch, "E696", {"start": v(70.6, 327.22) * mm, "end": v(70.42, 327.1) * mm});
            skLineSegment(sketch, "E697", {"start": v(70.42, 327.1) * mm, "end": v(70.22, 327.02) * mm});
            skLineSegment(sketch, "E698", {"start": v(70.22, 327.02) * mm, "end": v(70.02, 326.96) * mm});
            skLineSegment(sketch, "E699", {"start": v(70.02, 326.96) * mm, "end": v(69.82, 326.9) * mm});
            skLineSegment(sketch, "E700", {"start": v(69.82, 326.9) * mm, "end": v(69.6, 326.88) * mm});
            skLineSegment(sketch, "E701", {"start": v(69.6, 326.88) * mm, "end": v(69.37, 326.85) * mm});
            skLineSegment(sketch, "E702", {"start": v(69.37, 326.85) * mm, "end": v(69.14, 326.88) * mm});
            skLineSegment(sketch, "E703", {"start": v(69.14, 326.88) * mm, "end": v(68.92, 326.9) * mm});
            skLineSegment(sketch, "E704", {"start": v(68.92, 326.9) * mm, "end": v(68.72, 326.96) * mm});
            skLineSegment(sketch, "E705", {"start": v(68.72, 326.96) * mm, "end": v(68.52, 327.02) * mm});
            skLineSegment(sketch, "E706", {"start": v(68.52, 327.02) * mm, "end": v(68.32, 327.1) * mm});
            skLineSegment(sketch, "E707", {"start": v(68.32, 327.1) * mm, "end": v(68.15, 327.22) * mm});
            skLineSegment(sketch, "E708", {"start": v(68.15, 327.22) * mm, "end": v(67.98, 327.36) * mm});
            skLineSegment(sketch, "E709", {"start": v(67.98, 327.36) * mm, "end": v(67.8, 327.5) * mm});
            skLineSegment(sketch, "E710", {"start": v(67.8, 327.5) * mm, "end": v(67.67, 327.67) * mm});
            skLineSegment(sketch, "E711", {"start": v(67.67, 327.67) * mm, "end": v(67.52, 327.84) * mm});
            skLineSegment(sketch, "E712", {"start": v(67.52, 327.84) * mm, "end": v(67.41, 328.04) * mm});
            skLineSegment(sketch, "E713", {"start": v(67.41, 328.04) * mm, "end": v(67.32, 328.24) * mm});
            skLineSegment(sketch, "E714", {"start": v(67.32, 328.24) * mm, "end": v(67.24, 328.44) * mm});
            skLineSegment(sketch, "E715", {"start": v(67.24, 328.44) * mm, "end": v(67.18, 328.64) * mm});
            skLineSegment(sketch, "E716", {"start": v(89.34, 351.9) * mm, "end": v(89.31, 352.14) * mm});
            skLineSegment(sketch, "E717", {"start": v(89.31, 352.14) * mm, "end": v(89.31, 352.36) * mm});
            skLineSegment(sketch, "E718", {"start": v(89.31, 352.36) * mm, "end": v(89.31, 352.56) * mm});
            skLineSegment(sketch, "E719", {"start": v(89.31, 352.56) * mm, "end": v(89.34, 352.79) * mm});
            skLineSegment(sketch, "E720", {"start": v(89.34, 352.79) * mm, "end": v(89.4, 352.99) * mm});
            skLineSegment(sketch, "E721", {"start": v(89.4, 352.99) * mm, "end": v(89.46, 353.19) * mm});
            skLineSegment(sketch, "E722", {"start": v(89.46, 353.19) * mm, "end": v(89.57, 353.39) * mm});
            skLineSegment(sketch, "E723", {"start": v(89.57, 353.39) * mm, "end": v(89.68, 353.58) * mm});
            skLineSegment(sketch, "E724", {"start": v(89.68, 353.58) * mm, "end": v(89.8, 353.75) * mm});
            skLineSegment(sketch, "E725", {"start": v(89.8, 353.75) * mm, "end": v(89.97, 353.93) * mm});
            skLineSegment(sketch, "E726", {"start": v(89.97, 353.93) * mm, "end": v(90.08, 354.04) * mm});
            skLineSegment(sketch, "E727", {"start": v(90.08, 354.04) * mm, "end": v(90.2, 354.12) * mm});
            skLineSegment(sketch, "E728", {"start": v(90.2, 354.12) * mm, "end": v(90.3, 354.2) * mm});
            skLineSegment(sketch, "E729", {"start": v(90.3, 354.2) * mm, "end": v(90.45, 354.3) * mm});
            skLineSegment(sketch, "E730", {"start": v(90.45, 354.3) * mm, "end": v(90.56, 354.35) * mm});
            skLineSegment(sketch, "E731", {"start": v(90.56, 354.35) * mm, "end": v(90.7, 354.4) * mm});
            skLineSegment(sketch, "E732", {"start": v(90.7, 354.4) * mm, "end": v(90.85, 354.46) * mm});
            skLineSegment(sketch, "E733", {"start": v(90.85, 354.46) * mm, "end": v(91, 354.52) * mm});
            skLineSegment(sketch, "E734", {"start": v(91, 354.52) * mm, "end": v(91, 358.98) * mm});
            skLineSegment(sketch, "E735", {"start": v(91, 358.98) * mm, "end": v(91, 359.18) * mm});
            skLineSegment(sketch, "E736", {"start": v(91, 359.18) * mm, "end": v(91.02, 359.4) * mm});
            skLineSegment(sketch, "E737", {"start": v(91.02, 359.4) * mm, "end": v(91.08, 359.6) * mm});
            skLineSegment(sketch, "E738", {"start": v(91.08, 359.6) * mm, "end": v(91.16, 359.8) * mm});
            skLineSegment(sketch, "E739", {"start": v(91.16, 359.8) * mm, "end": v(91.25, 360) * mm});
            skLineSegment(sketch, "E740", {"start": v(91.25, 360) * mm, "end": v(91.36, 360.2) * mm});
            skLineSegment(sketch, "E741", {"start": v(91.36, 360.2) * mm, "end": v(91.5, 360.37) * mm});
            skLineSegment(sketch, "E742", {"start": v(91.5, 360.37) * mm, "end": v(91.64, 360.54) * mm});
            skLineSegment(sketch, "E743", {"start": v(91.64, 360.54) * mm, "end": v(91.81, 360.69) * mm});
            skLineSegment(sketch, "E744", {"start": v(91.81, 360.69) * mm, "end": v(92.01, 360.83) * mm});
            skLineSegment(sketch, "E745", {"start": v(92.01, 360.83) * mm, "end": v(92.18, 360.94) * mm});
            skLineSegment(sketch, "E746", {"start": v(92.18, 360.94) * mm, "end": v(92.38, 361.03) * mm});
            skLineSegment(sketch, "E747", {"start": v(92.38, 361.03) * mm, "end": v(92.58, 361.08) * mm});
            skLineSegment(sketch, "E748", {"start": v(92.58, 361.08) * mm, "end": v(92.78, 361.14) * mm});
            skLineSegment(sketch, "E749", {"start": v(92.78, 361.14) * mm, "end": v(92.98, 361.17) * mm});
            skLineSegment(sketch, "E750", {"start": v(92.98, 361.17) * mm, "end": v(93.2, 361.2) * mm});
            skLineSegment(sketch, "E751", {"start": v(93.2, 361.2) * mm, "end": v(93.43, 361.17) * mm});
            skLineSegment(sketch, "E752", {"start": v(93.43, 361.17) * mm, "end": v(93.66, 361.14) * mm});
            skLineSegment(sketch, "E753", {"start": v(93.66, 361.14) * mm, "end": v(93.86, 361.08) * mm});
            skLineSegment(sketch, "E754", {"start": v(93.86, 361.08) * mm, "end": v(94.06, 361.03) * mm});
            skLineSegment(sketch, "E755", {"start": v(94.06, 361.03) * mm, "end": v(94.26, 360.94) * mm});
            skLineSegment(sketch, "E756", {"start": v(94.26, 360.94) * mm, "end": v(94.43, 360.83) * mm});
            skLineSegment(sketch, "E757", {"start": v(94.43, 360.83) * mm, "end": v(94.6, 360.69) * mm});
            skLineSegment(sketch, "E758", {"start": v(94.6, 360.69) * mm, "end": v(94.77, 360.54) * mm});
            skLineSegment(sketch, "E759", {"start": v(94.77, 360.54) * mm, "end": v(94.91, 360.37) * mm});
            skLineSegment(sketch, "E760", {"start": v(94.91, 360.37) * mm, "end": v(95.05, 360.2) * mm});
            skLineSegment(sketch, "E761", {"start": v(95.05, 360.2) * mm, "end": v(95.17, 360) * mm});
            skLineSegment(sketch, "E762", {"start": v(95.17, 360) * mm, "end": v(95.25, 359.8) * mm});
            skLineSegment(sketch, "E763", {"start": v(95.25, 359.8) * mm, "end": v(95.34, 359.6) * mm});
            skLineSegment(sketch, "E764", {"start": v(95.34, 359.6) * mm, "end": v(95.4, 359.4) * mm});
            skLineSegment(sketch, "E765", {"start": v(95.4, 359.4) * mm, "end": v(95.42, 359.18) * mm});
            skLineSegment(sketch, "E766", {"start": v(95.42, 359.18) * mm, "end": v(95.42, 358.98) * mm});
            skLineSegment(sketch, "E767", {"start": v(95.42, 358.98) * mm, "end": v(95.42, 354.58) * mm});
            skLineSegment(sketch, "E768", {"start": v(95.42, 354.58) * mm, "end": v(98.2, 354.58) * mm});
            skLineSegment(sketch, "E769", {"start": v(98.2, 354.58) * mm, "end": v(98.4, 354.55) * mm});
            skLineSegment(sketch, "E770", {"start": v(98.4, 354.55) * mm, "end": v(98.63, 354.52) * mm});
            skLineSegment(sketch, "E771", {"start": v(98.63, 354.52) * mm, "end": v(98.83, 354.46) * mm});
            skLineSegment(sketch, "E772", {"start": v(98.83, 354.46) * mm, "end": v(99.03, 354.4) * mm});
            skLineSegment(sketch, "E773", {"start": v(99.03, 354.4) * mm, "end": v(99.23, 354.32) * mm});
            skLineSegment(sketch, "E774", {"start": v(99.23, 354.32) * mm, "end": v(99.43, 354.2) * mm});
            skLineSegment(sketch, "E775", {"start": v(99.43, 354.2) * mm, "end": v(99.6, 354.07) * mm});
            skLineSegment(sketch, "E776", {"start": v(99.6, 354.07) * mm, "end": v(99.77, 353.93) * mm});
            skLineSegment(sketch, "E777", {"start": v(99.77, 353.93) * mm, "end": v(99.91, 353.75) * mm});
            skLineSegment(sketch, "E778", {"start": v(99.91, 353.75) * mm, "end": v(100.05, 353.58) * mm});
            skLineSegment(sketch, "E779", {"start": v(100.05, 353.58) * mm, "end": v(100.17, 353.39) * mm});
            skLineSegment(sketch, "E780", {"start": v(100.17, 353.39) * mm, "end": v(100.25, 353.19) * mm});
            skLineSegment(sketch, "E781", {"start": v(100.25, 353.19) * mm, "end": v(100.3, 352.99) * mm});
            skLineSegment(sketch, "E782", {"start": v(100.3, 352.99) * mm, "end": v(100.37, 352.79) * mm});
            skLineSegment(sketch, "E783", {"start": v(100.37, 352.79) * mm, "end": v(100.4, 352.56) * mm});
            skLineSegment(sketch, "E784", {"start": v(100.4, 352.56) * mm, "end": v(100.42, 352.36) * mm});
            skLineSegment(sketch, "E785", {"start": v(100.42, 352.36) * mm, "end": v(100.4, 352.14) * mm});
            skLineSegment(sketch, "E786", {"start": v(100.4, 352.14) * mm, "end": v(100.37, 351.9) * mm});
            skLineSegment(sketch, "E787", {"start": v(100.37, 351.9) * mm, "end": v(100.3, 351.7) * mm});
            skLineSegment(sketch, "E788", {"start": v(100.3, 351.7) * mm, "end": v(100.25, 351.51) * mm});
            skLineSegment(sketch, "E789", {"start": v(100.25, 351.51) * mm, "end": v(100.17, 351.31) * mm});
            skLineSegment(sketch, "E790", {"start": v(100.17, 351.31) * mm, "end": v(100.05, 351.11) * mm});
            skLineSegment(sketch, "E791", {"start": v(100.05, 351.11) * mm, "end": v(99.91, 350.94) * mm});
            skLineSegment(sketch, "E792", {"start": v(99.91, 350.94) * mm, "end": v(99.77, 350.77) * mm});
            skLineSegment(sketch, "E793", {"start": v(99.77, 350.77) * mm, "end": v(99.6, 350.63) * mm});
            skLineSegment(sketch, "E794", {"start": v(99.6, 350.63) * mm, "end": v(99.43, 350.49) * mm});
            skLineSegment(sketch, "E795", {"start": v(99.43, 350.49) * mm, "end": v(99.23, 350.37) * mm});
            skLineSegment(sketch, "E796", {"start": v(99.23, 350.37) * mm, "end": v(99.03, 350.29) * mm});
            skLineSegment(sketch, "E797", {"start": v(99.03, 350.29) * mm, "end": v(98.83, 350.23) * mm});
            skLineSegment(sketch, "E798", {"start": v(98.83, 350.23) * mm, "end": v(98.63, 350.18) * mm});
            skLineSegment(sketch, "E799", {"start": v(98.63, 350.18) * mm, "end": v(98.4, 350.15) * mm});
            skLineSegment(sketch, "E800", {"start": v(98.4, 350.15) * mm, "end": v(98.2, 350.15) * mm});
            skLineSegment(sketch, "E801", {"start": v(98.2, 350.15) * mm, "end": v(95.42, 350.15) * mm});
            skLineSegment(sketch, "E802", {"start": v(95.42, 350.15) * mm, "end": v(95.42, 334.07) * mm});
            skLineSegment(sketch, "E803", {"start": v(95.42, 334.07) * mm, "end": v(95.42, 333.78) * mm});
            skLineSegment(sketch, "E804", {"start": v(95.42, 333.78) * mm, "end": v(95.48, 333.5) * mm});
            skLineSegment(sketch, "E805", {"start": v(95.48, 333.5) * mm, "end": v(95.54, 333.24) * mm});
            skLineSegment(sketch, "E806", {"start": v(95.54, 333.24) * mm, "end": v(95.62, 332.99) * mm});
            skLineSegment(sketch, "E807", {"start": v(95.62, 332.99) * mm, "end": v(95.73, 332.76) * mm});
            skLineSegment(sketch, "E808", {"start": v(95.73, 332.76) * mm, "end": v(95.88, 332.53) * mm});
            skLineSegment(sketch, "E809", {"start": v(95.88, 332.53) * mm, "end": v(96.05, 332.3) * mm});
            skLineSegment(sketch, "E810", {"start": v(96.05, 332.3) * mm, "end": v(96.22, 332.1) * mm});
            skLineSegment(sketch, "E811", {"start": v(96.22, 332.1) * mm, "end": v(96.44, 331.9) * mm});
            skLineSegment(sketch, "E812", {"start": v(96.44, 331.9) * mm, "end": v(96.64, 331.74) * mm});
            skLineSegment(sketch, "E813", {"start": v(96.64, 331.74) * mm, "end": v(96.87, 331.62) * mm});
            skLineSegment(sketch, "E814", {"start": v(96.87, 331.62) * mm, "end": v(97.13, 331.5) * mm});
            skLineSegment(sketch, "E815", {"start": v(97.13, 331.5) * mm, "end": v(97.38, 331.4) * mm});
            skLineSegment(sketch, "E816", {"start": v(97.38, 331.4) * mm, "end": v(97.64, 331.34) * mm});
            skLineSegment(sketch, "E817", {"start": v(97.64, 331.34) * mm, "end": v(97.9, 331.31) * mm});
            skLineSegment(sketch, "E818", {"start": v(97.9, 331.31) * mm, "end": v(98.2, 331.28) * mm});
            skLineSegment(sketch, "E819", {"start": v(98.2, 331.28) * mm, "end": v(98.43, 331.28) * mm});
            skLineSegment(sketch, "E820", {"start": v(98.43, 331.28) * mm, "end": v(98.63, 331.25) * mm});
            skLineSegment(sketch, "E821", {"start": v(98.63, 331.25) * mm, "end": v(98.86, 331.2) * mm});
            skLineSegment(sketch, "E822", {"start": v(98.86, 331.2) * mm, "end": v(99.06, 331.14) * mm});
            skLineSegment(sketch, "E823", {"start": v(99.06, 331.14) * mm, "end": v(99.26, 331.03) * mm});
            skLineSegment(sketch, "E824", {"start": v(99.26, 331.03) * mm, "end": v(99.43, 330.91) * mm});
            skLineSegment(sketch, "E825", {"start": v(99.43, 330.91) * mm, "end": v(99.63, 330.8) * mm});
            skLineSegment(sketch, "E826", {"start": v(99.63, 330.8) * mm, "end": v(99.8, 330.63) * mm});
            skLineSegment(sketch, "E827", {"start": v(99.8, 330.63) * mm, "end": v(99.94, 330.46) * mm});
            skLineSegment(sketch, "E828", {"start": v(99.94, 330.46) * mm, "end": v(100.08, 330.29) * mm});
            skLineSegment(sketch, "E829", {"start": v(100.08, 330.29) * mm, "end": v(100.2, 330.09) * mm});
            skLineSegment(sketch, "E830", {"start": v(100.2, 330.09) * mm, "end": v(100.28, 329.92) * mm});
            skLineSegment(sketch, "E831", {"start": v(100.28, 329.92) * mm, "end": v(100.34, 329.72) * mm});
            skLineSegment(sketch, "E832", {"start": v(100.34, 329.72) * mm, "end": v(100.4, 329.52) * mm});
            skLineSegment(sketch, "E833", {"start": v(100.4, 329.52) * mm, "end": v(100.42, 329.3) * mm});
            skLineSegment(sketch, "E834", {"start": v(100.42, 329.3) * mm, "end": v(100.42, 329.07) * mm});
            skLineSegment(sketch, "E835", {"start": v(100.42, 329.07) * mm, "end": v(100.42, 328.87) * mm});
            skLineSegment(sketch, "E836", {"start": v(100.42, 328.87) * mm, "end": v(100.4, 328.64) * mm});
            skLineSegment(sketch, "E837", {"start": v(100.4, 328.64) * mm, "end": v(100.34, 328.44) * mm});
            skLineSegment(sketch, "E838", {"start": v(100.34, 328.44) * mm, "end": v(100.28, 328.24) * mm});
            skLineSegment(sketch, "E839", {"start": v(100.28, 328.24) * mm, "end": v(100.2, 328.04) * mm});
            skLineSegment(sketch, "E840", {"start": v(100.2, 328.04) * mm, "end": v(100.08, 327.84) * mm});
            skLineSegment(sketch, "E841", {"start": v(100.08, 327.84) * mm, "end": v(99.94, 327.67) * mm});
            skLineSegment(sketch, "E842", {"start": v(99.94, 327.67) * mm, "end": v(99.8, 327.5) * mm});
            skLineSegment(sketch, "E843", {"start": v(99.8, 327.5) * mm, "end": v(99.63, 327.36) * mm});
            skLineSegment(sketch, "E844", {"start": v(99.63, 327.36) * mm, "end": v(99.43, 327.22) * mm});
            skLineSegment(sketch, "E845", {"start": v(99.43, 327.22) * mm, "end": v(99.26, 327.1) * mm});
            skLineSegment(sketch, "E846", {"start": v(99.26, 327.1) * mm, "end": v(99.06, 327.02) * mm});
            skLineSegment(sketch, "E847", {"start": v(99.06, 327.02) * mm, "end": v(98.86, 326.96) * mm});
            skLineSegment(sketch, "E848", {"start": v(98.86, 326.96) * mm, "end": v(98.63, 326.9) * mm});
            skLineSegment(sketch, "E849", {"start": v(98.63, 326.9) * mm, "end": v(98.43, 326.88) * mm});
            skLineSegment(sketch, "E850", {"start": v(98.43, 326.88) * mm, "end": v(98.2, 326.85) * mm});
            skLineSegment(sketch, "E851", {"start": v(98.2, 326.85) * mm, "end": v(97.47, 326.9) * mm});
            skLineSegment(sketch, "E852", {"start": v(97.47, 326.9) * mm, "end": v(96.76, 327) * mm});
            skLineSegment(sketch, "E853", {"start": v(96.76, 327) * mm, "end": v(96.08, 327.16) * mm});
            skLineSegment(sketch, "E854", {"start": v(96.08, 327.16) * mm, "end": v(95.45, 327.4) * mm});
            skLineSegment(sketch, "E855", {"start": v(95.45, 327.4) * mm, "end": v(94.83, 327.7) * mm});
            skLineSegment(sketch, "E856", {"start": v(94.83, 327.7) * mm, "end": v(94.23, 328.04) * mm});
            skLineSegment(sketch, "E857", {"start": v(94.23, 328.04) * mm, "end": v(93.66, 328.5) * mm});
            skLineSegment(sketch, "E858", {"start": v(93.66, 328.5) * mm, "end": v(93.12, 328.98) * mm});
            skLineSegment(sketch, "E859", {"start": v(93.12, 328.98) * mm, "end": v(92.6, 329.52) * mm});
            skLineSegment(sketch, "E860", {"start": v(92.6, 329.52) * mm, "end": v(92.18, 330.09) * mm});
            skLineSegment(sketch, "E861", {"start": v(92.18, 330.09) * mm, "end": v(91.81, 330.69) * mm});
            skLineSegment(sketch, "E862", {"start": v(91.81, 330.69) * mm, "end": v(91.53, 331.31) * mm});
            skLineSegment(sketch, "E863", {"start": v(91.53, 331.31) * mm, "end": v(91.27, 331.96) * mm});
            skLineSegment(sketch, "E864", {"start": v(91.27, 331.96) * mm, "end": v(91.13, 332.65) * mm});
            skLineSegment(sketch, "E865", {"start": v(91.13, 332.65) * mm, "end": v(91.02, 333.33) * mm});
            skLineSegment(sketch, "E866", {"start": v(91.02, 333.33) * mm, "end": v(91, 334.07) * mm});
            skLineSegment(sketch, "E867", {"start": v(91, 334.07) * mm, "end": v(91, 350.18) * mm});
            skLineSegment(sketch, "E868", {"start": v(91, 350.18) * mm, "end": v(90.85, 350.23) * mm});
            skLineSegment(sketch, "E869", {"start": v(90.85, 350.23) * mm, "end": v(90.7, 350.29) * mm});
            skLineSegment(sketch, "E870", {"start": v(90.7, 350.29) * mm, "end": v(90.56, 350.35) * mm});
            skLineSegment(sketch, "E871", {"start": v(90.56, 350.35) * mm, "end": v(90.45, 350.4) * mm});
            skLineSegment(sketch, "E872", {"start": v(90.45, 350.4) * mm, "end": v(90.3, 350.49) * mm});
            skLineSegment(sketch, "E873", {"start": v(90.3, 350.49) * mm, "end": v(90.2, 350.57) * mm});
            skLineSegment(sketch, "E874", {"start": v(90.2, 350.57) * mm, "end": v(90.08, 350.69) * mm});
            skLineSegment(sketch, "E875", {"start": v(90.08, 350.69) * mm, "end": v(89.97, 350.8) * mm});
            skLineSegment(sketch, "E876", {"start": v(89.97, 350.8) * mm, "end": v(89.8, 350.97) * mm});
            skLineSegment(sketch, "E877", {"start": v(89.8, 350.97) * mm, "end": v(89.68, 351.14) * mm});
            skLineSegment(sketch, "E878", {"start": v(89.68, 351.14) * mm, "end": v(89.57, 351.34) * mm});
            skLineSegment(sketch, "E879", {"start": v(89.57, 351.34) * mm, "end": v(89.46, 351.51) * mm});
            skLineSegment(sketch, "E880", {"start": v(89.46, 351.51) * mm, "end": v(89.4, 351.7) * mm});
            skLineSegment(sketch, "E881", {"start": v(89.4, 351.7) * mm, "end": v(89.34, 351.9) * mm});
            skLineSegment(sketch, "E882", {"start": v(104.88, 334.32) * mm, "end": v(104.83, 335.17) * mm});
            skLineSegment(sketch, "E883", {"start": v(104.83, 335.17) * mm, "end": v(104.83, 352.36) * mm});
            skLineSegment(sketch, "E884", {"start": v(104.83, 352.36) * mm, "end": v(104.85, 352.56) * mm});
            skLineSegment(sketch, "E885", {"start": v(104.85, 352.56) * mm, "end": v(104.88, 352.79) * mm});
            skLineSegment(sketch, "E886", {"start": v(104.88, 352.79) * mm, "end": v(104.94, 352.99) * mm});
            skLineSegment(sketch, "E887", {"start": v(104.94, 352.99) * mm, "end": v(105, 353.19) * mm});
            skLineSegment(sketch, "E888", {"start": v(105, 353.19) * mm, "end": v(105.08, 353.39) * mm});
            skLineSegment(sketch, "E889", {"start": v(105.08, 353.39) * mm, "end": v(105.2, 353.58) * mm});
            skLineSegment(sketch, "E890", {"start": v(105.2, 353.58) * mm, "end": v(105.34, 353.75) * mm});
            skLineSegment(sketch, "E891", {"start": v(105.34, 353.75) * mm, "end": v(105.48, 353.93) * mm});
            skLineSegment(sketch, "E892", {"start": v(105.48, 353.93) * mm, "end": v(105.65, 354.07) * mm});
            skLineSegment(sketch, "E893", {"start": v(105.65, 354.07) * mm, "end": v(105.82, 354.2) * mm});
            skLineSegment(sketch, "E894", {"start": v(105.82, 354.2) * mm, "end": v(106.02, 354.32) * mm});
            skLineSegment(sketch, "E895", {"start": v(106.02, 354.32) * mm, "end": v(106.22, 354.4) * mm});
            skLineSegment(sketch, "E896", {"start": v(106.22, 354.4) * mm, "end": v(106.42, 354.46) * mm});
            skLineSegment(sketch, "E897", {"start": v(106.42, 354.46) * mm, "end": v(106.62, 354.52) * mm});
            skLineSegment(sketch, "E898", {"start": v(106.62, 354.52) * mm, "end": v(106.84, 354.55) * mm});
            skLineSegment(sketch, "E899", {"start": v(106.84, 354.55) * mm, "end": v(107.04, 354.58) * mm});
            skLineSegment(sketch, "E900", {"start": v(107.04, 354.58) * mm, "end": v(107.27, 354.55) * mm});
            skLineSegment(sketch, "E901", {"start": v(107.27, 354.55) * mm, "end": v(107.5, 354.52) * mm});
            skLineSegment(sketch, "E902", {"start": v(107.5, 354.52) * mm, "end": v(107.7, 354.46) * mm});
            skLineSegment(sketch, "E903", {"start": v(107.7, 354.46) * mm, "end": v(107.9, 354.4) * mm});
            skLineSegment(sketch, "E904", {"start": v(107.9, 354.4) * mm, "end": v(108.1, 354.32) * mm});
            skLineSegment(sketch, "E905", {"start": v(108.1, 354.32) * mm, "end": v(108.3, 354.2) * mm});
            skLineSegment(sketch, "E906", {"start": v(108.3, 354.2) * mm, "end": v(108.46, 354.07) * mm});
            skLineSegment(sketch, "E907", {"start": v(108.46, 354.07) * mm, "end": v(108.63, 353.93) * mm});
            skLineSegment(sketch, "E908", {"start": v(108.63, 353.93) * mm, "end": v(108.77, 353.75) * mm});
            skLineSegment(sketch, "E909", {"start": v(108.77, 353.75) * mm, "end": v(108.92, 353.58) * mm});
            skLineSegment(sketch, "E910", {"start": v(108.92, 353.58) * mm, "end": v(109.03, 353.39) * mm});
            skLineSegment(sketch, "E911", {"start": v(109.03, 353.39) * mm, "end": v(109.12, 353.19) * mm});
            skLineSegment(sketch, "E912", {"start": v(109.12, 353.19) * mm, "end": v(109.17, 352.99) * mm});
            skLineSegment(sketch, "E913", {"start": v(109.17, 352.99) * mm, "end": v(109.23, 352.79) * mm});
            skLineSegment(sketch, "E914", {"start": v(109.23, 352.79) * mm, "end": v(109.26, 352.56) * mm});
            skLineSegment(sketch, "E915", {"start": v(109.26, 352.56) * mm, "end": v(109.26, 352.36) * mm});
            skLineSegment(sketch, "E916", {"start": v(109.26, 352.36) * mm, "end": v(109.26, 335.17) * mm});
            skLineSegment(sketch, "E917", {"start": v(109.26, 335.17) * mm, "end": v(109.29, 334.78) * mm});
            skLineSegment(sketch, "E918", {"start": v(109.29, 334.78) * mm, "end": v(109.34, 334.4) * mm});
            skLineSegment(sketch, "E919", {"start": v(109.34, 334.4) * mm, "end": v(109.43, 334.04) * mm});
            skLineSegment(sketch, "E920", {"start": v(109.43, 334.04) * mm, "end": v(109.54, 333.7) * mm});
            skLineSegment(sketch, "E921", {"start": v(100.25, 329.05) * mm, "end": v(100.42, 328.7) * mm});
            skLineSegment(sketch, "E922", {"start": v(109.71, 333.36) * mm, "end": v(109.91, 333.04) * mm});
            skLineSegment(sketch, "E923", {"start": v(109.91, 333.04) * mm, "end": v(110.14, 332.73) * mm});
            skLineSegment(sketch, "E924", {"start": v(110.14, 332.73) * mm, "end": v(110.4, 332.42) * mm});
            skLineSegment(sketch, "E925", {"start": v(110.4, 332.42) * mm, "end": v(110.7, 332.16) * mm});
            skLineSegment(sketch, "E926", {"start": v(110.7, 332.16) * mm, "end": v(111.02, 331.94) * mm});
            skLineSegment(sketch, "E927", {"start": v(111.02, 331.94) * mm, "end": v(111.33, 331.74) * mm});
            skLineSegment(sketch, "E928", {"start": v(111.33, 331.74) * mm, "end": v(111.67, 331.57) * mm});
            skLineSegment(sketch, "E929", {"start": v(111.67, 331.57) * mm, "end": v(112.01, 331.45) * mm});
            skLineSegment(sketch, "E930", {"start": v(112.01, 331.45) * mm, "end": v(112.38, 331.37) * mm});
            skLineSegment(sketch, "E931", {"start": v(112.38, 331.37) * mm, "end": v(112.75, 331.31) * mm});
            skLineSegment(sketch, "E932", {"start": v(112.75, 331.31) * mm, "end": v(113.15, 331.28) * mm});
            skLineSegment(sketch, "E933", {"start": v(113.15, 331.28) * mm, "end": v(117.04, 331.28) * mm});
            skLineSegment(sketch, "E934", {"start": v(117.04, 331.28) * mm, "end": v(117.04, 352.36) * mm});
            skLineSegment(sketch, "E935", {"start": v(117.04, 352.36) * mm, "end": v(117.04, 352.56) * mm});
            skLineSegment(sketch, "E936", {"start": v(117.04, 352.56) * mm, "end": v(117.07, 352.79) * mm});
            skLineSegment(sketch, "E937", {"start": v(117.07, 352.79) * mm, "end": v(117.13, 352.99) * mm});
            skLineSegment(sketch, "E938", {"start": v(117.13, 352.99) * mm, "end": v(117.18, 353.19) * mm});
            skLineSegment(sketch, "E939", {"start": v(117.18, 353.19) * mm, "end": v(117.27, 353.39) * mm});
            skLineSegment(sketch, "E940", {"start": v(117.27, 353.39) * mm, "end": v(117.38, 353.58) * mm});
            skLineSegment(sketch, "E941", {"start": v(117.38, 353.58) * mm, "end": v(117.53, 353.75) * mm});
            skLineSegment(sketch, "E942", {"start": v(117.53, 353.75) * mm, "end": v(117.67, 353.93) * mm});
            skLineSegment(sketch, "E943", {"start": v(117.67, 353.93) * mm, "end": v(117.84, 354.07) * mm});
            skLineSegment(sketch, "E944", {"start": v(117.84, 354.07) * mm, "end": v(118, 354.2) * mm});
            skLineSegment(sketch, "E945", {"start": v(118, 354.2) * mm, "end": v(118.2, 354.32) * mm});
            skLineSegment(sketch, "E946", {"start": v(118.2, 354.32) * mm, "end": v(118.4, 354.4) * mm});
            skLineSegment(sketch, "E947", {"start": v(118.4, 354.4) * mm, "end": v(118.6, 354.46) * mm});
            skLineSegment(sketch, "E948", {"start": v(118.6, 354.46) * mm, "end": v(118.8, 354.52) * mm});
            skLineSegment(sketch, "E949", {"start": v(118.8, 354.52) * mm, "end": v(119.03, 354.55) * mm});
            skLineSegment(sketch, "E950", {"start": v(119.03, 354.55) * mm, "end": v(119.26, 354.58) * mm});
            skLineSegment(sketch, "E951", {"start": v(119.26, 354.58) * mm, "end": v(119.46, 354.55) * mm});
            skLineSegment(sketch, "E952", {"start": v(119.46, 354.55) * mm, "end": v(119.68, 354.52) * mm});
            skLineSegment(sketch, "E953", {"start": v(119.68, 354.52) * mm, "end": v(119.88, 354.46) * mm});
            skLineSegment(sketch, "E954", {"start": v(119.88, 354.46) * mm, "end": v(120.08, 354.4) * mm});
            skLineSegment(sketch, "E955", {"start": v(120.08, 354.4) * mm, "end": v(120.28, 354.32) * mm});
            skLineSegment(sketch, "E956", {"start": v(120.28, 354.32) * mm, "end": v(120.48, 354.2) * mm});
            skLineSegment(sketch, "E957", {"start": v(120.48, 354.2) * mm, "end": v(120.65, 354.07) * mm});
            skLineSegment(sketch, "E958", {"start": v(120.65, 354.07) * mm, "end": v(120.82, 353.93) * mm});
            skLineSegment(sketch, "E959", {"start": v(120.82, 353.93) * mm, "end": v(120.96, 353.75) * mm});
            skLineSegment(sketch, "E960", {"start": v(120.96, 353.75) * mm, "end": v(121.1, 353.58) * mm});
            skLineSegment(sketch, "E961", {"start": v(121.1, 353.58) * mm, "end": v(121.22, 353.39) * mm});
            skLineSegment(sketch, "E962", {"start": v(121.22, 353.39) * mm, "end": v(121.3, 353.19) * mm});
            skLineSegment(sketch, "E963", {"start": v(121.3, 353.19) * mm, "end": v(121.36, 352.99) * mm});
            skLineSegment(sketch, "E964", {"start": v(121.36, 352.99) * mm, "end": v(121.42, 352.79) * mm});
            skLineSegment(sketch, "E965", {"start": v(121.42, 352.79) * mm, "end": v(121.45, 352.56) * mm});
            skLineSegment(sketch, "E966", {"start": v(121.45, 352.56) * mm, "end": v(121.47, 352.36) * mm});
            skLineSegment(sketch, "E967", {"start": v(121.47, 352.36) * mm, "end": v(121.47, 329.07) * mm});
            skLineSegment(sketch, "E968", {"start": v(121.47, 329.07) * mm, "end": v(121.45, 328.87) * mm});
            skLineSegment(sketch, "E969", {"start": v(121.45, 328.87) * mm, "end": v(121.42, 328.64) * mm});
            skLineSegment(sketch, "E970", {"start": v(121.42, 328.64) * mm, "end": v(121.36, 328.44) * mm});
            skLineSegment(sketch, "E971", {"start": v(121.36, 328.44) * mm, "end": v(121.3, 328.24) * mm});
            skLineSegment(sketch, "E972", {"start": v(121.3, 328.24) * mm, "end": v(121.22, 328.04) * mm});
            skLineSegment(sketch, "E973", {"start": v(121.22, 328.04) * mm, "end": v(121.1, 327.84) * mm});
            skLineSegment(sketch, "E974", {"start": v(121.1, 327.84) * mm, "end": v(120.96, 327.67) * mm});
            skLineSegment(sketch, "E975", {"start": v(120.96, 327.67) * mm, "end": v(120.82, 327.5) * mm});
            skLineSegment(sketch, "E976", {"start": v(120.82, 327.5) * mm, "end": v(120.65, 327.36) * mm});
            skLineSegment(sketch, "E977", {"start": v(120.65, 327.36) * mm, "end": v(120.48, 327.22) * mm});
            skLineSegment(sketch, "E978", {"start": v(120.48, 327.22) * mm, "end": v(120.28, 327.1) * mm});
            skLineSegment(sketch, "E979", {"start": v(120.28, 327.1) * mm, "end": v(120.08, 327.02) * mm});
            skLineSegment(sketch, "E980", {"start": v(120.08, 327.02) * mm, "end": v(119.88, 326.96) * mm});
            skLineSegment(sketch, "E981", {"start": v(119.88, 326.96) * mm, "end": v(119.68, 326.9) * mm});
            skLineSegment(sketch, "E982", {"start": v(119.68, 326.9) * mm, "end": v(119.46, 326.88) * mm});
            skLineSegment(sketch, "E983", {"start": v(119.46, 326.88) * mm, "end": v(119.26, 326.85) * mm});
            skLineSegment(sketch, "E984", {"start": v(119.26, 326.85) * mm, "end": v(113.15, 326.85) * mm});
            skLineSegment(sketch, "E985", {"start": v(113.15, 326.85) * mm, "end": v(112.3, 326.9) * mm});
            skLineSegment(sketch, "E986", {"start": v(112.3, 326.9) * mm, "end": v(111.5, 327.02) * mm});
            skLineSegment(sketch, "E987", {"start": v(111.5, 327.02) * mm, "end": v(110.7, 327.22) * mm});
            skLineSegment(sketch, "E988", {"start": v(110.7, 327.22) * mm, "end": v(109.97, 327.48) * mm});
            skLineSegment(sketch, "E989", {"start": v(109.97, 327.48) * mm, "end": v(109.26, 327.82) * mm});
            skLineSegment(sketch, "E990", {"start": v(109.26, 327.82) * mm, "end": v(108.55, 328.24) * mm});
            skLineSegment(sketch, "E991", {"start": v(108.55, 328.24) * mm, "end": v(107.9, 328.73) * mm});
            skLineSegment(sketch, "E992", {"start": v(107.9, 328.73) * mm, "end": v(107.27, 329.3) * mm});
            skLineSegment(sketch, "E993", {"start": v(107.27, 329.3) * mm, "end": v(106.7, 329.92) * mm});
            skLineSegment(sketch, "E994", {"start": v(106.7, 329.92) * mm, "end": v(106.22, 330.57) * mm});
            skLineSegment(sketch, "E995", {"start": v(106.22, 330.57) * mm, "end": v(105.8, 331.28) * mm});
            skLineSegment(sketch, "E996", {"start": v(105.8, 331.28) * mm, "end": v(105.45, 332) * mm});
            skLineSegment(sketch, "E997", {"start": v(105.45, 332) * mm, "end": v(105.2, 332.73) * mm});
            skLineSegment(sketch, "E998", {"start": v(105.2, 332.73) * mm, "end": v(105, 333.53) * mm});
            skLineSegment(sketch, "E999", {"start": v(105, 333.53) * mm, "end": v(104.88, 334.32) * mm});
            skLineSegment(sketch, "E1000", {"start": v(129.26, 328.64) * mm, "end": v(129.23, 328.87) * mm});
            skLineSegment(sketch, "E1001", {"start": v(129.23, 328.87) * mm, "end": v(129.23, 329.07) * mm});
            skLineSegment(sketch, "E1002", {"start": v(129.23, 329.07) * mm, "end": v(129.23, 352.36) * mm});
            skLineSegment(sketch, "E1003", {"start": v(129.23, 352.36) * mm, "end": v(129.23, 352.56) * mm});
            skLineSegment(sketch, "E1004", {"start": v(129.23, 352.56) * mm, "end": v(129.26, 352.79) * mm});
            skLineSegment(sketch, "E1005", {"start": v(129.26, 352.79) * mm, "end": v(129.32, 352.99) * mm});
            skLineSegment(sketch, "E1006", {"start": v(129.32, 352.99) * mm, "end": v(129.4, 353.19) * mm});
            skLineSegment(sketch, "E1007", {"start": v(129.4, 353.19) * mm, "end": v(129.49, 353.39) * mm});
            skLineSegment(sketch, "E1008", {"start": v(129.49, 353.39) * mm, "end": v(129.6, 353.58) * mm});
            skLineSegment(sketch, "E1009", {"start": v(129.6, 353.58) * mm, "end": v(129.74, 353.75) * mm});
            skLineSegment(sketch, "E1010", {"start": v(129.74, 353.75) * mm, "end": v(129.88, 353.93) * mm});
            skLineSegment(sketch, "E1011", {"start": v(129.88, 353.93) * mm, "end": v(130.05, 354.07) * mm});
            skLineSegment(sketch, "E1012", {"start": v(130.05, 354.07) * mm, "end": v(130.22, 354.2) * mm});
            skLineSegment(sketch, "E1013", {"start": v(130.22, 354.2) * mm, "end": v(130.4, 354.32) * mm});
            skLineSegment(sketch, "E1014", {"start": v(130.4, 354.32) * mm, "end": v(130.6, 354.4) * mm});
            skLineSegment(sketch, "E1015", {"start": v(130.6, 354.4) * mm, "end": v(130.8, 354.46) * mm});
            skLineSegment(sketch, "E1016", {"start": v(130.8, 354.46) * mm, "end": v(131, 354.52) * mm});
            skLineSegment(sketch, "E1017", {"start": v(131, 354.52) * mm, "end": v(131.22, 354.55) * mm});
            skLineSegment(sketch, "E1018", {"start": v(131.22, 354.55) * mm, "end": v(131.45, 354.58) * mm});
            skLineSegment(sketch, "E1019", {"start": v(131.45, 354.58) * mm, "end": v(147.53, 354.58) * mm});
            skLineSegment(sketch, "E1020", {"start": v(147.53, 354.58) * mm, "end": v(148.35, 354.52) * mm});
            skLineSegment(sketch, "E1021", {"start": v(148.35, 354.52) * mm, "end": v(149.17, 354.4) * mm});
            skLineSegment(sketch, "E1022", {"start": v(149.17, 354.4) * mm, "end": v(149.94, 354.2) * mm});
            skLineSegment(sketch, "E1023", {"start": v(149.94, 354.2) * mm, "end": v(150.7, 353.95) * mm});
            skLineSegment(sketch, "E1024", {"start": v(150.7, 353.95) * mm, "end": v(151.42, 353.61) * mm});
            skLineSegment(sketch, "E1025", {"start": v(151.42, 353.61) * mm, "end": v(152.1, 353.19) * mm});
            skLineSegment(sketch, "E1026", {"start": v(152.1, 353.19) * mm, "end": v(152.75, 352.7) * mm});
            skLineSegment(sketch, "E1027", {"start": v(152.75, 352.7) * mm, "end": v(153.38, 352.14) * mm});
            skLineSegment(sketch, "E1028", {"start": v(153.38, 352.14) * mm, "end": v(153.95, 351.51) * mm});
            skLineSegment(sketch, "E1029", {"start": v(153.95, 351.51) * mm, "end": v(154.46, 350.86) * mm});
            skLineSegment(sketch, "E1030", {"start": v(154.46, 350.86) * mm, "end": v(154.86, 350.15) * mm});
            skLineSegment(sketch, "E1031", {"start": v(154.86, 350.15) * mm, "end": v(155.23, 349.44) * mm});
            skLineSegment(sketch, "E1032", {"start": v(155.23, 349.44) * mm, "end": v(155.48, 348.7) * mm});
            skLineSegment(sketch, "E1033", {"start": v(155.48, 348.7) * mm, "end": v(155.68, 347.9) * mm});
            skLineSegment(sketch, "E1034", {"start": v(155.68, 347.9) * mm, "end": v(155.8, 347.1) * mm});
            skLineSegment(sketch, "E1035", {"start": v(155.8, 347.1) * mm, "end": v(155.82, 346.25) * mm});
            skLineSegment(sketch, "E1036", {"start": v(155.82, 346.25) * mm, "end": v(155.82, 329.07) * mm});
            skLineSegment(sketch, "E1037", {"start": v(155.82, 329.07) * mm, "end": v(155.82, 328.87) * mm});
            skLineSegment(sketch, "E1038", {"start": v(155.82, 328.87) * mm, "end": v(155.8, 328.64) * mm});
            skLineSegment(sketch, "E1039", {"start": v(155.8, 328.64) * mm, "end": v(155.74, 328.44) * mm});
            skLineSegment(sketch, "E1040", {"start": v(155.74, 328.44) * mm, "end": v(155.65, 328.24) * mm});
            skLineSegment(sketch, "E1041", {"start": v(155.65, 328.24) * mm, "end": v(155.57, 328.04) * mm});
            skLineSegment(sketch, "E1042", {"start": v(155.57, 328.04) * mm, "end": v(155.45, 327.84) * mm});
            skLineSegment(sketch, "E1043", {"start": v(155.45, 327.84) * mm, "end": v(155.31, 327.67) * mm});
            skLineSegment(sketch, "E1044", {"start": v(155.31, 327.67) * mm, "end": v(155.17, 327.5) * mm});
            skLineSegment(sketch, "E1045", {"start": v(155.17, 327.5) * mm, "end": v(155, 327.36) * mm});
            skLineSegment(sketch, "E1046", {"start": v(155, 327.36) * mm, "end": v(154.83, 327.22) * mm});
            skLineSegment(sketch, "E1047", {"start": v(154.83, 327.22) * mm, "end": v(154.66, 327.1) * mm});
            skLineSegment(sketch, "E1048", {"start": v(154.66, 327.1) * mm, "end": v(154.46, 327.02) * mm});
            skLineSegment(sketch, "E1049", {"start": v(154.46, 327.02) * mm, "end": v(154.26, 326.96) * mm});
            skLineSegment(sketch, "E1050", {"start": v(154.26, 326.96) * mm, "end": v(154.06, 326.9) * mm});
            skLineSegment(sketch, "E1051", {"start": v(154.06, 326.9) * mm, "end": v(153.83, 326.88) * mm});
            skLineSegment(sketch, "E1052", {"start": v(153.83, 326.88) * mm, "end": v(153.6, 326.85) * mm});
            skLineSegment(sketch, "E1053", {"start": v(153.6, 326.85) * mm, "end": v(153.38, 326.88) * mm});
            skLineSegment(sketch, "E1054", {"start": v(153.38, 326.88) * mm, "end": v(153.15, 326.9) * mm});
            skLineSegment(sketch, "E1055", {"start": v(153.15, 326.9) * mm, "end": v(152.95, 326.96) * mm});
            skLineSegment(sketch, "E1056", {"start": v(152.95, 326.96) * mm, "end": v(152.75, 327.02) * mm});
            skLineSegment(sketch, "E1057", {"start": v(152.75, 327.02) * mm, "end": v(152.55, 327.1) * mm});
            skLineSegment(sketch, "E1058", {"start": v(152.55, 327.1) * mm, "end": v(152.38, 327.22) * mm});
            skLineSegment(sketch, "E1059", {"start": v(152.38, 327.22) * mm, "end": v(152.21, 327.36) * mm});
            skLineSegment(sketch, "E1060", {"start": v(152.21, 327.36) * mm, "end": v(152.04, 327.5) * mm});
            skLineSegment(sketch, "E1061", {"start": v(152.04, 327.5) * mm, "end": v(151.9, 327.67) * mm});
            skLineSegment(sketch, "E1062", {"start": v(151.9, 327.67) * mm, "end": v(151.76, 327.84) * mm});
            skLineSegment(sketch, "E1063", {"start": v(151.76, 327.84) * mm, "end": v(151.65, 328.04) * mm});
            skLineSegment(sketch, "E1064", {"start": v(151.65, 328.04) * mm, "end": v(151.56, 328.24) * mm});
            skLineSegment(sketch, "E1065", {"start": v(151.56, 328.24) * mm, "end": v(151.47, 328.44) * mm});
            skLineSegment(sketch, "E1066", {"start": v(151.47, 328.44) * mm, "end": v(151.42, 328.64) * mm});
            skLineSegment(sketch, "E1067", {"start": v(151.42, 328.64) * mm, "end": v(151.39, 328.87) * mm});
            skLineSegment(sketch, "E1068", {"start": v(151.39, 328.87) * mm, "end": v(151.39, 329.07) * mm});
            skLineSegment(sketch, "E1069", {"start": v(151.39, 329.07) * mm, "end": v(151.39, 346.25) * mm});
            skLineSegment(sketch, "E1070", {"start": v(151.39, 346.25) * mm, "end": v(151.36, 346.65) * mm});
            skLineSegment(sketch, "E1071", {"start": v(151.36, 346.65) * mm, "end": v(151.33, 347.02) * mm});
            skLineSegment(sketch, "E1072", {"start": v(151.33, 347.02) * mm, "end": v(151.22, 347.4) * mm});
            skLineSegment(sketch, "E1073", {"start": v(151.22, 347.4) * mm, "end": v(151.1, 347.73) * mm});
            skLineSegment(sketch, "E1074", {"start": v(151.1, 347.73) * mm, "end": v(150.94, 348.07) * mm});
            skLineSegment(sketch, "E1075", {"start": v(150.94, 348.07) * mm, "end": v(150.76, 348.39) * mm});
            skLineSegment(sketch, "E1076", {"start": v(150.76, 348.39) * mm, "end": v(150.5, 348.7) * mm});
            skLineSegment(sketch, "E1077", {"start": v(150.5, 348.7) * mm, "end": v(150.25, 349.01) * mm});
            skLineSegment(sketch, "E1078", {"start": v(150.25, 349.01) * mm, "end": v(149.97, 349.27) * mm});
            skLineSegment(sketch, "E1079", {"start": v(149.97, 349.27) * mm, "end": v(149.66, 349.5) * mm});
            skLineSegment(sketch, "E1080", {"start": v(149.66, 349.5) * mm, "end": v(149.34, 349.7) * mm});
            skLineSegment(sketch, "E1081", {"start": v(149.34, 349.7) * mm, "end": v(149, 349.86) * mm});
            skLineSegment(sketch, "E1082", {"start": v(149, 349.86) * mm, "end": v(148.66, 349.98) * mm});
            skLineSegment(sketch, "E1083", {"start": v(148.66, 349.98) * mm, "end": v(148.3, 350.06) * mm});
            skLineSegment(sketch, "E1084", {"start": v(148.3, 350.06) * mm, "end": v(147.9, 350.12) * mm});
            skLineSegment(sketch, "E1085", {"start": v(147.9, 350.12) * mm, "end": v(147.53, 350.15) * mm});
            skLineSegment(sketch, "E1086", {"start": v(147.53, 350.15) * mm, "end": v(144.74, 350.15) * mm});
            skLineSegment(sketch, "E1087", {"start": v(144.74, 350.15) * mm, "end": v(144.74, 329.07) * mm});
            skLineSegment(sketch, "E1088", {"start": v(144.74, 329.07) * mm, "end": v(144.74, 328.87) * mm});
            skLineSegment(sketch, "E1089", {"start": v(144.74, 328.87) * mm, "end": v(144.71, 328.64) * mm});
            skLineSegment(sketch, "E1090", {"start": v(144.71, 328.64) * mm, "end": v(144.66, 328.44) * mm});
            skLineSegment(sketch, "E1091", {"start": v(144.66, 328.44) * mm, "end": v(144.57, 328.24) * mm});
            skLineSegment(sketch, "E1092", {"start": v(144.57, 328.24) * mm, "end": v(144.49, 328.04) * mm});
            skLineSegment(sketch, "E1093", {"start": v(144.49, 328.04) * mm, "end": v(144.37, 327.84) * mm});
            skLineSegment(sketch, "E1094", {"start": v(144.37, 327.84) * mm, "end": v(144.23, 327.67) * mm});
            skLineSegment(sketch, "E1095", {"start": v(144.23, 327.67) * mm, "end": v(144.09, 327.5) * mm});
            skLineSegment(sketch, "E1096", {"start": v(144.09, 327.5) * mm, "end": v(143.92, 327.36) * mm});
            skLineSegment(sketch, "E1097", {"start": v(143.92, 327.36) * mm, "end": v(143.75, 327.22) * mm});
            skLineSegment(sketch, "E1098", {"start": v(143.75, 327.22) * mm, "end": v(143.58, 327.1) * mm});
            skLineSegment(sketch, "E1099", {"start": v(143.58, 327.1) * mm, "end": v(143.38, 327.02) * mm});
            skLineSegment(sketch, "E1100", {"start": v(143.38, 327.02) * mm, "end": v(143.18, 326.96) * mm});
            skLineSegment(sketch, "E1101", {"start": v(143.18, 326.96) * mm, "end": v(142.98, 326.9) * mm});
            skLineSegment(sketch, "E1102", {"start": v(142.98, 326.9) * mm, "end": v(142.75, 326.88) * mm});
            skLineSegment(sketch, "E1103", {"start": v(142.75, 326.88) * mm, "end": v(142.53, 326.85) * mm});
            skLineSegment(sketch, "E1104", {"start": v(142.53, 326.85) * mm, "end": v(142.3, 326.88) * mm});
            skLineSegment(sketch, "E1105", {"start": v(142.3, 326.88) * mm, "end": v(142.07, 326.9) * mm});
            skLineSegment(sketch, "E1106", {"start": v(142.07, 326.9) * mm, "end": v(141.87, 326.96) * mm});
            skLineSegment(sketch, "E1107", {"start": v(141.87, 326.96) * mm, "end": v(141.67, 327.02) * mm});
            skLineSegment(sketch, "E1108", {"start": v(141.67, 327.02) * mm, "end": v(141.47, 327.1) * mm});
            skLineSegment(sketch, "E1109", {"start": v(141.47, 327.1) * mm, "end": v(141.3, 327.22) * mm});
            skLineSegment(sketch, "E1110", {"start": v(141.3, 327.22) * mm, "end": v(141.13, 327.36) * mm});
            skLineSegment(sketch, "E1111", {"start": v(141.13, 327.36) * mm, "end": v(140.96, 327.5) * mm});
            skLineSegment(sketch, "E1112", {"start": v(140.96, 327.5) * mm, "end": v(140.82, 327.67) * mm});
            skLineSegment(sketch, "E1113", {"start": v(140.82, 327.67) * mm, "end": v(140.68, 327.84) * mm});
            skLineSegment(sketch, "E1114", {"start": v(140.68, 327.84) * mm, "end": v(140.57, 328.04) * mm});
            skLineSegment(sketch, "E1115", {"start": v(140.57, 328.04) * mm, "end": v(140.48, 328.24) * mm});
            skLineSegment(sketch, "E1116", {"start": v(140.48, 328.24) * mm, "end": v(140.4, 328.44) * mm});
            skLineSegment(sketch, "E1117", {"start": v(140.4, 328.44) * mm, "end": v(140.34, 328.64) * mm});
            skLineSegment(sketch, "E1118", {"start": v(140.34, 328.64) * mm, "end": v(140.3, 328.87) * mm});
            skLineSegment(sketch, "E1119", {"start": v(140.3, 328.87) * mm, "end": v(140.3, 329.07) * mm});
            skLineSegment(sketch, "E1120", {"start": v(140.3, 329.07) * mm, "end": v(140.3, 350.15) * mm});
            skLineSegment(sketch, "E1121", {"start": v(140.3, 350.15) * mm, "end": v(133.66, 350.15) * mm});
            skLineSegment(sketch, "E1122", {"start": v(133.66, 350.15) * mm, "end": v(133.66, 329.07) * mm});
            skLineSegment(sketch, "E1123", {"start": v(133.66, 329.07) * mm, "end": v(133.66, 328.87) * mm});
            skLineSegment(sketch, "E1124", {"start": v(133.66, 328.87) * mm, "end": v(133.63, 328.64) * mm});
            skLineSegment(sketch, "E1125", {"start": v(133.63, 328.64) * mm, "end": v(133.58, 328.44) * mm});
            skLineSegment(sketch, "E1126", {"start": v(133.58, 328.44) * mm, "end": v(133.5, 328.24) * mm});
            skLineSegment(sketch, "E1127", {"start": v(133.5, 328.24) * mm, "end": v(133.4, 328.04) * mm});
            skLineSegment(sketch, "E1128", {"start": v(133.4, 328.04) * mm, "end": v(133.3, 327.84) * mm});
            skLineSegment(sketch, "E1129", {"start": v(133.3, 327.84) * mm, "end": v(133.15, 327.67) * mm});
            skLineSegment(sketch, "E1130", {"start": v(133.15, 327.67) * mm, "end": v(133, 327.5) * mm});
            skLineSegment(sketch, "E1131", {"start": v(133, 327.5) * mm, "end": v(132.84, 327.36) * mm});
            skLineSegment(sketch, "E1132", {"start": v(132.84, 327.36) * mm, "end": v(132.67, 327.22) * mm});
            skLineSegment(sketch, "E1133", {"start": v(132.67, 327.22) * mm, "end": v(132.5, 327.1) * mm});
            skLineSegment(sketch, "E1134", {"start": v(132.5, 327.1) * mm, "end": v(132.3, 327.02) * mm});
            skLineSegment(sketch, "E1135", {"start": v(132.3, 327.02) * mm, "end": v(132.1, 326.96) * mm});
            skLineSegment(sketch, "E1136", {"start": v(132.1, 326.96) * mm, "end": v(131.9, 326.9) * mm});
            skLineSegment(sketch, "E1137", {"start": v(131.9, 326.9) * mm, "end": v(131.67, 326.88) * mm});
            skLineSegment(sketch, "E1138", {"start": v(131.67, 326.88) * mm, "end": v(131.45, 326.85) * mm});
            skLineSegment(sketch, "E1139", {"start": v(131.45, 326.85) * mm, "end": v(131.22, 326.88) * mm});
            skLineSegment(sketch, "E1140", {"start": v(131.22, 326.88) * mm, "end": v(131, 326.9) * mm});
            skLineSegment(sketch, "E1141", {"start": v(131, 326.9) * mm, "end": v(130.8, 326.96) * mm});
            skLineSegment(sketch, "E1142", {"start": v(130.8, 326.96) * mm, "end": v(130.6, 327.02) * mm});
            skLineSegment(sketch, "E1143", {"start": v(130.6, 327.02) * mm, "end": v(130.4, 327.1) * mm});
            skLineSegment(sketch, "E1144", {"start": v(130.4, 327.1) * mm, "end": v(130.22, 327.22) * mm});
            skLineSegment(sketch, "E1145", {"start": v(130.22, 327.22) * mm, "end": v(130.05, 327.36) * mm});
            skLineSegment(sketch, "E1146", {"start": v(130.05, 327.36) * mm, "end": v(129.88, 327.5) * mm});
            skLineSegment(sketch, "E1147", {"start": v(129.88, 327.5) * mm, "end": v(129.74, 327.67) * mm});
            skLineSegment(sketch, "E1148", {"start": v(129.74, 327.67) * mm, "end": v(129.6, 327.84) * mm});
            skLineSegment(sketch, "E1149", {"start": v(129.6, 327.84) * mm, "end": v(129.49, 328.04) * mm});
            skLineSegment(sketch, "E1150", {"start": v(129.49, 328.04) * mm, "end": v(129.4, 328.24) * mm});
            skLineSegment(sketch, "E1151", {"start": v(129.4, 328.24) * mm, "end": v(129.32, 328.44) * mm});
            skLineSegment(sketch, "E1152", {"start": v(129.32, 328.44) * mm, "end": v(129.26, 328.64) * mm});
            skLineSegment(sketch, "E1153", {"start": v(174.17, 330.2) * mm, "end": v(174.15, 330.4) * mm});
            skLineSegment(sketch, "E1154", {"start": v(174.15, 330.4) * mm, "end": v(174.17, 330.63) * mm});
            skLineSegment(sketch, "E1155", {"start": v(174.17, 330.63) * mm, "end": v(174.2, 330.86) * mm});
            skLineSegment(sketch, "E1156", {"start": v(174.2, 330.86) * mm, "end": v(174.26, 331.06) * mm});
            skLineSegment(sketch, "E1157", {"start": v(174.26, 331.06) * mm, "end": v(174.32, 331.25) * mm});
            skLineSegment(sketch, "E1158", {"start": v(174.32, 331.25) * mm, "end": v(174.4, 331.45) * mm});
            skLineSegment(sketch, "E1159", {"start": v(174.4, 331.45) * mm, "end": v(174.52, 331.62) * mm});
            skLineSegment(sketch, "E1160", {"start": v(174.52, 331.62) * mm, "end": v(174.66, 331.82) * mm});
            skLineSegment(sketch, "E1161", {"start": v(174.66, 331.82) * mm, "end": v(174.8, 331.96) * mm});
            skLineSegment(sketch, "E1162", {"start": v(174.8, 331.96) * mm, "end": v(174.97, 332.13) * mm});
            skLineSegment(sketch, "E1163", {"start": v(174.97, 332.13) * mm, "end": v(175.14, 332.25) * mm});
            skLineSegment(sketch, "E1164", {"start": v(175.14, 332.25) * mm, "end": v(175.34, 332.36) * mm});
            skLineSegment(sketch, "E1165", {"start": v(175.34, 332.36) * mm, "end": v(175.54, 332.48) * mm});
            skLineSegment(sketch, "E1166", {"start": v(175.54, 332.48) * mm, "end": v(175.74, 332.53) * mm});
            skLineSegment(sketch, "E1167", {"start": v(175.74, 332.53) * mm, "end": v(175.94, 332.59) * mm});
            skLineSegment(sketch, "E1168", {"start": v(175.94, 332.59) * mm, "end": v(176.16, 332.62) * mm});
            skLineSegment(sketch, "E1169", {"start": v(176.16, 332.62) * mm, "end": v(176.36, 332.62) * mm});
            skLineSegment(sketch, "E1170", {"start": v(176.36, 332.62) * mm, "end": v(176.59, 332.62) * mm});
            skLineSegment(sketch, "E1171", {"start": v(176.59, 332.62) * mm, "end": v(176.82, 332.59) * mm});
            skLineSegment(sketch, "E1172", {"start": v(176.82, 332.59) * mm, "end": v(177.02, 332.53) * mm});
            skLineSegment(sketch, "E1173", {"start": v(177.02, 332.53) * mm, "end": v(177.21, 332.48) * mm});
            skLineSegment(sketch, "E1174", {"start": v(177.21, 332.48) * mm, "end": v(177.41, 332.4) * mm});
            skLineSegment(sketch, "E1175", {"start": v(177.41, 332.4) * mm, "end": v(177.61, 332.28) * mm});
            skLineSegment(sketch, "E1176", {"start": v(177.61, 332.28) * mm, "end": v(177.78, 332.13) * mm});
            skLineSegment(sketch, "E1177", {"start": v(177.78, 332.13) * mm, "end": v(177.95, 332) * mm});
            skLineSegment(sketch, "E1178", {"start": v(177.95, 332) * mm, "end": v(178.27, 331.7) * mm});
            skLineSegment(sketch, "E1179", {"start": v(178.27, 331.7) * mm, "end": v(178.58, 331.45) * mm});
            skLineSegment(sketch, "E1180", {"start": v(178.58, 331.45) * mm, "end": v(178.92, 331.25) * mm});
            skLineSegment(sketch, "E1181", {"start": v(178.92, 331.25) * mm, "end": v(179.26, 331.08) * mm});
            skLineSegment(sketch, "E1182", {"start": v(179.26, 331.08) * mm, "end": v(179.63, 330.94) * mm});
            skLineSegment(sketch, "E1183", {"start": v(179.63, 330.94) * mm, "end": v(180, 330.86) * mm});
            skLineSegment(sketch, "E1184", {"start": v(180, 330.86) * mm, "end": v(180.4, 330.8) * mm});
            skLineSegment(sketch, "E1185", {"start": v(180.4, 330.8) * mm, "end": v(180.77, 330.77) * mm});
            skLineSegment(sketch, "E1186", {"start": v(180.77, 330.77) * mm, "end": v(181.2, 330.8) * mm});
            skLineSegment(sketch, "E1187", {"start": v(181.2, 330.8) * mm, "end": v(181.56, 330.83) * mm});
            skLineSegment(sketch, "E1188", {"start": v(181.56, 330.83) * mm, "end": v(181.93, 330.94) * mm});
            skLineSegment(sketch, "E1189", {"start": v(181.93, 330.94) * mm, "end": v(182.27, 331.06) * mm});
            skLineSegment(sketch, "E1190", {"start": v(182.27, 331.06) * mm, "end": v(182.61, 331.23) * mm});
            skLineSegment(sketch, "E1191", {"start": v(182.61, 331.23) * mm, "end": v(182.95, 331.4) * mm});
            skLineSegment(sketch, "E1192", {"start": v(182.95, 331.4) * mm, "end": v(183.24, 331.65) * mm});
            skLineSegment(sketch, "E1193", {"start": v(183.24, 331.65) * mm, "end": v(183.52, 331.9) * mm});
            skLineSegment(sketch, "E1194", {"start": v(183.52, 331.9) * mm, "end": v(183.8, 332.2) * mm});
            skLineSegment(sketch, "E1195", {"start": v(183.8, 332.2) * mm, "end": v(184.03, 332.5) * mm});
            skLineSegment(sketch, "E1196", {"start": v(184.03, 332.5) * mm, "end": v(184.23, 332.82) * mm});
            skLineSegment(sketch, "E1197", {"start": v(184.23, 332.82) * mm, "end": v(184.37, 333.16) * mm});
            skLineSegment(sketch, "E1198", {"start": v(184.37, 333.16) * mm, "end": v(184.49, 333.5) * mm});
            skLineSegment(sketch, "E1199", {"start": v(184.49, 333.5) * mm, "end": v(184.6, 333.87) * mm});
            skLineSegment(sketch, "E1200", {"start": v(184.6, 333.87) * mm, "end": v(184.63, 334.24) * mm});
            skLineSegment(sketch, "E1201", {"start": v(184.63, 334.24) * mm, "end": v(184.66, 334.63) * mm});
            skLineSegment(sketch, "E1202", {"start": v(184.66, 334.63) * mm, "end": v(184.66, 340.74) * mm});
            skLineSegment(sketch, "E1203", {"start": v(184.66, 340.74) * mm, "end": v(184.66, 341.03) * mm});
            skLineSegment(sketch, "E1204", {"start": v(184.66, 341.03) * mm, "end": v(184.6, 341.31) * mm});
            skLineSegment(sketch, "E1205", {"start": v(184.6, 341.31) * mm, "end": v(184.54, 341.57) * mm});
            skLineSegment(sketch, "E1206", {"start": v(184.54, 341.57) * mm, "end": v(184.46, 341.82) * mm});
            skLineSegment(sketch, "E1207", {"start": v(184.46, 341.82) * mm, "end": v(184.35, 342.05) * mm});
            skLineSegment(sketch, "E1208", {"start": v(184.35, 342.05) * mm, "end": v(184.2, 342.28) * mm});
            skLineSegment(sketch, "E1209", {"start": v(184.2, 342.28) * mm, "end": v(184.06, 342.5) * mm});
            skLineSegment(sketch, "E1210", {"start": v(184.06, 342.5) * mm, "end": v(183.86, 342.7) * mm});
            skLineSegment(sketch, "E1211", {"start": v(183.86, 342.7) * mm, "end": v(183.66, 342.9) * mm});
            skLineSegment(sketch, "E1212", {"start": v(183.66, 342.9) * mm, "end": v(183.44, 343.07) * mm});
            skLineSegment(sketch, "E1213", {"start": v(183.44, 343.07) * mm, "end": v(183.2, 343.19) * mm});
            skLineSegment(sketch, "E1214", {"start": v(183.2, 343.19) * mm, "end": v(182.98, 343.3) * mm});
            skLineSegment(sketch, "E1215", {"start": v(182.98, 343.3) * mm, "end": v(182.73, 343.39) * mm});
            skLineSegment(sketch, "E1216", {"start": v(182.73, 343.39) * mm, "end": v(182.47, 343.47) * mm});
            skLineSegment(sketch, "E1217", {"start": v(182.47, 343.47) * mm, "end": v(182.19, 343.5) * mm});
            skLineSegment(sketch, "E1218", {"start": v(182.19, 343.5) * mm, "end": v(181.9, 343.5) * mm});
            skLineSegment(sketch, "E1219", {"start": v(181.9, 343.5) * mm, "end": v(181.87, 343.5) * mm});
            skLineSegment(sketch, "E1220", {"start": v(181.87, 343.5) * mm, "end": v(181.67, 343.53) * mm});
            skLineSegment(sketch, "E1221", {"start": v(181.67, 343.53) * mm, "end": v(181.45, 343.56) * mm});
            skLineSegment(sketch, "E1222", {"start": v(181.45, 343.56) * mm, "end": v(181.25, 343.61) * mm});
            skLineSegment(sketch, "E1223", {"start": v(181.25, 343.61) * mm, "end": v(181.05, 343.67) * mm});
            skLineSegment(sketch, "E1224", {"start": v(181.05, 343.67) * mm, "end": v(180.85, 343.78) * mm});
            skLineSegment(sketch, "E1225", {"start": v(180.85, 343.78) * mm, "end": v(180.65, 343.9) * mm});
            skLineSegment(sketch, "E1226", {"start": v(180.65, 343.9) * mm, "end": v(180.48, 344.01) * mm});
            skLineSegment(sketch, "E1227", {"start": v(180.48, 344.01) * mm, "end": v(180.31, 344.18) * mm});
            skLineSegment(sketch, "E1228", {"start": v(180.31, 344.18) * mm, "end": v(180.17, 344.35) * mm});
            skLineSegment(sketch, "E1229", {"start": v(180.17, 344.35) * mm, "end": v(180.03, 344.52) * mm});
            skLineSegment(sketch, "E1230", {"start": v(180.03, 344.52) * mm, "end": v(179.91, 344.72) * mm});
            skLineSegment(sketch, "E1231", {"start": v(179.91, 344.72) * mm, "end": v(179.83, 344.9) * mm});
            skLineSegment(sketch, "E1232", {"start": v(179.83, 344.9) * mm, "end": v(179.77, 345.09) * mm});
            skLineSegment(sketch, "E1233", {"start": v(179.77, 345.09) * mm, "end": v(179.71, 345.29) * mm});
            skLineSegment(sketch, "E1234", {"start": v(179.71, 345.29) * mm, "end": v(179.69, 345.52) * mm});
            skLineSegment(sketch, "E1235", {"start": v(179.69, 345.52) * mm, "end": v(179.66, 345.71) * mm});
            skLineSegment(sketch, "E1236", {"start": v(179.66, 345.71) * mm, "end": v(179.69, 345.94) * mm});
            skLineSegment(sketch, "E1237", {"start": v(179.69, 345.94) * mm, "end": v(179.71, 346.17) * mm});
            skLineSegment(sketch, "E1238", {"start": v(179.71, 346.17) * mm, "end": v(179.77, 346.37) * mm});
            skLineSegment(sketch, "E1239", {"start": v(179.77, 346.37) * mm, "end": v(179.83, 346.57) * mm});
            skLineSegment(sketch, "E1240", {"start": v(179.83, 346.57) * mm, "end": v(179.91, 346.77) * mm});
            skLineSegment(sketch, "E1241", {"start": v(179.91, 346.77) * mm, "end": v(180.03, 346.96) * mm});
            skLineSegment(sketch, "E1242", {"start": v(180.03, 346.96) * mm, "end": v(180.17, 347.14) * mm});
            skLineSegment(sketch, "E1243", {"start": v(180.17, 347.14) * mm, "end": v(180.31, 347.3) * mm});
            skLineSegment(sketch, "E1244", {"start": v(180.31, 347.3) * mm, "end": v(180.48, 347.45) * mm});
            skLineSegment(sketch, "E1245", {"start": v(180.48, 347.45) * mm, "end": v(180.65, 347.59) * mm});
            skLineSegment(sketch, "E1246", {"start": v(180.65, 347.59) * mm, "end": v(180.85, 347.7) * mm});
            skLineSegment(sketch, "E1247", {"start": v(180.85, 347.7) * mm, "end": v(181.05, 347.79) * mm});
            skLineSegment(sketch, "E1248", {"start": v(181.05, 347.79) * mm, "end": v(181.25, 347.85) * mm});
            skLineSegment(sketch, "E1249", {"start": v(181.25, 347.85) * mm, "end": v(181.45, 347.9) * mm});
            skLineSegment(sketch, "E1250", {"start": v(181.45, 347.9) * mm, "end": v(181.67, 347.93) * mm});
            skLineSegment(sketch, "E1251", {"start": v(181.67, 347.93) * mm, "end": v(181.87, 347.93) * mm});
            skLineSegment(sketch, "E1252", {"start": v(181.87, 347.93) * mm, "end": v(181.9, 347.93) * mm});
            skLineSegment(sketch, "E1253", {"start": v(181.9, 347.93) * mm, "end": v(182.19, 347.96) * mm});
            skLineSegment(sketch, "E1254", {"start": v(182.19, 347.96) * mm, "end": v(182.47, 347.99) * mm});
            skLineSegment(sketch, "E1255", {"start": v(182.47, 347.99) * mm, "end": v(182.73, 348.04) * mm});
            skLineSegment(sketch, "E1256", {"start": v(182.73, 348.04) * mm, "end": v(182.98, 348.16) * mm});
            skLineSegment(sketch, "E1257", {"start": v(182.98, 348.16) * mm, "end": v(183.2, 348.27) * mm});
            skLineSegment(sketch, "E1258", {"start": v(183.2, 348.27) * mm, "end": v(183.44, 348.39) * mm});
            skLineSegment(sketch, "E1259", {"start": v(183.44, 348.39) * mm, "end": v(183.66, 348.56) * mm});
            skLineSegment(sketch, "E1260", {"start": v(183.66, 348.56) * mm, "end": v(183.86, 348.75) * mm});
            skLineSegment(sketch, "E1261", {"start": v(183.86, 348.75) * mm, "end": v(184.06, 348.95) * mm});
            skLineSegment(sketch, "E1262", {"start": v(184.06, 348.95) * mm, "end": v(184.2, 349.18) * mm});
            skLineSegment(sketch, "E1263", {"start": v(184.2, 349.18) * mm, "end": v(184.35, 349.4) * mm});
            skLineSegment(sketch, "E1264", {"start": v(184.35, 349.4) * mm, "end": v(184.46, 349.64) * mm});
            skLineSegment(sketch, "E1265", {"start": v(184.46, 349.64) * mm, "end": v(184.54, 349.9) * mm});
            skLineSegment(sketch, "E1266", {"start": v(184.54, 349.9) * mm, "end": v(184.6, 350.15) * mm});
            skLineSegment(sketch, "E1267", {"start": v(184.6, 350.15) * mm, "end": v(184.66, 350.43) * mm});
            skLineSegment(sketch, "E1268", {"start": v(184.66, 350.43) * mm, "end": v(184.66, 350.71) * mm});
            skLineSegment(sketch, "E1269", {"start": v(184.66, 350.71) * mm, "end": v(184.66, 356.8) * mm});
            skLineSegment(sketch, "E1270", {"start": v(184.66, 356.8) * mm, "end": v(184.63, 357.2) * mm});
            skLineSegment(sketch, "E1271", {"start": v(184.63, 357.2) * mm, "end": v(184.6, 357.56) * mm});
            skLineSegment(sketch, "E1272", {"start": v(184.6, 357.56) * mm, "end": v(184.49, 357.93) * mm});
            skLineSegment(sketch, "E1273", {"start": v(184.49, 357.93) * mm, "end": v(184.37, 358.27) * mm});
            skLineSegment(sketch, "E1274", {"start": v(184.37, 358.27) * mm, "end": v(184.23, 358.61) * mm});
            skLineSegment(sketch, "E1275", {"start": v(184.23, 358.61) * mm, "end": v(184.03, 358.93) * mm});
            skLineSegment(sketch, "E1276", {"start": v(184.03, 358.93) * mm, "end": v(183.8, 359.24) * mm});
            skLineSegment(sketch, "E1277", {"start": v(183.8, 359.24) * mm, "end": v(183.52, 359.52) * mm});
            skLineSegment(sketch, "E1278", {"start": v(183.52, 359.52) * mm, "end": v(183.24, 359.78) * mm});
            skLineSegment(sketch, "E1279", {"start": v(183.24, 359.78) * mm, "end": v(182.95, 360.03) * mm});
            skLineSegment(sketch, "E1280", {"start": v(182.95, 360.03) * mm, "end": v(182.61, 360.2) * mm});
            skLineSegment(sketch, "E1281", {"start": v(182.61, 360.2) * mm, "end": v(182.27, 360.37) * mm});
            skLineSegment(sketch, "E1282", {"start": v(182.27, 360.37) * mm, "end": v(181.93, 360.49) * mm});
            skLineSegment(sketch, "E1283", {"start": v(181.93, 360.49) * mm, "end": v(181.56, 360.6) * mm});
            skLineSegment(sketch, "E1284", {"start": v(181.56, 360.6) * mm, "end": v(181.2, 360.63) * mm});
            skLineSegment(sketch, "E1285", {"start": v(181.2, 360.63) * mm, "end": v(180.77, 360.66) * mm});
            skLineSegment(sketch, "E1286", {"start": v(180.77, 360.66) * mm, "end": v(180.4, 360.63) * mm});
            skLineSegment(sketch, "E1287", {"start": v(180.4, 360.63) * mm, "end": v(180, 360.57) * mm});
            skLineSegment(sketch, "E1288", {"start": v(180, 360.57) * mm, "end": v(179.63, 360.49) * mm});
            skLineSegment(sketch, "E1289", {"start": v(179.63, 360.49) * mm, "end": v(179.29, 360.37) * mm});
            skLineSegment(sketch, "E1290", {"start": v(179.29, 360.37) * mm, "end": v(178.95, 360.2) * mm});
            skLineSegment(sketch, "E1291", {"start": v(178.95, 360.2) * mm, "end": v(178.6, 359.98) * mm});
            skLineSegment(sketch, "E1292", {"start": v(178.6, 359.98) * mm, "end": v(178.27, 359.75) * mm});
            skLineSegment(sketch, "E1293", {"start": v(178.27, 359.75) * mm, "end": v(177.95, 359.47) * mm});
            skLineSegment(sketch, "E1294", {"start": v(177.95, 359.47) * mm, "end": v(177.78, 359.32) * mm});
            skLineSegment(sketch, "E1295", {"start": v(177.78, 359.32) * mm, "end": v(177.61, 359.18) * mm});
            skLineSegment(sketch, "E1296", {"start": v(177.61, 359.18) * mm, "end": v(177.41, 359.07) * mm});
            skLineSegment(sketch, "E1297", {"start": v(177.41, 359.07) * mm, "end": v(177.21, 358.98) * mm});
            skLineSegment(sketch, "E1298", {"start": v(177.21, 358.98) * mm, "end": v(177.02, 358.9) * mm});
            skLineSegment(sketch, "E1299", {"start": v(177.02, 358.9) * mm, "end": v(176.82, 358.84) * mm});
            skLineSegment(sketch, "E1300", {"start": v(176.82, 358.84) * mm, "end": v(176.59, 358.81) * mm});
            skLineSegment(sketch, "E1301", {"start": v(176.59, 358.81) * mm, "end": v(176.36, 358.81) * mm});
            skLineSegment(sketch, "E1302", {"start": v(176.36, 358.81) * mm, "end": v(176.16, 358.81) * mm});
            skLineSegment(sketch, "E1303", {"start": v(176.16, 358.81) * mm, "end": v(175.94, 358.84) * mm});
            skLineSegment(sketch, "E1304", {"start": v(175.94, 358.84) * mm, "end": v(175.74, 358.9) * mm});
            skLineSegment(sketch, "E1305", {"start": v(175.74, 358.9) * mm, "end": v(175.54, 358.95) * mm});
            skLineSegment(sketch, "E1306", {"start": v(175.54, 358.95) * mm, "end": v(175.34, 359.07) * mm});
            skLineSegment(sketch, "E1307", {"start": v(175.34, 359.07) * mm, "end": v(175.14, 359.18) * mm});
            skLineSegment(sketch, "E1308", {"start": v(175.14, 359.18) * mm, "end": v(174.97, 359.3) * mm});
            skLineSegment(sketch, "E1309", {"start": v(174.97, 359.3) * mm, "end": v(174.8, 359.47) * mm});
            skLineSegment(sketch, "E1310", {"start": v(174.8, 359.47) * mm, "end": v(174.66, 359.6) * mm});
            skLineSegment(sketch, "E1311", {"start": v(174.66, 359.6) * mm, "end": v(174.52, 359.8) * mm});
            skLineSegment(sketch, "E1312", {"start": v(174.52, 359.8) * mm, "end": v(174.4, 359.98) * mm});
            skLineSegment(sketch, "E1313", {"start": v(174.4, 359.98) * mm, "end": v(174.32, 360.18) * mm});
            skLineSegment(sketch, "E1314", {"start": v(174.32, 360.18) * mm, "end": v(174.26, 360.37) * mm});
            skLineSegment(sketch, "E1315", {"start": v(174.26, 360.37) * mm, "end": v(174.2, 360.57) * mm});
            skLineSegment(sketch, "E1316", {"start": v(174.2, 360.57) * mm, "end": v(174.17, 360.8) * mm});
            skLineSegment(sketch, "E1317", {"start": v(174.17, 360.8) * mm, "end": v(174.15, 361.03) * mm});
            skLineSegment(sketch, "E1318", {"start": v(174.15, 361.03) * mm, "end": v(174.17, 361.23) * mm});
            skLineSegment(sketch, "E1319", {"start": v(174.17, 361.23) * mm, "end": v(174.2, 361.45) * mm});
            skLineSegment(sketch, "E1320", {"start": v(174.2, 361.45) * mm, "end": v(174.26, 361.65) * mm});
            skLineSegment(sketch, "E1321", {"start": v(174.26, 361.65) * mm, "end": v(174.32, 361.85) * mm});
            skLineSegment(sketch, "E1322", {"start": v(174.32, 361.85) * mm, "end": v(174.43, 362.05) * mm});
            skLineSegment(sketch, "E1323", {"start": v(174.43, 362.05) * mm, "end": v(174.54, 362.22) * mm});
            skLineSegment(sketch, "E1324", {"start": v(174.54, 362.22) * mm, "end": v(174.66, 362.4) * mm});
            skLineSegment(sketch, "E1325", {"start": v(174.66, 362.4) * mm, "end": v(174.83, 362.56) * mm});
            skLineSegment(sketch, "E1326", {"start": v(174.83, 362.56) * mm, "end": v(175.48, 363.16) * mm});
            skLineSegment(sketch, "E1327", {"start": v(175.48, 363.16) * mm, "end": v(176.13, 363.7) * mm});
            skLineSegment(sketch, "E1328", {"start": v(176.13, 363.7) * mm, "end": v(176.85, 364.12) * mm});
            skLineSegment(sketch, "E1329", {"start": v(176.85, 364.12) * mm, "end": v(177.58, 364.5) * mm});
            skLineSegment(sketch, "E1330", {"start": v(177.58, 364.5) * mm, "end": v(178.32, 364.75) * mm});
            skLineSegment(sketch, "E1331", {"start": v(178.32, 364.75) * mm, "end": v(179.12, 364.95) * mm});
            skLineSegment(sketch, "E1332", {"start": v(179.12, 364.95) * mm, "end": v(179.94, 365.1) * mm});
            skLineSegment(sketch, "E1333", {"start": v(179.94, 365.1) * mm, "end": v(180.77, 365.12) * mm});
            skLineSegment(sketch, "E1334", {"start": v(180.77, 365.12) * mm, "end": v(181.62, 365.1) * mm});
            skLineSegment(sketch, "E1335", {"start": v(181.62, 365.1) * mm, "end": v(182.44, 364.98) * mm});
            skLineSegment(sketch, "E1336", {"start": v(182.44, 364.98) * mm, "end": v(183.2, 364.78) * mm});
            skLineSegment(sketch, "E1337", {"start": v(183.2, 364.78) * mm, "end": v(183.98, 364.52) * mm});
            skLineSegment(sketch, "E1338", {"start": v(183.98, 364.52) * mm, "end": v(184.69, 364.15) * mm});
            skLineSegment(sketch, "E1339", {"start": v(184.69, 364.15) * mm, "end": v(185.37, 363.75) * mm});
            skLineSegment(sketch, "E1340", {"start": v(185.37, 363.75) * mm, "end": v(186.02, 363.24) * mm});
            skLineSegment(sketch, "E1341", {"start": v(186.02, 363.24) * mm, "end": v(186.65, 362.68) * mm});
            skLineSegment(sketch, "E1342", {"start": v(186.65, 362.68) * mm, "end": v(187.21, 362.05) * mm});
            skLineSegment(sketch, "E1343", {"start": v(187.21, 362.05) * mm, "end": v(187.73, 361.4) * mm});
            skLineSegment(sketch, "E1344", {"start": v(187.73, 361.4) * mm, "end": v(188.12, 360.72) * mm});
            skLineSegment(sketch, "E1345", {"start": v(188.12, 360.72) * mm, "end": v(188.5, 360) * mm});
            skLineSegment(sketch, "E1346", {"start": v(188.5, 360) * mm, "end": v(188.75, 359.24) * mm});
            skLineSegment(sketch, "E1347", {"start": v(188.75, 359.24) * mm, "end": v(188.95, 358.47) * mm});
            skLineSegment(sketch, "E1348", {"start": v(188.95, 358.47) * mm, "end": v(189.06, 357.65) * mm});
            skLineSegment(sketch, "E1349", {"start": v(189.06, 357.65) * mm, "end": v(189.09, 356.8) * mm});
            skLineSegment(sketch, "E1350", {"start": v(189.09, 356.8) * mm, "end": v(189.09, 350.71) * mm});
            skLineSegment(sketch, "E1351", {"start": v(189.09, 350.71) * mm, "end": v(189.06, 349.98) * mm});
            skLineSegment(sketch, "E1352", {"start": v(189.06, 349.98) * mm, "end": v(188.98, 349.3) * mm});
            skLineSegment(sketch, "E1353", {"start": v(188.98, 349.3) * mm, "end": v(188.8, 348.61) * mm});
            skLineSegment(sketch, "E1354", {"start": v(188.8, 348.61) * mm, "end": v(188.58, 347.99) * mm});
            skLineSegment(sketch, "E1355", {"start": v(188.58, 347.99) * mm, "end": v(188.3, 347.4) * mm});
            skLineSegment(sketch, "E1356", {"start": v(188.3, 347.4) * mm, "end": v(187.95, 346.8) * mm});
            skLineSegment(sketch, "E1357", {"start": v(187.95, 346.8) * mm, "end": v(187.53, 346.25) * mm});
            skLineSegment(sketch, "E1358", {"start": v(187.53, 346.25) * mm, "end": v(187.07, 345.71) * mm});
            skLineSegment(sketch, "E1359", {"start": v(187.07, 345.71) * mm, "end": v(187.53, 345.2) * mm});
            skLineSegment(sketch, "E1360", {"start": v(187.53, 345.2) * mm, "end": v(187.95, 344.66) * mm});
            skLineSegment(sketch, "E1361", {"start": v(187.95, 344.66) * mm, "end": v(188.3, 344.07) * mm});
            skLineSegment(sketch, "E1362", {"start": v(188.3, 344.07) * mm, "end": v(188.58, 343.47) * mm});
            skLineSegment(sketch, "E1363", {"start": v(188.58, 343.47) * mm, "end": v(188.8, 342.85) * mm});
            skLineSegment(sketch, "E1364", {"start": v(188.8, 342.85) * mm, "end": v(188.98, 342.16) * mm});
            skLineSegment(sketch, "E1365", {"start": v(188.98, 342.16) * mm, "end": v(189.06, 341.48) * mm});
            skLineSegment(sketch, "E1366", {"start": v(189.06, 341.48) * mm, "end": v(189.09, 340.74) * mm});
            skLineSegment(sketch, "E1367", {"start": v(189.09, 340.74) * mm, "end": v(189.09, 334.63) * mm});
            skLineSegment(sketch, "E1368", {"start": v(189.09, 334.63) * mm, "end": v(189.06, 333.78) * mm});
            skLineSegment(sketch, "E1369", {"start": v(189.06, 333.78) * mm, "end": v(188.95, 332.96) * mm});
            skLineSegment(sketch, "E1370", {"start": v(188.95, 332.96) * mm, "end": v(188.75, 332.2) * mm});
            skLineSegment(sketch, "E1371", {"start": v(188.75, 332.2) * mm, "end": v(188.5, 331.42) * mm});
            skLineSegment(sketch, "E1372", {"start": v(188.5, 331.42) * mm, "end": v(188.12, 330.71) * mm});
            skLineSegment(sketch, "E1373", {"start": v(188.12, 330.71) * mm, "end": v(187.73, 330.03) * mm});
            skLineSegment(sketch, "E1374", {"start": v(187.73, 330.03) * mm, "end": v(187.21, 329.38) * mm});
            skLineSegment(sketch, "E1375", {"start": v(187.21, 329.38) * mm, "end": v(186.65, 328.75) * mm});
            skLineSegment(sketch, "E1376", {"start": v(186.65, 328.75) * mm, "end": v(186.02, 328.19) * mm});
            skLineSegment(sketch, "E1377", {"start": v(186.02, 328.19) * mm, "end": v(185.37, 327.67) * mm});
            skLineSegment(sketch, "E1378", {"start": v(185.37, 327.67) * mm, "end": v(184.69, 327.28) * mm});
            skLineSegment(sketch, "E1379", {"start": v(184.69, 327.28) * mm, "end": v(183.98, 326.9) * mm});
            skLineSegment(sketch, "E1380", {"start": v(183.98, 326.9) * mm, "end": v(183.2, 326.65) * mm});
            skLineSegment(sketch, "E1381", {"start": v(183.2, 326.65) * mm, "end": v(182.44, 326.45) * mm});
            skLineSegment(sketch, "E1382", {"start": v(182.44, 326.45) * mm, "end": v(181.62, 326.34) * mm});
            skLineSegment(sketch, "E1383", {"start": v(181.62, 326.34) * mm, "end": v(180.77, 326.31) * mm});
            skLineSegment(sketch, "E1384", {"start": v(180.77, 326.31) * mm, "end": v(179.94, 326.34) * mm});
            skLineSegment(sketch, "E1385", {"start": v(179.94, 326.34) * mm, "end": v(179.12, 326.48) * mm});
            skLineSegment(sketch, "E1386", {"start": v(179.12, 326.48) * mm, "end": v(178.32, 326.68) * mm});
            skLineSegment(sketch, "E1387", {"start": v(178.32, 326.68) * mm, "end": v(177.58, 326.94) * mm});
            skLineSegment(sketch, "E1388", {"start": v(177.58, 326.94) * mm, "end": v(176.85, 327.3) * mm});
            skLineSegment(sketch, "E1389", {"start": v(176.85, 327.3) * mm, "end": v(176.13, 327.73) * mm});
            skLineSegment(sketch, "E1390", {"start": v(176.13, 327.73) * mm, "end": v(175.48, 328.27) * mm});
            skLineSegment(sketch, "E1391", {"start": v(175.48, 328.27) * mm, "end": v(174.83, 328.87) * mm});
            skLineSegment(sketch, "E1392", {"start": v(174.83, 328.87) * mm, "end": v(174.66, 329.04) * mm});
            skLineSegment(sketch, "E1393", {"start": v(174.66, 329.04) * mm, "end": v(174.54, 329.2) * mm});
            skLineSegment(sketch, "E1394", {"start": v(174.54, 329.2) * mm, "end": v(174.43, 329.38) * mm});
            skLineSegment(sketch, "E1395", {"start": v(174.43, 329.38) * mm, "end": v(174.32, 329.58) * mm});
            skLineSegment(sketch, "E1396", {"start": v(174.32, 329.58) * mm, "end": v(174.26, 329.78) * mm});
            skLineSegment(sketch, "E1397", {"start": v(174.26, 329.78) * mm, "end": v(174.2, 329.98) * mm});
            skLineSegment(sketch, "E1398", {"start": v(174.2, 329.98) * mm, "end": v(174.17, 330.2) * mm});
            skLineSegment(sketch, "E1399", {"start": v(195.2, 333.78) * mm, "end": v(195.14, 334.63) * mm});
            skLineSegment(sketch, "E1400", {"start": v(195.14, 334.63) * mm, "end": v(195.14, 342.36) * mm});
            skLineSegment(sketch, "E1401", {"start": v(195.14, 342.36) * mm, "end": v(195.17, 342.56) * mm});
            skLineSegment(sketch, "E1402", {"start": v(195.17, 342.56) * mm, "end": v(195.2, 342.79) * mm});
            skLineSegment(sketch, "E1403", {"start": v(195.2, 342.79) * mm, "end": v(195.25, 342.99) * mm});
            skLineSegment(sketch, "E1404", {"start": v(195.25, 342.99) * mm, "end": v(195.31, 343.19) * mm});
            skLineSegment(sketch, "E1405", {"start": v(195.31, 343.19) * mm, "end": v(195.4, 343.39) * mm});
            skLineSegment(sketch, "E1406", {"start": v(195.4, 343.39) * mm, "end": v(195.51, 343.58) * mm});
            skLineSegment(sketch, "E1407", {"start": v(195.51, 343.58) * mm, "end": v(195.65, 343.75) * mm});
            skLineSegment(sketch, "E1408", {"start": v(195.65, 343.75) * mm, "end": v(195.8, 343.92) * mm});
            skLineSegment(sketch, "E1409", {"start": v(195.8, 343.92) * mm, "end": v(195.96, 344.07) * mm});
            skLineSegment(sketch, "E1410", {"start": v(195.96, 344.07) * mm, "end": v(196.14, 344.2) * mm});
            skLineSegment(sketch, "E1411", {"start": v(196.14, 344.2) * mm, "end": v(196.33, 344.32) * mm});
            skLineSegment(sketch, "E1412", {"start": v(196.33, 344.32) * mm, "end": v(196.53, 344.4) * mm});
            skLineSegment(sketch, "E1413", {"start": v(196.53, 344.4) * mm, "end": v(196.73, 344.46) * mm});
            skLineSegment(sketch, "E1414", {"start": v(196.73, 344.46) * mm, "end": v(196.93, 344.52) * mm});
            skLineSegment(sketch, "E1415", {"start": v(196.93, 344.52) * mm, "end": v(197.16, 344.55) * mm});
            skLineSegment(sketch, "E1416", {"start": v(197.16, 344.55) * mm, "end": v(197.36, 344.58) * mm});
            skLineSegment(sketch, "E1417", {"start": v(197.36, 344.58) * mm, "end": v(197.58, 344.55) * mm});
            skLineSegment(sketch, "E1418", {"start": v(197.58, 344.55) * mm, "end": v(197.81, 344.52) * mm});
            skLineSegment(sketch, "E1419", {"start": v(197.81, 344.52) * mm, "end": v(198.01, 344.46) * mm});
            skLineSegment(sketch, "E1420", {"start": v(198.01, 344.46) * mm, "end": v(198.2, 344.4) * mm});
            skLineSegment(sketch, "E1421", {"start": v(198.2, 344.4) * mm, "end": v(198.4, 344.32) * mm});
            skLineSegment(sketch, "E1422", {"start": v(198.4, 344.32) * mm, "end": v(198.6, 344.2) * mm});
            skLineSegment(sketch, "E1423", {"start": v(198.6, 344.2) * mm, "end": v(198.78, 344.07) * mm});
            skLineSegment(sketch, "E1424", {"start": v(198.78, 344.07) * mm, "end": v(198.95, 343.92) * mm});
            skLineSegment(sketch, "E1425", {"start": v(198.95, 343.92) * mm, "end": v(199.09, 343.75) * mm});
            skLineSegment(sketch, "E1426", {"start": v(199.09, 343.75) * mm, "end": v(199.23, 343.58) * mm});
            skLineSegment(sketch, "E1427", {"start": v(199.23, 343.58) * mm, "end": v(199.35, 343.39) * mm});
            skLineSegment(sketch, "E1428", {"start": v(199.35, 343.39) * mm, "end": v(199.43, 343.19) * mm});
            skLineSegment(sketch, "E1429", {"start": v(199.43, 343.19) * mm, "end": v(199.49, 342.99) * mm});
            skLineSegment(sketch, "E1430", {"start": v(199.49, 342.99) * mm, "end": v(199.54, 342.79) * mm});
            skLineSegment(sketch, "E1431", {"start": v(199.54, 342.79) * mm, "end": v(199.57, 342.56) * mm});
            skLineSegment(sketch, "E1432", {"start": v(199.57, 342.56) * mm, "end": v(199.57, 342.36) * mm});
            skLineSegment(sketch, "E1433", {"start": v(199.57, 342.36) * mm, "end": v(199.57, 334.63) * mm});
            skLineSegment(sketch, "E1434", {"start": v(199.57, 334.63) * mm, "end": v(199.6, 334.24) * mm});
            skLineSegment(sketch, "E1435", {"start": v(199.6, 334.24) * mm, "end": v(199.66, 333.84) * mm});
            skLineSegment(sketch, "E1436", {"start": v(199.66, 333.84) * mm, "end": v(199.74, 333.47) * mm});
            skLineSegment(sketch, "E1437", {"start": v(199.74, 333.47) * mm, "end": v(199.86, 333.13) * mm});
            skLineSegment(sketch, "E1438", {"start": v(199.86, 333.13) * mm, "end": v(200.03, 332.79) * mm});
            skLineSegment(sketch, "E1439", {"start": v(200.03, 332.79) * mm, "end": v(200.23, 332.48) * mm});
            skLineSegment(sketch, "E1440", {"start": v(200.23, 332.48) * mm, "end": v(200.45, 332.16) * mm});
            skLineSegment(sketch, "E1441", {"start": v(200.45, 332.16) * mm, "end": v(200.7, 331.88) * mm});
            skLineSegment(sketch, "E1442", {"start": v(200.7, 331.88) * mm, "end": v(201.02, 331.62) * mm});
            skLineSegment(sketch, "E1443", {"start": v(201.02, 331.62) * mm, "end": v(201.33, 331.37) * mm});
            skLineSegment(sketch, "E1444", {"start": v(201.33, 331.37) * mm, "end": v(201.65, 331.2) * mm});
            skLineSegment(sketch, "E1445", {"start": v(201.65, 331.2) * mm, "end": v(201.99, 331.03) * mm});
            skLineSegment(sketch, "E1446", {"start": v(201.99, 331.03) * mm, "end": v(202.33, 330.91) * mm});
            skLineSegment(sketch, "E1447", {"start": v(202.33, 330.91) * mm, "end": v(202.7, 330.8) * mm});
            skLineSegment(sketch, "E1448", {"start": v(202.7, 330.8) * mm, "end": v(203.07, 330.77) * mm});
            skLineSegment(sketch, "E1449", {"start": v(203.07, 330.77) * mm, "end": v(203.47, 330.74) * mm});
            skLineSegment(sketch, "E1450", {"start": v(203.47, 330.74) * mm, "end": v(203.86, 330.77) * mm});
            skLineSegment(sketch, "E1451", {"start": v(203.86, 330.77) * mm, "end": v(204.23, 330.8) * mm});
            skLineSegment(sketch, "E1452", {"start": v(204.23, 330.8) * mm, "end": v(204.6, 330.91) * mm});
            skLineSegment(sketch, "E1453", {"start": v(204.6, 330.91) * mm, "end": v(204.94, 331.03) * mm});
            skLineSegment(sketch, "E1454", {"start": v(204.94, 331.03) * mm, "end": v(205.28, 331.2) * mm});
            skLineSegment(sketch, "E1455", {"start": v(205.28, 331.2) * mm, "end": v(205.6, 331.37) * mm});
            skLineSegment(sketch, "E1456", {"start": v(205.6, 331.37) * mm, "end": v(205.9, 331.62) * mm});
            skLineSegment(sketch, "E1457", {"start": v(205.9, 331.62) * mm, "end": v(206.22, 331.88) * mm});
            skLineSegment(sketch, "E1458", {"start": v(206.22, 331.88) * mm, "end": v(206.48, 332.16) * mm});
            skLineSegment(sketch, "E1459", {"start": v(206.48, 332.16) * mm, "end": v(206.7, 332.48) * mm});
            skLineSegment(sketch, "E1460", {"start": v(206.7, 332.48) * mm, "end": v(206.9, 332.79) * mm});
            skLineSegment(sketch, "E1461", {"start": v(206.9, 332.79) * mm, "end": v(207.07, 333.13) * mm});
            skLineSegment(sketch, "E1462", {"start": v(207.07, 333.13) * mm, "end": v(207.19, 333.47) * mm});
            skLineSegment(sketch, "E1463", {"start": v(207.19, 333.47) * mm, "end": v(207.27, 333.84) * mm});
            skLineSegment(sketch, "E1464", {"start": v(207.27, 333.84) * mm, "end": v(207.33, 334.24) * mm});
            skLineSegment(sketch, "E1465", {"start": v(207.33, 334.24) * mm, "end": v(207.36, 334.63) * mm});
            skLineSegment(sketch, "E1466", {"start": v(207.36, 334.63) * mm, "end": v(207.36, 342.36) * mm});
            skLineSegment(sketch, "E1467", {"start": v(207.36, 342.36) * mm, "end": v(207.36, 342.56) * mm});
            skLineSegment(sketch, "E1468", {"start": v(207.36, 342.56) * mm, "end": v(207.39, 342.79) * mm});
            skLineSegment(sketch, "E1469", {"start": v(207.39, 342.79) * mm, "end": v(207.44, 342.99) * mm});
            skLineSegment(sketch, "E1470", {"start": v(207.44, 342.99) * mm, "end": v(207.5, 343.19) * mm});
            skLineSegment(sketch, "E1471", {"start": v(207.5, 343.19) * mm, "end": v(207.58, 343.39) * mm});
            skLineSegment(sketch, "E1472", {"start": v(207.58, 343.39) * mm, "end": v(207.7, 343.58) * mm});
            skLineSegment(sketch, "E1473", {"start": v(207.7, 343.58) * mm, "end": v(207.84, 343.75) * mm});
            skLineSegment(sketch, "E1474", {"start": v(207.84, 343.75) * mm, "end": v(207.98, 343.92) * mm});
            skLineSegment(sketch, "E1475", {"start": v(207.98, 343.92) * mm, "end": v(208.15, 344.07) * mm});
            skLineSegment(sketch, "E1476", {"start": v(208.15, 344.07) * mm, "end": v(208.32, 344.2) * mm});
            skLineSegment(sketch, "E1477", {"start": v(208.32, 344.2) * mm, "end": v(208.52, 344.32) * mm});
            skLineSegment(sketch, "E1478", {"start": v(208.52, 344.32) * mm, "end": v(208.72, 344.4) * mm});
            skLineSegment(sketch, "E1479", {"start": v(208.72, 344.4) * mm, "end": v(208.92, 344.46) * mm});
            skLineSegment(sketch, "E1480", {"start": v(208.92, 344.46) * mm, "end": v(209.12, 344.52) * mm});
            skLineSegment(sketch, "E1481", {"start": v(209.12, 344.52) * mm, "end": v(209.35, 344.55) * mm});
            skLineSegment(sketch, "E1482", {"start": v(209.35, 344.55) * mm, "end": v(209.57, 344.58) * mm});
            skLineSegment(sketch, "E1483", {"start": v(209.57, 344.58) * mm, "end": v(209.77, 344.55) * mm});
            skLineSegment(sketch, "E1484", {"start": v(209.77, 344.55) * mm, "end": v(210, 344.52) * mm});
            skLineSegment(sketch, "E1485", {"start": v(210, 344.52) * mm, "end": v(210.2, 344.46) * mm});
            skLineSegment(sketch, "E1486", {"start": v(210.2, 344.46) * mm, "end": v(210.4, 344.4) * mm});
            skLineSegment(sketch, "E1487", {"start": v(210.4, 344.4) * mm, "end": v(210.6, 344.32) * mm});
            skLineSegment(sketch, "E1488", {"start": v(210.6, 344.32) * mm, "end": v(210.8, 344.2) * mm});
            skLineSegment(sketch, "E1489", {"start": v(210.8, 344.2) * mm, "end": v(210.97, 344.07) * mm});
            skLineSegment(sketch, "E1490", {"start": v(210.97, 344.07) * mm, "end": v(211.14, 343.92) * mm});
            skLineSegment(sketch, "E1491", {"start": v(211.14, 343.92) * mm, "end": v(211.28, 343.75) * mm});
            skLineSegment(sketch, "E1492", {"start": v(211.28, 343.75) * mm, "end": v(211.42, 343.58) * mm});
            skLineSegment(sketch, "E1493", {"start": v(211.42, 343.58) * mm, "end": v(211.53, 343.39) * mm});
            skLineSegment(sketch, "E1494", {"start": v(211.53, 343.39) * mm, "end": v(211.62, 343.19) * mm});
            skLineSegment(sketch, "E1495", {"start": v(211.62, 343.19) * mm, "end": v(211.68, 342.99) * mm});
            skLineSegment(sketch, "E1496", {"start": v(211.68, 342.99) * mm, "end": v(211.73, 342.79) * mm});
            skLineSegment(sketch, "E1497", {"start": v(211.73, 342.79) * mm, "end": v(211.76, 342.56) * mm});
            skLineSegment(sketch, "E1498", {"start": v(211.76, 342.56) * mm, "end": v(211.79, 342.36) * mm});
            skLineSegment(sketch, "E1499", {"start": v(211.79, 342.36) * mm, "end": v(211.79, 334.63) * mm});
            skLineSegment(sketch, "E1500", {"start": v(211.79, 334.63) * mm, "end": v(211.73, 333.78) * mm});
            skLineSegment(sketch, "E1501", {"start": v(211.73, 333.78) * mm, "end": v(211.62, 332.96) * mm});
            skLineSegment(sketch, "E1502", {"start": v(211.62, 332.96) * mm, "end": v(211.42, 332.2) * mm});
            skLineSegment(sketch, "E1503", {"start": v(211.42, 332.2) * mm, "end": v(211.16, 331.42) * mm});
            skLineSegment(sketch, "E1504", {"start": v(211.16, 331.42) * mm, "end": v(210.82, 330.71) * mm});
            skLineSegment(sketch, "E1505", {"start": v(210.82, 330.71) * mm, "end": v(210.4, 330.03) * mm});
            skLineSegment(sketch, "E1506", {"start": v(210.4, 330.03) * mm, "end": v(209.91, 329.38) * mm});
            skLineSegment(sketch, "E1507", {"start": v(209.91, 329.38) * mm, "end": v(209.35, 328.75) * mm});
            skLineSegment(sketch, "E1508", {"start": v(209.35, 328.75) * mm, "end": v(208.72, 328.19) * mm});
            skLineSegment(sketch, "E1509", {"start": v(208.72, 328.19) * mm, "end": v(208.07, 327.67) * mm});
            skLineSegment(sketch, "E1510", {"start": v(208.07, 327.67) * mm, "end": v(207.36, 327.28) * mm});
            skLineSegment(sketch, "E1511", {"start": v(207.36, 327.28) * mm, "end": v(206.65, 326.9) * mm});
            skLineSegment(sketch, "E1512", {"start": v(206.65, 326.9) * mm, "end": v(205.9, 326.65) * mm});
            skLineSegment(sketch, "E1513", {"start": v(205.9, 326.65) * mm, "end": v(205.11, 326.45) * mm});
            skLineSegment(sketch, "E1514", {"start": v(205.11, 326.45) * mm, "end": v(204.32, 326.34) * mm});
            skLineSegment(sketch, "E1515", {"start": v(204.32, 326.34) * mm, "end": v(203.47, 326.31) * mm});
            skLineSegment(sketch, "E1516", {"start": v(203.47, 326.31) * mm, "end": v(202.61, 326.34) * mm});
            skLineSegment(sketch, "E1517", {"start": v(202.61, 326.34) * mm, "end": v(201.82, 326.45) * mm});
            skLineSegment(sketch, "E1518", {"start": v(201.82, 326.45) * mm, "end": v(201.02, 326.65) * mm});
            skLineSegment(sketch, "E1519", {"start": v(201.02, 326.65) * mm, "end": v(200.28, 326.9) * mm});
            skLineSegment(sketch, "E1520", {"start": v(200.28, 326.9) * mm, "end": v(199.57, 327.28) * mm});
            skLineSegment(sketch, "E1521", {"start": v(199.57, 327.28) * mm, "end": v(198.86, 327.67) * mm});
            skLineSegment(sketch, "E1522", {"start": v(198.86, 327.67) * mm, "end": v(198.2, 328.19) * mm});
            skLineSegment(sketch, "E1523", {"start": v(198.2, 328.19) * mm, "end": v(197.58, 328.75) * mm});
            skLineSegment(sketch, "E1524", {"start": v(197.58, 328.75) * mm, "end": v(197.02, 329.38) * mm});
            skLineSegment(sketch, "E1525", {"start": v(197.02, 329.38) * mm, "end": v(196.53, 330.03) * mm});
            skLineSegment(sketch, "E1526", {"start": v(196.53, 330.03) * mm, "end": v(196.1, 330.71) * mm});
            skLineSegment(sketch, "E1527", {"start": v(196.1, 330.71) * mm, "end": v(195.77, 331.42) * mm});
            skLineSegment(sketch, "E1528", {"start": v(195.77, 331.42) * mm, "end": v(195.51, 332.2) * mm});
            skLineSegment(sketch, "E1529", {"start": v(195.51, 332.2) * mm, "end": v(195.31, 332.96) * mm});
            skLineSegment(sketch, "E1530", {"start": v(195.31, 332.96) * mm, "end": v(195.2, 333.78) * mm});
            skLineSegment(sketch, "E1531", {"start": v(195.2, 357.65) * mm, "end": v(195.31, 358.47) * mm});
            skLineSegment(sketch, "E1532", {"start": v(195.31, 358.47) * mm, "end": v(195.51, 359.24) * mm});
            skLineSegment(sketch, "E1533", {"start": v(195.51, 359.24) * mm, "end": v(195.77, 360) * mm});
            skLineSegment(sketch, "E1534", {"start": v(195.77, 360) * mm, "end": v(196.1, 360.72) * mm});
            skLineSegment(sketch, "E1535", {"start": v(196.1, 360.72) * mm, "end": v(196.53, 361.4) * mm});
            skLineSegment(sketch, "E1536", {"start": v(196.53, 361.4) * mm, "end": v(197.02, 362.05) * mm});
            skLineSegment(sketch, "E1537", {"start": v(197.02, 362.05) * mm, "end": v(197.58, 362.68) * mm});
            skLineSegment(sketch, "E1538", {"start": v(197.58, 362.68) * mm, "end": v(198.2, 363.24) * mm});
            skLineSegment(sketch, "E1539", {"start": v(198.2, 363.24) * mm, "end": v(198.86, 363.75) * mm});
            skLineSegment(sketch, "E1540", {"start": v(198.86, 363.75) * mm, "end": v(199.57, 364.15) * mm});
            skLineSegment(sketch, "E1541", {"start": v(199.57, 364.15) * mm, "end": v(200.28, 364.52) * mm});
            skLineSegment(sketch, "E1542", {"start": v(200.28, 364.52) * mm, "end": v(201.02, 364.78) * mm});
            skLineSegment(sketch, "E1543", {"start": v(201.02, 364.78) * mm, "end": v(201.82, 364.98) * mm});
            skLineSegment(sketch, "E1544", {"start": v(201.82, 364.98) * mm, "end": v(202.61, 365.1) * mm});
            skLineSegment(sketch, "E1545", {"start": v(202.61, 365.1) * mm, "end": v(203.47, 365.12) * mm});
            skLineSegment(sketch, "E1546", {"start": v(203.47, 365.12) * mm, "end": v(204.32, 365.1) * mm});
            skLineSegment(sketch, "E1547", {"start": v(204.32, 365.1) * mm, "end": v(205.11, 364.98) * mm});
            skLineSegment(sketch, "E1548", {"start": v(205.11, 364.98) * mm, "end": v(205.9, 364.78) * mm});
            skLineSegment(sketch, "E1549", {"start": v(205.9, 364.78) * mm, "end": v(206.65, 364.52) * mm});
            skLineSegment(sketch, "E1550", {"start": v(206.65, 364.52) * mm, "end": v(207.36, 364.15) * mm});
            skLineSegment(sketch, "E1551", {"start": v(207.36, 364.15) * mm, "end": v(208.07, 363.75) * mm});
            skLineSegment(sketch, "E1552", {"start": v(208.07, 363.75) * mm, "end": v(208.72, 363.24) * mm});
            skLineSegment(sketch, "E1553", {"start": v(208.72, 363.24) * mm, "end": v(209.35, 362.68) * mm});
            skLineSegment(sketch, "E1554", {"start": v(209.91, 362.05) * mm, "end": v(210.4, 361.4) * mm});
            skLineSegment(sketch, "E1555", {"start": v(210.4, 361.4) * mm, "end": v(210.82, 360.72) * mm});
            skLineSegment(sketch, "E1556", {"start": v(210.82, 360.72) * mm, "end": v(211.16, 360) * mm});
            skLineSegment(sketch, "E1557", {"start": v(211.16, 360) * mm, "end": v(211.42, 359.24) * mm});
            skLineSegment(sketch, "E1558", {"start": v(211.42, 359.24) * mm, "end": v(211.62, 358.47) * mm});
            skLineSegment(sketch, "E1559", {"start": v(211.62, 358.47) * mm, "end": v(211.73, 357.65) * mm});
            skLineSegment(sketch, "E1560", {"start": v(211.73, 357.65) * mm, "end": v(211.79, 356.8) * mm});
            skLineSegment(sketch, "E1561", {"start": v(211.79, 356.8) * mm, "end": v(211.79, 349.07) * mm});
            skLineSegment(sketch, "E1562", {"start": v(211.79, 349.07) * mm, "end": v(211.76, 348.87) * mm});
            skLineSegment(sketch, "E1563", {"start": v(211.76, 348.87) * mm, "end": v(211.73, 348.64) * mm});
            skLineSegment(sketch, "E1564", {"start": v(211.73, 348.64) * mm, "end": v(211.68, 348.44) * mm});
            skLineSegment(sketch, "E1565", {"start": v(211.68, 348.44) * mm, "end": v(211.62, 348.24) * mm});
            skLineSegment(sketch, "E1566", {"start": v(211.62, 348.24) * mm, "end": v(211.53, 348.04) * mm});
            skLineSegment(sketch, "E1567", {"start": v(211.53, 348.04) * mm, "end": v(211.42, 347.85) * mm});
            skLineSegment(sketch, "E1568", {"start": v(211.42, 347.85) * mm, "end": v(211.28, 347.67) * mm});
            skLineSegment(sketch, "E1569", {"start": v(211.28, 347.67) * mm, "end": v(211.14, 347.5) * mm});
            skLineSegment(sketch, "E1570", {"start": v(211.14, 347.5) * mm, "end": v(210.97, 347.36) * mm});
            skLineSegment(sketch, "E1571", {"start": v(210.97, 347.36) * mm, "end": v(210.8, 347.22) * mm});
            skLineSegment(sketch, "E1572", {"start": v(210.8, 347.22) * mm, "end": v(210.6, 347.1) * mm});
            skLineSegment(sketch, "E1573", {"start": v(210.6, 347.1) * mm, "end": v(210.4, 347.02) * mm});
            skLineSegment(sketch, "E1574", {"start": v(210.4, 347.02) * mm, "end": v(210.2, 346.96) * mm});
            skLineSegment(sketch, "E1575", {"start": v(210.2, 346.96) * mm, "end": v(210, 346.9) * mm});
            skLineSegment(sketch, "E1576", {"start": v(210, 346.9) * mm, "end": v(209.77, 346.88) * mm});
            skLineSegment(sketch, "E1577", {"start": v(209.77, 346.88) * mm, "end": v(209.57, 346.85) * mm});
            skLineSegment(sketch, "E1578", {"start": v(209.57, 346.85) * mm, "end": v(209.35, 346.88) * mm});
            skLineSegment(sketch, "E1579", {"start": v(209.35, 346.88) * mm, "end": v(209.12, 346.9) * mm});
            skLineSegment(sketch, "E1580", {"start": v(209.12, 346.9) * mm, "end": v(208.92, 346.96) * mm});
            skLineSegment(sketch, "E1581", {"start": v(208.92, 346.96) * mm, "end": v(208.72, 347.02) * mm});
            skLineSegment(sketch, "E1582", {"start": v(208.72, 347.02) * mm, "end": v(208.52, 347.1) * mm});
            skLineSegment(sketch, "E1583", {"start": v(208.52, 347.1) * mm, "end": v(208.32, 347.22) * mm});
            skLineSegment(sketch, "E1584", {"start": v(208.32, 347.22) * mm, "end": v(208.15, 347.36) * mm});
            skLineSegment(sketch, "E1585", {"start": v(208.15, 347.36) * mm, "end": v(207.98, 347.5) * mm});
            skLineSegment(sketch, "E1586", {"start": v(207.98, 347.5) * mm, "end": v(207.84, 347.67) * mm});
            skLineSegment(sketch, "E1587", {"start": v(207.84, 347.67) * mm, "end": v(207.7, 347.85) * mm});
            skLineSegment(sketch, "E1588", {"start": v(207.7, 347.85) * mm, "end": v(207.58, 348.04) * mm});
            skLineSegment(sketch, "E1589", {"start": v(207.58, 348.04) * mm, "end": v(207.5, 348.24) * mm});
            skLineSegment(sketch, "E1590", {"start": v(207.5, 348.24) * mm, "end": v(207.44, 348.44) * mm});
            skLineSegment(sketch, "E1591", {"start": v(207.44, 348.44) * mm, "end": v(207.39, 348.64) * mm});
            skLineSegment(sketch, "E1592", {"start": v(207.39, 348.64) * mm, "end": v(207.36, 348.87) * mm});
            skLineSegment(sketch, "E1593", {"start": v(207.36, 348.87) * mm, "end": v(207.36, 349.07) * mm});
            skLineSegment(sketch, "E1594", {"start": v(207.36, 349.07) * mm, "end": v(207.36, 356.8) * mm});
            skLineSegment(sketch, "E1595", {"start": v(207.36, 356.8) * mm, "end": v(207.33, 357.2) * mm});
            skLineSegment(sketch, "E1596", {"start": v(207.33, 357.2) * mm, "end": v(207.27, 357.6) * mm});
            skLineSegment(sketch, "E1597", {"start": v(207.27, 357.6) * mm, "end": v(207.19, 357.96) * mm});
            skLineSegment(sketch, "E1598", {"start": v(207.19, 357.96) * mm, "end": v(207.07, 358.3) * mm});
            skLineSegment(sketch, "E1599", {"start": v(207.07, 358.3) * mm, "end": v(206.9, 358.64) * mm});
            skLineSegment(sketch, "E1600", {"start": v(206.9, 358.64) * mm, "end": v(206.7, 358.95) * mm});
            skLineSegment(sketch, "E1601", {"start": v(206.7, 358.95) * mm, "end": v(206.48, 359.27) * mm});
            skLineSegment(sketch, "E1602", {"start": v(206.48, 359.27) * mm, "end": v(206.22, 359.55) * mm});
            skLineSegment(sketch, "E1603", {"start": v(206.22, 359.55) * mm, "end": v(205.9, 359.8) * mm});
            skLineSegment(sketch, "E1604", {"start": v(205.9, 359.8) * mm, "end": v(205.6, 360.03) * mm});
            skLineSegment(sketch, "E1605", {"start": v(205.6, 360.03) * mm, "end": v(205.28, 360.23) * mm});
            skLineSegment(sketch, "E1606", {"start": v(205.28, 360.23) * mm, "end": v(204.94, 360.4) * mm});
            skLineSegment(sketch, "E1607", {"start": v(204.94, 360.4) * mm, "end": v(204.6, 360.52) * mm});
            skLineSegment(sketch, "E1608", {"start": v(204.6, 360.52) * mm, "end": v(204.23, 360.6) * mm});
            skLineSegment(sketch, "E1609", {"start": v(204.23, 360.6) * mm, "end": v(203.86, 360.66) * mm});
            skLineSegment(sketch, "E1610", {"start": v(203.86, 360.66) * mm, "end": v(203.47, 360.69) * mm});
            skLineSegment(sketch, "E1611", {"start": v(203.47, 360.69) * mm, "end": v(203.07, 360.66) * mm});
            skLineSegment(sketch, "E1612", {"start": v(203.07, 360.66) * mm, "end": v(202.7, 360.6) * mm});
            skLineSegment(sketch, "E1613", {"start": v(202.7, 360.6) * mm, "end": v(202.33, 360.52) * mm});
            skLineSegment(sketch, "E1614", {"start": v(202.33, 360.52) * mm, "end": v(201.99, 360.4) * mm});
            skLineSegment(sketch, "E1615", {"start": v(201.99, 360.4) * mm, "end": v(201.65, 360.23) * mm});
            skLineSegment(sketch, "E1616", {"start": v(201.65, 360.23) * mm, "end": v(201.33, 360.03) * mm});
            skLineSegment(sketch, "E1617", {"start": v(201.33, 360.03) * mm, "end": v(201.02, 359.8) * mm});
            skLineSegment(sketch, "E1618", {"start": v(201.02, 359.8) * mm, "end": v(200.7, 359.55) * mm});
            skLineSegment(sketch, "E1619", {"start": v(200.7, 359.55) * mm, "end": v(200.45, 359.27) * mm});
            skLineSegment(sketch, "E1620", {"start": v(200.45, 359.27) * mm, "end": v(200.23, 358.95) * mm});
            skLineSegment(sketch, "E1621", {"start": v(200.23, 358.95) * mm, "end": v(200.03, 358.64) * mm});
            skLineSegment(sketch, "E1622", {"start": v(200.03, 358.64) * mm, "end": v(199.86, 358.3) * mm});
            skLineSegment(sketch, "E1623", {"start": v(199.86, 358.3) * mm, "end": v(199.74, 357.96) * mm});
            skLineSegment(sketch, "E1624", {"start": v(199.74, 357.96) * mm, "end": v(199.66, 357.6) * mm});
            skLineSegment(sketch, "E1625", {"start": v(199.66, 357.6) * mm, "end": v(199.6, 357.2) * mm});
            skLineSegment(sketch, "E1626", {"start": v(199.6, 357.2) * mm, "end": v(199.57, 356.8) * mm});
            skLineSegment(sketch, "E1627", {"start": v(199.57, 356.8) * mm, "end": v(199.57, 349.07) * mm});
            skLineSegment(sketch, "E1628", {"start": v(199.57, 349.07) * mm, "end": v(199.57, 348.87) * mm});
            skLineSegment(sketch, "E1629", {"start": v(199.57, 348.87) * mm, "end": v(199.54, 348.64) * mm});
            skLineSegment(sketch, "E1630", {"start": v(199.54, 348.64) * mm, "end": v(199.49, 348.44) * mm});
            skLineSegment(sketch, "E1631", {"start": v(199.49, 348.44) * mm, "end": v(199.43, 348.24) * mm});
            skLineSegment(sketch, "E1632", {"start": v(199.43, 348.24) * mm, "end": v(199.35, 348.04) * mm});
            skLineSegment(sketch, "E1633", {"start": v(199.35, 348.04) * mm, "end": v(199.23, 347.85) * mm});
            skLineSegment(sketch, "E1634", {"start": v(199.23, 347.85) * mm, "end": v(199.09, 347.67) * mm});
            skLineSegment(sketch, "E1635", {"start": v(199.09, 347.67) * mm, "end": v(198.95, 347.5) * mm});
            skLineSegment(sketch, "E1636", {"start": v(198.95, 347.5) * mm, "end": v(198.78, 347.36) * mm});
            skLineSegment(sketch, "E1637", {"start": v(198.78, 347.36) * mm, "end": v(198.6, 347.22) * mm});
            skLineSegment(sketch, "E1638", {"start": v(198.6, 347.22) * mm, "end": v(198.4, 347.1) * mm});
            skLineSegment(sketch, "E1639", {"start": v(198.4, 347.1) * mm, "end": v(198.2, 347.02) * mm});
            skLineSegment(sketch, "E1640", {"start": v(198.2, 347.02) * mm, "end": v(198.01, 346.96) * mm});
            skLineSegment(sketch, "E1641", {"start": v(198.01, 346.96) * mm, "end": v(197.81, 346.9) * mm});
            skLineSegment(sketch, "E1642", {"start": v(197.81, 346.9) * mm, "end": v(197.58, 346.88) * mm});
            skLineSegment(sketch, "E1643", {"start": v(197.58, 346.88) * mm, "end": v(197.36, 346.85) * mm});
            skLineSegment(sketch, "E1644", {"start": v(197.36, 346.85) * mm, "end": v(197.16, 346.88) * mm});
            skLineSegment(sketch, "E1645", {"start": v(197.16, 346.88) * mm, "end": v(196.93, 346.9) * mm});
            skLineSegment(sketch, "E1646", {"start": v(196.93, 346.9) * mm, "end": v(196.73, 346.96) * mm});
            skLineSegment(sketch, "E1647", {"start": v(196.73, 346.96) * mm, "end": v(196.53, 347.02) * mm});
            skLineSegment(sketch, "E1648", {"start": v(196.53, 347.02) * mm, "end": v(196.33, 347.1) * mm});
            skLineSegment(sketch, "E1649", {"start": v(196.33, 347.1) * mm, "end": v(196.14, 347.22) * mm});
            skLineSegment(sketch, "E1650", {"start": v(196.14, 347.22) * mm, "end": v(195.96, 347.36) * mm});
            skLineSegment(sketch, "E1651", {"start": v(195.96, 347.36) * mm, "end": v(195.8, 347.5) * mm});
            skLineSegment(sketch, "E1652", {"start": v(195.8, 347.5) * mm, "end": v(195.65, 347.67) * mm});
            skLineSegment(sketch, "E1653", {"start": v(195.65, 347.67) * mm, "end": v(195.51, 347.85) * mm});
            skLineSegment(sketch, "E1654", {"start": v(195.51, 347.85) * mm, "end": v(195.4, 348.04) * mm});
            skLineSegment(sketch, "E1655", {"start": v(195.4, 348.04) * mm, "end": v(195.31, 348.24) * mm});
            skLineSegment(sketch, "E1656", {"start": v(195.31, 348.24) * mm, "end": v(195.25, 348.44) * mm});
            skLineSegment(sketch, "E1657", {"start": v(195.25, 348.44) * mm, "end": v(195.2, 348.64) * mm});
            skLineSegment(sketch, "E1658", {"start": v(195.2, 348.64) * mm, "end": v(195.17, 348.87) * mm});
            skLineSegment(sketch, "E1659", {"start": v(195.17, 348.87) * mm, "end": v(195.14, 349.07) * mm});
            skLineSegment(sketch, "E1660", {"start": v(195.14, 349.07) * mm, "end": v(195.14, 356.8) * mm});
            skLineSegment(sketch, "E1661", {"start": v(195.14, 356.8) * mm, "end": v(195.2, 357.65) * mm});
            skLineSegment(sketch, "E1662", {"start": v(216.25, 338.58) * mm, "end": v(216.22, 338.81) * mm});
            skLineSegment(sketch, "E1663", {"start": v(216.22, 338.81) * mm, "end": v(216.22, 339.04) * mm});
            skLineSegment(sketch, "E1664", {"start": v(216.22, 339.04) * mm, "end": v(216.22, 339.12) * mm});
            skLineSegment(sketch, "E1665", {"start": v(216.22, 339.12) * mm, "end": v(216.22, 339.2) * mm});
            skLineSegment(sketch, "E1666", {"start": v(216.22, 339.2) * mm, "end": v(216.22, 339.3) * mm});
            skLineSegment(sketch, "E1667", {"start": v(216.22, 339.3) * mm, "end": v(216.22, 339.38) * mm});
            skLineSegment(sketch, "E1668", {"start": v(216.22, 339.38) * mm, "end": v(216.25, 339.46) * mm});
            skLineSegment(sketch, "E1669", {"start": v(216.25, 339.46) * mm, "end": v(216.28, 339.52) * mm});
            skLineSegment(sketch, "E1670", {"start": v(216.28, 339.52) * mm, "end": v(216.28, 339.6) * mm});
            skLineSegment(sketch, "E1671", {"start": v(216.28, 339.6) * mm, "end": v(216.3, 339.66) * mm});
            skLineSegment(sketch, "E1672", {"start": v(216.3, 339.66) * mm, "end": v(220.65, 362.33) * mm});
            skLineSegment(sketch, "E1673", {"start": v(220.65, 362.33) * mm, "end": v(220.68, 362.56) * mm});
            skLineSegment(sketch, "E1674", {"start": v(220.68, 362.56) * mm, "end": v(220.74, 362.79) * mm});
            skLineSegment(sketch, "E1675", {"start": v(220.74, 362.79) * mm, "end": v(220.8, 362.99) * mm});
            skLineSegment(sketch, "E1676", {"start": v(220.8, 362.99) * mm, "end": v(220.88, 363.19) * mm});
            skLineSegment(sketch, "E1677", {"start": v(220.88, 363.19) * mm, "end": v(220.97, 363.39) * mm});
            skLineSegment(sketch, "E1678", {"start": v(220.97, 363.39) * mm, "end": v(221.08, 363.56) * mm});
            skLineSegment(sketch, "E1679", {"start": v(221.08, 363.56) * mm, "end": v(221.2, 363.73) * mm});
            skLineSegment(sketch, "E1680", {"start": v(221.2, 363.73) * mm, "end": v(221.33, 363.9) * mm});
            skLineSegment(sketch, "E1681", {"start": v(221.33, 363.9) * mm, "end": v(221.5, 364.04) * mm});
            skLineSegment(sketch, "E1682", {"start": v(221.5, 364.04) * mm, "end": v(221.68, 364.18) * mm});
            skLineSegment(sketch, "E1683", {"start": v(221.68, 364.18) * mm, "end": v(221.85, 364.3) * mm});
            skLineSegment(sketch, "E1684", {"start": v(221.85, 364.3) * mm, "end": v(222.02, 364.38) * mm});
            skLineSegment(sketch, "E1685", {"start": v(222.02, 364.38) * mm, "end": v(222.22, 364.44) * mm});
            skLineSegment(sketch, "E1686", {"start": v(222.22, 364.44) * mm, "end": v(222.41, 364.5) * mm});
            skLineSegment(sketch, "E1687", {"start": v(222.41, 364.5) * mm, "end": v(222.64, 364.52) * mm});
            skLineSegment(sketch, "E1688", {"start": v(222.64, 364.52) * mm, "end": v(222.87, 364.52) * mm});
            skLineSegment(sketch, "E1689", {"start": v(222.87, 364.52) * mm, "end": v(223.07, 364.52) * mm});
            skLineSegment(sketch, "E1690", {"start": v(223.07, 364.52) * mm, "end": v(223.3, 364.5) * mm});
            skLineSegment(sketch, "E1691", {"start": v(223.3, 364.5) * mm, "end": v(223.5, 364.44) * mm});
            skLineSegment(sketch, "E1692", {"start": v(223.5, 364.44) * mm, "end": v(223.7, 364.38) * mm});
            skLineSegment(sketch, "E1693", {"start": v(223.7, 364.38) * mm, "end": v(223.9, 364.3) * mm});
            skLineSegment(sketch, "E1694", {"start": v(223.9, 364.3) * mm, "end": v(224.1, 364.18) * mm});
            skLineSegment(sketch, "E1695", {"start": v(224.1, 364.18) * mm, "end": v(224.26, 364.04) * mm});
            skLineSegment(sketch, "E1696", {"start": v(224.26, 364.04) * mm, "end": v(224.43, 363.9) * mm});
            skLineSegment(sketch, "E1697", {"start": v(224.43, 363.9) * mm, "end": v(224.57, 363.73) * mm});
            skLineSegment(sketch, "E1698", {"start": v(224.57, 363.73) * mm, "end": v(224.72, 363.56) * mm});
            skLineSegment(sketch, "E1699", {"start": v(224.72, 363.56) * mm, "end": v(224.83, 363.36) * mm});
            skLineSegment(sketch, "E1700", {"start": v(224.83, 363.36) * mm, "end": v(224.91, 363.16) * mm});
            skLineSegment(sketch, "E1701", {"start": v(224.91, 363.16) * mm, "end": v(224.97, 362.96) * mm});
            skLineSegment(sketch, "E1702", {"start": v(224.97, 362.96) * mm, "end": v(225.03, 362.76) * mm});
            skLineSegment(sketch, "E1703", {"start": v(225.03, 362.76) * mm, "end": v(225.06, 362.53) * mm});
            skLineSegment(sketch, "E1704", {"start": v(225.06, 362.53) * mm, "end": v(225.09, 362.3) * mm});
            skLineSegment(sketch, "E1705", {"start": v(225.09, 362.3) * mm, "end": v(225.06, 362.25) * mm});
            skLineSegment(sketch, "E1706", {"start": v(225.06, 362.25) * mm, "end": v(225.06, 362.16) * mm});
            skLineSegment(sketch, "E1707", {"start": v(225.06, 362.16) * mm, "end": v(225.06, 362.08) * mm});
            skLineSegment(sketch, "E1708", {"start": v(225.06, 362.08) * mm, "end": v(225.06, 362) * mm});
            skLineSegment(sketch, "E1709", {"start": v(225.06, 362) * mm, "end": v(225.06, 361.9) * mm});
            skLineSegment(sketch, "E1710", {"start": v(225.06, 361.9) * mm, "end": v(225.03, 361.82) * mm});
            skLineSegment(sketch, "E1711", {"start": v(225.03, 361.82) * mm, "end": v(225.03, 361.77) * mm});
            skLineSegment(sketch, "E1712", {"start": v(225.03, 361.77) * mm, "end": v(225.03, 361.68) * mm});
            skLineSegment(sketch, "E1713", {"start": v(225.03, 361.68) * mm, "end": v(221.1, 341.25) * mm});
            skLineSegment(sketch, "E1714", {"start": v(221.1, 341.25) * mm, "end": v(228.95, 341.25) * mm});
            skLineSegment(sketch, "E1715", {"start": v(228.95, 341.25) * mm, "end": v(228.95, 355.66) * mm});
            skLineSegment(sketch, "E1716", {"start": v(228.95, 355.66) * mm, "end": v(228.95, 355.86) * mm});
            skLineSegment(sketch, "E1717", {"start": v(228.95, 355.86) * mm, "end": v(228.98, 356.08) * mm});
            skLineSegment(sketch, "E1718", {"start": v(228.98, 356.08) * mm, "end": v(229.03, 356.28) * mm});
            skLineSegment(sketch, "E1719", {"start": v(229.03, 356.28) * mm, "end": v(229.12, 356.48) * mm});
            skLineSegment(sketch, "E1720", {"start": v(229.12, 356.48) * mm, "end": v(229.2, 356.68) * mm});
            skLineSegment(sketch, "E1721", {"start": v(229.2, 356.68) * mm, "end": v(229.32, 356.88) * mm});
            skLineSegment(sketch, "E1722", {"start": v(229.32, 356.88) * mm, "end": v(229.46, 357.05) * mm});
            skLineSegment(sketch, "E1723", {"start": v(229.46, 357.05) * mm, "end": v(229.6, 357.22) * mm});
            skLineSegment(sketch, "E1724", {"start": v(229.6, 357.22) * mm, "end": v(229.77, 357.36) * mm});
            skLineSegment(sketch, "E1725", {"start": v(229.77, 357.36) * mm, "end": v(229.94, 357.5) * mm});
            skLineSegment(sketch, "E1726", {"start": v(229.94, 357.5) * mm, "end": v(230.11, 357.62) * mm});
            skLineSegment(sketch, "E1727", {"start": v(230.11, 357.62) * mm, "end": v(230.31, 357.7) * mm});
            skLineSegment(sketch, "E1728", {"start": v(230.31, 357.7) * mm, "end": v(230.51, 357.76) * mm});
            skLineSegment(sketch, "E1729", {"start": v(230.51, 357.76) * mm, "end": v(230.71, 357.82) * mm});
            skLineSegment(sketch, "E1730", {"start": v(230.71, 357.82) * mm, "end": v(230.94, 357.85) * mm});
            skLineSegment(sketch, "E1731", {"start": v(230.94, 357.85) * mm, "end": v(231.16, 357.87) * mm});
            skLineSegment(sketch, "E1732", {"start": v(231.16, 357.87) * mm, "end": v(231.4, 357.85) * mm});
            skLineSegment(sketch, "E1733", {"start": v(231.4, 357.85) * mm, "end": v(231.62, 357.82) * mm});
            skLineSegment(sketch, "E1734", {"start": v(231.62, 357.82) * mm, "end": v(231.82, 357.76) * mm});
            skLineSegment(sketch, "E1735", {"start": v(231.82, 357.76) * mm, "end": v(232.02, 357.7) * mm});
            skLineSegment(sketch, "E1736", {"start": v(232.02, 357.7) * mm, "end": v(232.22, 357.62) * mm});
            skLineSegment(sketch, "E1737", {"start": v(232.22, 357.62) * mm, "end": v(232.39, 357.5) * mm});
            skLineSegment(sketch, "E1738", {"start": v(232.39, 357.5) * mm, "end": v(232.56, 357.36) * mm});
            skLineSegment(sketch, "E1739", {"start": v(232.56, 357.36) * mm, "end": v(232.73, 357.22) * mm});
            skLineSegment(sketch, "E1740", {"start": v(232.73, 357.22) * mm, "end": v(232.87, 357.05) * mm});
            skLineSegment(sketch, "E1741", {"start": v(232.87, 357.05) * mm, "end": v(233.01, 356.88) * mm});
            skLineSegment(sketch, "E1742", {"start": v(233.01, 356.88) * mm, "end": v(233.13, 356.68) * mm});
            skLineSegment(sketch, "E1743", {"start": v(233.13, 356.68) * mm, "end": v(233.21, 356.48) * mm});
            skLineSegment(sketch, "E1744", {"start": v(233.21, 356.48) * mm, "end": v(233.3, 356.28) * mm});
            skLineSegment(sketch, "E1745", {"start": v(233.3, 356.28) * mm, "end": v(233.35, 356.08) * mm});
            skLineSegment(sketch, "E1746", {"start": v(233.35, 356.08) * mm, "end": v(233.38, 355.86) * mm});
            skLineSegment(sketch, "E1747", {"start": v(233.38, 355.86) * mm, "end": v(233.38, 355.66) * mm});
            skLineSegment(sketch, "E1748", {"start": v(233.38, 355.66) * mm, "end": v(233.38, 329.07) * mm});
            skLineSegment(sketch, "E1749", {"start": v(233.38, 329.07) * mm, "end": v(233.38, 328.84) * mm});
            skLineSegment(sketch, "E1750", {"start": v(233.38, 328.84) * mm, "end": v(233.35, 328.61) * mm});
            skLineSegment(sketch, "E1751", {"start": v(233.35, 328.61) * mm, "end": v(233.3, 328.41) * mm});
            skLineSegment(sketch, "E1752", {"start": v(233.3, 328.41) * mm, "end": v(233.21, 328.21) * mm});
            skLineSegment(sketch, "E1753", {"start": v(233.21, 328.21) * mm, "end": v(233.13, 328.02) * mm});
            skLineSegment(sketch, "E1754", {"start": v(233.13, 328.02) * mm, "end": v(233.01, 327.82) * mm});
            skLineSegment(sketch, "E1755", {"start": v(233.01, 327.82) * mm, "end": v(232.87, 327.65) * mm});
            skLineSegment(sketch, "E1756", {"start": v(232.87, 327.65) * mm, "end": v(232.73, 327.48) * mm});
            skLineSegment(sketch, "E1757", {"start": v(232.73, 327.48) * mm, "end": v(232.56, 327.33) * mm});
            skLineSegment(sketch, "E1758", {"start": v(232.56, 327.33) * mm, "end": v(232.39, 327.2) * mm});
            skLineSegment(sketch, "E1759", {"start": v(232.39, 327.2) * mm, "end": v(232.22, 327.08) * mm});
            skLineSegment(sketch, "E1760", {"start": v(232.22, 327.08) * mm, "end": v(232.02, 327) * mm});
            skLineSegment(sketch, "E1761", {"start": v(232.02, 327) * mm, "end": v(231.82, 326.94) * mm});
            skLineSegment(sketch, "E1762", {"start": v(231.82, 326.94) * mm, "end": v(231.62, 326.88) * mm});
            skLineSegment(sketch, "E1763", {"start": v(231.62, 326.88) * mm, "end": v(231.4, 326.85) * mm});
            skLineSegment(sketch, "E1764", {"start": v(231.4, 326.85) * mm, "end": v(231.16, 326.85) * mm});
            skLineSegment(sketch, "E1765", {"start": v(231.16, 326.85) * mm, "end": v(230.94, 326.85) * mm});
            skLineSegment(sketch, "E1766", {"start": v(230.94, 326.85) * mm, "end": v(230.71, 326.88) * mm});
            skLineSegment(sketch, "E1767", {"start": v(230.71, 326.88) * mm, "end": v(230.51, 326.94) * mm});
            skLineSegment(sketch, "E1768", {"start": v(230.51, 326.94) * mm, "end": v(230.31, 327) * mm});
            skLineSegment(sketch, "E1769", {"start": v(230.31, 327) * mm, "end": v(230.11, 327.08) * mm});
            skLineSegment(sketch, "E1770", {"start": v(230.11, 327.08) * mm, "end": v(229.94, 327.2) * mm});
            skLineSegment(sketch, "E1771", {"start": v(229.94, 327.2) * mm, "end": v(229.77, 327.33) * mm});
            skLineSegment(sketch, "E1772", {"start": v(229.77, 327.33) * mm, "end": v(229.6, 327.48) * mm});
            skLineSegment(sketch, "E1773", {"start": v(229.6, 327.48) * mm, "end": v(229.46, 327.65) * mm});
            skLineSegment(sketch, "E1774", {"start": v(229.46, 327.65) * mm, "end": v(229.32, 327.82) * mm});
            skLineSegment(sketch, "E1775", {"start": v(229.32, 327.82) * mm, "end": v(229.2, 328.02) * mm});
            skLineSegment(sketch, "E1776", {"start": v(229.2, 328.02) * mm, "end": v(229.12, 328.21) * mm});
            skLineSegment(sketch, "E1777", {"start": v(229.12, 328.21) * mm, "end": v(229.03, 328.41) * mm});
            skLineSegment(sketch, "E1778", {"start": v(229.03, 328.41) * mm, "end": v(228.98, 328.61) * mm});
            skLineSegment(sketch, "E1779", {"start": v(228.98, 328.61) * mm, "end": v(228.95, 328.84) * mm});
            skLineSegment(sketch, "E1780", {"start": v(228.95, 328.84) * mm, "end": v(228.95, 329.07) * mm});
            skLineSegment(sketch, "E1781", {"start": v(228.95, 329.07) * mm, "end": v(228.95, 336.82) * mm});
            skLineSegment(sketch, "E1782", {"start": v(228.95, 336.82) * mm, "end": v(218.44, 336.82) * mm});
            skLineSegment(sketch, "E1783", {"start": v(218.44, 336.82) * mm, "end": v(218.2, 336.82) * mm});
            skLineSegment(sketch, "E1784", {"start": v(218.2, 336.82) * mm, "end": v(217.98, 336.85) * mm});
            skLineSegment(sketch, "E1785", {"start": v(217.98, 336.85) * mm, "end": v(217.78, 336.9) * mm});
            skLineSegment(sketch, "E1786", {"start": v(217.78, 336.9) * mm, "end": v(217.58, 336.96) * mm});
            skLineSegment(sketch, "E1787", {"start": v(217.58, 336.96) * mm, "end": v(217.39, 337.08) * mm});
            skLineSegment(sketch, "E1788", {"start": v(217.39, 337.08) * mm, "end": v(217.19, 337.2) * mm});
            skLineSegment(sketch, "E1789", {"start": v(217.19, 337.2) * mm, "end": v(217.02, 337.3) * mm});
            skLineSegment(sketch, "E1790", {"start": v(217.02, 337.3) * mm, "end": v(216.85, 337.48) * mm});
            skLineSegment(sketch, "E1791", {"start": v(216.85, 337.48) * mm, "end": v(216.7, 337.65) * mm});
            skLineSegment(sketch, "E1792", {"start": v(216.7, 337.65) * mm, "end": v(216.56, 337.82) * mm});
            skLineSegment(sketch, "E1793", {"start": v(216.56, 337.82) * mm, "end": v(216.45, 338.02) * mm});
            skLineSegment(sketch, "E1794", {"start": v(216.45, 338.02) * mm, "end": v(216.36, 338.19) * mm});
            skLineSegment(sketch, "E1795", {"start": v(216.36, 338.19) * mm, "end": v(216.3, 338.38) * mm});
            skLineSegment(sketch, "E1796", {"start": v(216.3, 338.38) * mm, "end": v(216.25, 338.58) * mm});
            skLineSegment(sketch, "E1797.0", {"start": v(-42.41, 385.29) * mm, "end": v(275.09, 385.29) * mm});
            skLineSegment(sketch, "E1798", {"start": v(-42.41, 385.29) * mm, "end": v(-42.41, -224.31) * mm});
            skLineSegment(sketch, "E1799", {"start": v(275.09, -224.31) * mm, "end": v(275.09, 385.29) * mm});
            skCircle(sketch, "E1800", {"center": v(-23.36, -205.26) * mm, "radius": 2.1 * mm});
            skCircle(sketch, "E1801", {"center": v(256.04, -205.26) * mm, "radius": 2.1 * mm});
            skPoint(sketch, "E1802.endSnap0", {"position": v(116.34, -224.31) * mm});
            skCircle(sketch, "E1803", {"center": v(116.34, -205.26) * mm, "radius": 2.1 * mm});
            skCircle(sketch, "E1804", {"center": v(-23.36, 292.18) * mm, "radius": 2.1 * mm});
            skCircle(sketch, "E1805", {"center": v(256.04, 292.18) * mm, "radius": 2.1 * mm});
            skCircle(sketch, "E1806", {"center": v(116.34, 292.18) * mm, "radius": 2.1 * mm});
            skCircle(sketch, "E1807", {"center": v(256.04, 43.46) * mm, "radius": 2.1 * mm});
            skCircle(sketch, "E1808", {"center": v(-23.36, 43.46) * mm, "radius": 2.1 * mm});
            skLineSegment(sketch, "E1809", {"start": v(49.77, 349.35) * mm, "end": v(49.9, 349.5) * mm});
            skLineSegment(sketch, "E1810", {"start": v(109.54, 333.7) * mm, "end": v(109.71, 333.36) * mm});
            skLineSegment(sketch, "E1811", {"start": v(209.35, 362.68) * mm, "end": v(209.91, 362.05) * mm});
            skLineSegment(sketch, "E1812", {"start": v(196.6, 127.96) * mm, "end": v(196.6, 273.13) * mm, "construction": true});
            skLineSegment(sketch, "E1813.MirrorCS", {"start": v(180.48, 241.47) * mm, "end": v(180.48, 221.67) * mm});
            skLineSegment(sketch, "E1814.MirrorCS", {"start": v(202.58, 241.47) * mm, "end": v(180.48, 241.47) * mm});
            skLineSegment(sketch, "E1815.MirrorCS", {"start": v(202.58, 241.47) * mm, "end": v(202.58, 221.67) * mm});
            skLineSegment(sketch, "E1816.MirrorCS", {"start": v(202.58, 221.67) * mm, "end": v(180.48, 221.67) * mm});
            skLineSegment(sketch, "E1817.0", {"start": v(220.54, 244.58) * mm, "end": v(231.04, 244.58) * mm});
            skLineSegment(sketch, "E1818.0", {"start": v(220.54, 218.58) * mm, "end": v(231.04, 218.58) * mm});
            skLineSegment(sketch, "E1819.trimOffspring", {"start": v(231.04, 244.58) * mm, "end": v(231.04, 218.58) * mm});
            skLineSegment(sketch, "E1820.0", {"start": v(220.54, 244.58) * mm, "end": v(220.54, 218.58) * mm});
            skSolve(sketch);
        }
        {
            var Q0;
            Q0=makeQuery(id+"F0.imprint","IMPRINT",FACE,{"disambiguationData":[TD([[makeQuery(id+"F0.imprint","IMPRINT",EDGE,{"derivedFrom":sQuery(id+"F0.wireOp",EDGE,"E5")}),-1.0]])]});
            extrude(context, id + "F1", {"entities" : qUnion([Q0]), "depth" : 2.03 * mm, "offsetDistance" : 25.4 * mm});
        }
    });
